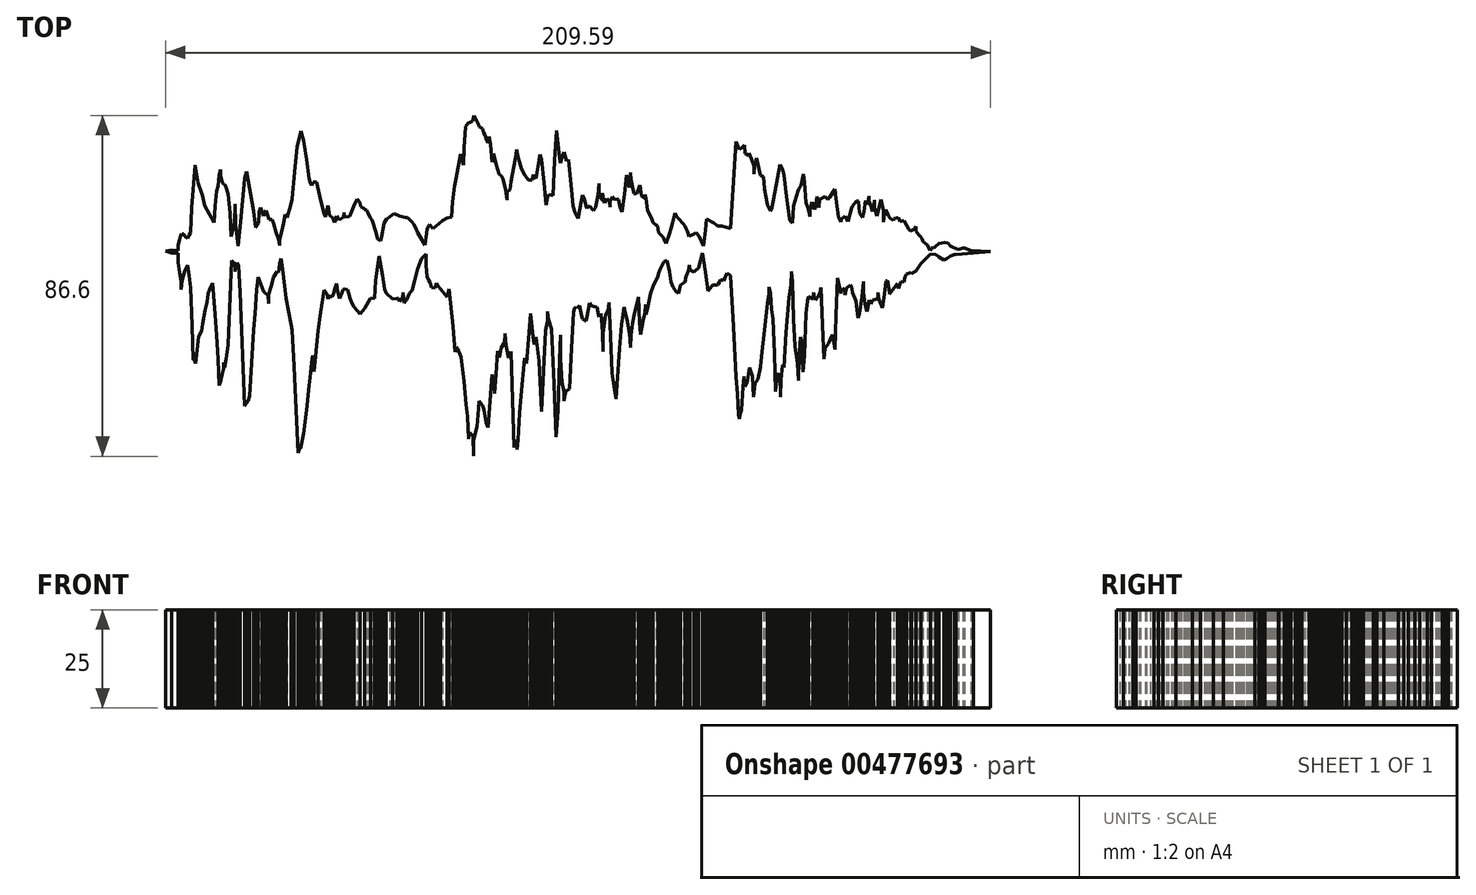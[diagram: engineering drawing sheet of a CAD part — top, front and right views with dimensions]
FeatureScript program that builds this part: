
annotation { "Feature Type Name" : "Feature", "Feature Type Description" : "" }
export const myFeature = defineFeature(function(context is Context, id is Id, definition is map)
    precondition{}
    {
        {
            var Q0;
            Q0=qCreatedBy(makeId("Top.planeOp"),FACE);
            var sketch = newSketch(context, id + "F0", { "sketchPlane" : qUnion([Q0])});
            skLineSegment(sketch, "E0", {"start": v(895.7, 1075.82) * mm, "end": v(892.97, 1101.18) * mm});
            skLineSegment(sketch, "E1", {"start": v(892.97, 1101.18) * mm, "end": v(888.39, 1081.07) * mm});
            skLineSegment(sketch, "E2", {"start": v(888.39, 1081.07) * mm, "end": v(885.06, 1201.57) * mm});
            skLineSegment(sketch, "E3", {"start": v(885.06, 1201.57) * mm, "end": v(881.56, 1324.24) * mm});
            skLineSegment(sketch, "E4", {"start": v(881.56, 1324.24) * mm, "end": v(878.07, 1317.45) * mm});
            skLineSegment(sketch, "E5", {"start": v(878.07, 1317.45) * mm, "end": v(875.1, 1308.5) * mm});
            skLineSegment(sketch, "E6", {"start": v(875.1, 1308.5) * mm, "end": v(868.65, 1339.11) * mm});
            skLineSegment(sketch, "E7", {"start": v(868.65, 1339.11) * mm, "end": v(865.17, 1369.73) * mm});
            skLineSegment(sketch, "E8", {"start": v(865.17, 1369.73) * mm, "end": v(864.62, 1347.86) * mm});
            skLineSegment(sketch, "E9", {"start": v(864.62, 1347.86) * mm, "end": v(856.04, 1333.86) * mm});
            skLineSegment(sketch, "E10", {"start": v(856.04, 1333.86) * mm, "end": v(853.42, 1317.24) * mm});
            skLineSegment(sketch, "E11", {"start": v(853.42, 1317.24) * mm, "end": v(851, 1309.37) * mm});
            skLineSegment(sketch, "E12", {"start": v(851, 1309.37) * mm, "end": v(846.38, 1326) * mm});
            skLineSegment(sketch, "E13", {"start": v(846.38, 1326) * mm, "end": v(842.73, 1267.38) * mm});
            skLineSegment(sketch, "E14", {"start": v(842.73, 1267.38) * mm, "end": v(839.58, 1217.52) * mm});
            skLineSegment(sketch, "E15", {"start": v(839.58, 1217.52) * mm, "end": v(836.43, 1246.4) * mm});
            skLineSegment(sketch, "E16", {"start": v(836.43, 1246.4) * mm, "end": v(833.1, 1266.5) * mm});
            skLineSegment(sketch, "E17", {"start": v(833.1, 1266.5) * mm, "end": v(825.08, 1165.04) * mm});
            skLineSegment(sketch, "E18", {"start": v(825.08, 1165.04) * mm, "end": v(823, 1131.79) * mm});
            skLineSegment(sketch, "E19", {"start": v(823, 1131.79) * mm, "end": v(818.08, 1144.36) * mm});
            skLineSegment(sketch, "E20", {"start": v(818.08, 1144.36) * mm, "end": v(811.87, 1175.86) * mm});
            skLineSegment(sketch, "E21", {"start": v(811.87, 1175.86) * mm, "end": v(808.56, 1186.9) * mm});
            skLineSegment(sketch, "E22", {"start": v(808.56, 1186.9) * mm, "end": v(800.2, 1199.15) * mm});
            skLineSegment(sketch, "E23", {"start": v(800.2, 1199.15) * mm, "end": v(797.9, 1179.04) * mm});
            skLineSegment(sketch, "E24", {"start": v(797.9, 1179.04) * mm, "end": v(795.18, 1134.42) * mm});
            skLineSegment(sketch, "E25", {"start": v(795.18, 1134.42) * mm, "end": v(786.2, 1099.43) * mm});
            skLineSegment(sketch, "E26", {"start": v(786.2, 1099.43) * mm, "end": v(785.1, 1058.32) * mm});
            skLineSegment(sketch, "E27", {"start": v(785.1, 1058.32) * mm, "end": v(784.35, 1109.93) * mm});
            skLineSegment(sketch, "E28", {"start": v(784.35, 1109.93) * mm, "end": v(776.03, 1118.68) * mm});
            skLineSegment(sketch, "E29", {"start": v(776.03, 1118.68) * mm, "end": v(772.99, 1102.06) * mm});
            skLineSegment(sketch, "E30", {"start": v(772.99, 1102.06) * mm, "end": v(770.05, 1158.92) * mm});
            skLineSegment(sketch, "E31", {"start": v(770.05, 1158.92) * mm, "end": v(766.4, 1189.53) * mm});
            skLineSegment(sketch, "E32", {"start": v(766.4, 1189.53) * mm, "end": v(762.03, 1247.55) * mm});
            skLineSegment(sketch, "E33", {"start": v(762.03, 1247.55) * mm, "end": v(754, 1310.57) * mm});
            skLineSegment(sketch, "E34", {"start": v(754, 1310.57) * mm, "end": v(744.85, 1332.15) * mm});
            skLineSegment(sketch, "E35", {"start": v(744.85, 1332.15) * mm, "end": v(742.07, 1335.61) * mm});
            skLineSegment(sketch, "E36", {"start": v(742.07, 1335.61) * mm, "end": v(738.64, 1322.5) * mm});
            skLineSegment(sketch, "E37", {"start": v(738.64, 1322.5) * mm, "end": v(733.44, 1388.1) * mm});
            skLineSegment(sketch, "E38", {"start": v(733.44, 1388.1) * mm, "end": v(723.65, 1483.44) * mm});
            skLineSegment(sketch, "E39", {"start": v(723.65, 1483.44) * mm, "end": v(720.61, 1472.95) * mm});
            skLineSegment(sketch, "E40", {"start": v(720.61, 1472.95) * mm, "end": v(718.72, 1462.45) * mm});
            skLineSegment(sketch, "E41", {"start": v(718.72, 1462.45) * mm, "end": v(701.57, 1482.57) * mm});
            skLineSegment(sketch, "E42", {"start": v(701.57, 1482.57) * mm, "end": v(695.88, 1490.44) * mm});
            skLineSegment(sketch, "E43", {"start": v(695.88, 1490.44) * mm, "end": v(692.34, 1498.32) * mm});
            skLineSegment(sketch, "E44", {"start": v(692.34, 1498.32) * mm, "end": v(687.5, 1486.07) * mm});
            skLineSegment(sketch, "E45", {"start": v(687.5, 1486.07) * mm, "end": v(678.62, 1487.15) * mm});
            skLineSegment(sketch, "E46", {"start": v(678.62, 1487.15) * mm, "end": v(675.13, 1499.2) * mm});
            skLineSegment(sketch, "E47", {"start": v(675.13, 1499.2) * mm, "end": v(671.63, 1505.98) * mm});
            skLineSegment(sketch, "E48", {"start": v(671.63, 1505.98) * mm, "end": v(668.13, 1514.94) * mm});
            skLineSegment(sketch, "E49", {"start": v(668.13, 1514.94) * mm, "end": v(664.63, 1543.45) * mm});
            skLineSegment(sketch, "E50", {"start": v(664.63, 1543.45) * mm, "end": v(664.63, 1571.96) * mm});
            skLineSegment(sketch, "E51", {"start": v(664.63, 1571.96) * mm, "end": v(654.13, 1560.97) * mm});
            skLineSegment(sketch, "E52", {"start": v(654.13, 1560.97) * mm, "end": v(643.63, 1534.21) * mm});
            skLineSegment(sketch, "E53", {"start": v(643.63, 1534.21) * mm, "end": v(640.14, 1518.43) * mm});
            skLineSegment(sketch, "E54", {"start": v(640.14, 1518.43) * mm, "end": v(636.4, 1503.56) * mm});
            skLineSegment(sketch, "E55", {"start": v(636.4, 1503.56) * mm, "end": v(629.89, 1479.07) * mm});
            skLineSegment(sketch, "E56", {"start": v(629.89, 1479.07) * mm, "end": v(622.64, 1473.48) * mm});
            skLineSegment(sketch, "E57", {"start": v(622.64, 1473.48) * mm, "end": v(615.87, 1455.72) * mm});
            skLineSegment(sketch, "E58", {"start": v(615.87, 1455.72) * mm, "end": v(609.1, 1447.9) * mm});
            skLineSegment(sketch, "E59", {"start": v(609.1, 1447.9) * mm, "end": v(607.71, 1461.3) * mm});
            skLineSegment(sketch, "E60", {"start": v(607.71, 1461.3) * mm, "end": v(606.32, 1474.7) * mm});
            skLineSegment(sketch, "E61", {"start": v(606.32, 1474.7) * mm, "end": v(605.73, 1459.83) * mm});
            skLineSegment(sketch, "E62", {"start": v(605.73, 1459.83) * mm, "end": v(598.15, 1451.75) * mm});
            skLineSegment(sketch, "E63", {"start": v(598.15, 1451.75) * mm, "end": v(594.65, 1460.7) * mm});
            skLineSegment(sketch, "E64", {"start": v(594.65, 1460.7) * mm, "end": v(591.15, 1459.1) * mm});
            skLineSegment(sketch, "E65", {"start": v(591.15, 1459.1) * mm, "end": v(580.07, 1457.3) * mm});
            skLineSegment(sketch, "E66", {"start": v(580.07, 1457.3) * mm, "end": v(563.16, 1473.15) * mm});
            skLineSegment(sketch, "E67", {"start": v(563.16, 1473.15) * mm, "end": v(560.18, 1483.44) * mm});
            skLineSegment(sketch, "E68", {"start": v(560.18, 1483.44) * mm, "end": v(554.8, 1517.44) * mm});
            skLineSegment(sketch, "E69", {"start": v(554.8, 1517.44) * mm, "end": v(545.7, 1567.42) * mm});
            skLineSegment(sketch, "E70", {"start": v(545.7, 1567.42) * mm, "end": v(536.45, 1505.15) * mm});
            skLineSegment(sketch, "E71", {"start": v(536.45, 1505.15) * mm, "end": v(534.09, 1458.63) * mm});
            skLineSegment(sketch, "E72", {"start": v(534.09, 1458.63) * mm, "end": v(524.26, 1460.8) * mm});
            skLineSegment(sketch, "E73", {"start": v(524.26, 1460.8) * mm, "end": v(509.04, 1433.98) * mm});
            skLineSegment(sketch, "E74", {"start": v(509.04, 1433.98) * mm, "end": v(497.48, 1419.43) * mm});
            skLineSegment(sketch, "E75", {"start": v(497.48, 1419.43) * mm, "end": v(482.74, 1436.97) * mm});
            skLineSegment(sketch, "E76", {"start": v(482.74, 1436.97) * mm, "end": v(477.43, 1446.22) * mm});
            skLineSegment(sketch, "E77", {"start": v(477.43, 1446.22) * mm, "end": v(472.19, 1458.58) * mm});
            skLineSegment(sketch, "E78", {"start": v(472.19, 1458.58) * mm, "end": v(468.69, 1472.95) * mm});
            skLineSegment(sketch, "E79", {"start": v(468.69, 1472.95) * mm, "end": v(465.19, 1481.7) * mm});
            skLineSegment(sketch, "E80", {"start": v(465.19, 1481.7) * mm, "end": v(457.94, 1482.57) * mm});
            skLineSegment(sketch, "E81", {"start": v(457.94, 1482.57) * mm, "end": v(454.7, 1481.7) * mm});
            skLineSegment(sketch, "E82", {"start": v(454.7, 1481.7) * mm, "end": v(451.44, 1473.82) * mm});
            skLineSegment(sketch, "E83", {"start": v(451.44, 1473.82) * mm, "end": v(445.94, 1458.95) * mm});
            skLineSegment(sketch, "E84", {"start": v(445.94, 1458.95) * mm, "end": v(440.7, 1478.2) * mm});
            skLineSegment(sketch, "E85", {"start": v(440.7, 1478.2) * mm, "end": v(437.2, 1497.44) * mm});
            skLineSegment(sketch, "E86", {"start": v(437.2, 1497.44) * mm, "end": v(433.7, 1485.4) * mm});
            skLineSegment(sketch, "E87", {"start": v(433.7, 1485.4) * mm, "end": v(430.2, 1471.2) * mm});
            skLineSegment(sketch, "E88", {"start": v(430.2, 1471.2) * mm, "end": v(426.7, 1462.24) * mm});
            skLineSegment(sketch, "E89", {"start": v(426.7, 1462.24) * mm, "end": v(419.15, 1465.08) * mm});
            skLineSegment(sketch, "E90", {"start": v(419.15, 1465.08) * mm, "end": v(416.2, 1457.2) * mm});
            skLineSegment(sketch, "E91", {"start": v(416.2, 1457.2) * mm, "end": v(413.25, 1470.32) * mm});
            skLineSegment(sketch, "E92", {"start": v(413.25, 1470.32) * mm, "end": v(405.68, 1480.82) * mm});
            skLineSegment(sketch, "E93", {"start": v(405.68, 1480.82) * mm, "end": v(397, 1423.96) * mm});
            skLineSegment(sketch, "E94", {"start": v(397, 1423.96) * mm, "end": v(390.37, 1377.6) * mm});
            skLineSegment(sketch, "E95", {"start": v(390.37, 1377.6) * mm, "end": v(380.7, 1273.5) * mm});
            skLineSegment(sketch, "E96", {"start": v(380.7, 1273.5) * mm, "end": v(377.25, 1293.63) * mm});
            skLineSegment(sketch, "E97", {"start": v(377.25, 1293.63) * mm, "end": v(376.78, 1313.75) * mm});
            skLineSegment(sketch, "E98", {"start": v(376.78, 1313.75) * mm, "end": v(374.05, 1296.25) * mm});
            skLineSegment(sketch, "E99", {"start": v(374.05, 1296.25) * mm, "end": v(371.02, 1258.93) * mm});
            skLineSegment(sketch, "E100", {"start": v(371.02, 1258.93) * mm, "end": v(367.44, 1237.93) * mm});
            skLineSegment(sketch, "E101", {"start": v(367.44, 1237.93) * mm, "end": v(361.68, 1176.41) * mm});
            skLineSegment(sketch, "E102", {"start": v(361.68, 1176.41) * mm, "end": v(354.46, 1116.05) * mm});
            skLineSegment(sketch, "E103", {"start": v(354.46, 1116.05) * mm, "end": v(349.26, 1090.69) * mm});
            skLineSegment(sketch, "E104", {"start": v(349.26, 1090.69) * mm, "end": v(346.22, 1077.57) * mm});
            skLineSegment(sketch, "E105", {"start": v(346.22, 1077.57) * mm, "end": v(343.65, 1089.81) * mm});
            skLineSegment(sketch, "E106", {"start": v(343.65, 1089.81) * mm, "end": v(343.19, 1078.44) * mm});
            skLineSegment(sketch, "E107", {"start": v(343.19, 1078.44) * mm, "end": v(339.75, 1067.07) * mm});
            skLineSegment(sketch, "E108", {"start": v(339.75, 1067.07) * mm, "end": v(329.94, 1286.63) * mm});
            skLineSegment(sketch, "E109", {"start": v(329.94, 1286.63) * mm, "end": v(324.69, 1378.48) * mm});
            skLineSegment(sketch, "E110", {"start": v(324.69, 1378.48) * mm, "end": v(321.73, 1392.33) * mm});
            skLineSegment(sketch, "E111", {"start": v(321.73, 1392.33) * mm, "end": v(309.57, 1458.95) * mm});
            skLineSegment(sketch, "E112", {"start": v(309.57, 1458.95) * mm, "end": v(300.76, 1533.3) * mm});
            skLineSegment(sketch, "E113", {"start": v(300.76, 1533.3) * mm, "end": v(297.24, 1560.42) * mm});
            skLineSegment(sketch, "E114", {"start": v(297.24, 1560.42) * mm, "end": v(293.4, 1547.3) * mm});
            skLineSegment(sketch, "E115", {"start": v(293.4, 1547.3) * mm, "end": v(290.24, 1525.43) * mm});
            skLineSegment(sketch, "E116", {"start": v(290.24, 1525.43) * mm, "end": v(287.1, 1528.06) * mm});
            skLineSegment(sketch, "E117", {"start": v(287.1, 1528.06) * mm, "end": v(278.13, 1513.4) * mm});
            skLineSegment(sketch, "E118", {"start": v(278.13, 1513.4) * mm, "end": v(270.72, 1489.28) * mm});
            skLineSegment(sketch, "E119", {"start": v(270.72, 1489.28) * mm, "end": v(265.09, 1468.95) * mm});
            skLineSegment(sketch, "E120", {"start": v(265.09, 1468.95) * mm, "end": v(264.42, 1446.7) * mm});
            skLineSegment(sketch, "E121", {"start": v(264.42, 1446.7) * mm, "end": v(263.16, 1466.82) * mm});
            skLineSegment(sketch, "E122", {"start": v(263.16, 1466.82) * mm, "end": v(254.3, 1473.82) * mm});
            skLineSegment(sketch, "E123", {"start": v(254.3, 1473.82) * mm, "end": v(252.29, 1476.45) * mm});
            skLineSegment(sketch, "E124", {"start": v(252.29, 1476.45) * mm, "end": v(248.39, 1487.05) * mm});
            skLineSegment(sketch, "E125", {"start": v(248.39, 1487.05) * mm, "end": v(238.35, 1513.35) * mm});
            skLineSegment(sketch, "E126", {"start": v(238.35, 1513.35) * mm, "end": v(234.71, 1480.82) * mm});
            skLineSegment(sketch, "E127", {"start": v(234.71, 1480.82) * mm, "end": v(230.76, 1420.46) * mm});
            skLineSegment(sketch, "E128", {"start": v(230.76, 1420.46) * mm, "end": v(227.26, 1378.86) * mm});
            skLineSegment(sketch, "E129", {"start": v(227.26, 1378.86) * mm, "end": v(216.56, 1211.1) * mm});
            skLineSegment(sketch, "E130", {"start": v(216.56, 1211.1) * mm, "end": v(213.26, 1198.2) * mm});
            skLineSegment(sketch, "E131", {"start": v(213.26, 1198.2) * mm, "end": v(203.68, 1185.47) * mm});
            skLineSegment(sketch, "E132", {"start": v(203.68, 1185.47) * mm, "end": v(192.28, 1475.57) * mm});
            skLineSegment(sketch, "E133", {"start": v(192.28, 1475.57) * mm, "end": v(188.77, 1542.93) * mm});
            skLineSegment(sketch, "E134", {"start": v(188.77, 1542.93) * mm, "end": v(184.75, 1550.8) * mm});
            skLineSegment(sketch, "E135", {"start": v(184.75, 1550.8) * mm, "end": v(181.77, 1542.93) * mm});
            skLineSegment(sketch, "E136", {"start": v(181.77, 1542.93) * mm, "end": v(179.32, 1527.18) * mm});
            skLineSegment(sketch, "E137", {"start": v(179.32, 1527.18) * mm, "end": v(178.8, 1547.3) * mm});
            skLineSegment(sketch, "E138", {"start": v(178.8, 1547.3) * mm, "end": v(171, 1556.05) * mm});
            skLineSegment(sketch, "E139", {"start": v(171, 1556.05) * mm, "end": v(161.51, 1340.82) * mm});
            skLineSegment(sketch, "E140", {"start": v(161.51, 1340.82) * mm, "end": v(156.82, 1305.58) * mm});
            skLineSegment(sketch, "E141", {"start": v(156.82, 1305.58) * mm, "end": v(153.78, 1284) * mm});
            skLineSegment(sketch, "E142", {"start": v(153.78, 1284) * mm, "end": v(151.2, 1296.25) * mm});
            skLineSegment(sketch, "E143", {"start": v(151.2, 1296.25) * mm, "end": v(150.74, 1281.38) * mm});
            skLineSegment(sketch, "E144", {"start": v(150.74, 1281.38) * mm, "end": v(146.78, 1266.5) * mm});
            skLineSegment(sketch, "E145", {"start": v(146.78, 1266.5) * mm, "end": v(142.94, 1248.14) * mm});
            skLineSegment(sketch, "E146", {"start": v(142.94, 1248.14) * mm, "end": v(139.79, 1238.52) * mm});
            skLineSegment(sketch, "E147", {"start": v(139.79, 1238.52) * mm, "end": v(136.64, 1305.87) * mm});
            skLineSegment(sketch, "E148", {"start": v(136.64, 1305.87) * mm, "end": v(132.79, 1364.48) * mm});
            skLineSegment(sketch, "E149", {"start": v(132.79, 1364.48) * mm, "end": v(128.98, 1417.84) * mm});
            skLineSegment(sketch, "E150", {"start": v(128.98, 1417.84) * mm, "end": v(122.76, 1498.32) * mm});
            skLineSegment(sketch, "E151", {"start": v(122.76, 1498.32) * mm, "end": v(118.8, 1490.44) * mm});
            skLineSegment(sketch, "E152", {"start": v(118.8, 1490.44) * mm, "end": v(115.3, 1481.9) * mm});
            skLineSegment(sketch, "E153", {"start": v(115.3, 1481.9) * mm, "end": v(111.8, 1471.2) * mm});
            skLineSegment(sketch, "E154", {"start": v(111.8, 1471.2) * mm, "end": v(108.3, 1450.29) * mm});
            skLineSegment(sketch, "E155", {"start": v(108.3, 1450.29) * mm, "end": v(104.2, 1430.18) * mm});
            skLineSegment(sketch, "E156", {"start": v(104.2, 1430.18) * mm, "end": v(97.75, 1394.03) * mm});
            skLineSegment(sketch, "E157", {"start": v(97.75, 1394.03) * mm, "end": v(94.84, 1375.85) * mm});
            skLineSegment(sketch, "E158", {"start": v(94.84, 1375.85) * mm, "end": v(87.27, 1361.86) * mm});
            skLineSegment(sketch, "E159", {"start": v(87.27, 1361.86) * mm, "end": v(79.82, 1294.5) * mm});
            skLineSegment(sketch, "E160", {"start": v(79.82, 1294.5) * mm, "end": v(76.4, 1304.12) * mm});
            skLineSegment(sketch, "E161", {"start": v(76.4, 1304.12) * mm, "end": v(75.98, 1313.75) * mm});
            skLineSegment(sketch, "E162", {"start": v(75.98, 1313.75) * mm, "end": v(73.3, 1303.25) * mm});
            skLineSegment(sketch, "E163", {"start": v(73.3, 1303.25) * mm, "end": v(70.22, 1389.85) * mm});
            skLineSegment(sketch, "E164", {"start": v(70.22, 1389.85) * mm, "end": v(66.3, 1486.94) * mm});
            skLineSegment(sketch, "E165", {"start": v(66.3, 1486.94) * mm, "end": v(62.8, 1516.9) * mm});
            skLineSegment(sketch, "E166", {"start": v(62.8, 1516.9) * mm, "end": v(59.3, 1544.68) * mm});
            skLineSegment(sketch, "E167", {"start": v(59.3, 1544.68) * mm, "end": v(55.81, 1536.01) * mm});
            skLineSegment(sketch, "E168", {"start": v(55.81, 1536.01) * mm, "end": v(51.84, 1528.2) * mm});
            skLineSegment(sketch, "E169", {"start": v(51.84, 1528.2) * mm, "end": v(45.33, 1504.28) * mm});
            skLineSegment(sketch, "E170", {"start": v(45.33, 1504.28) * mm, "end": v(42.77, 1481.7) * mm});
            skLineSegment(sketch, "E171", {"start": v(42.77, 1481.7) * mm, "end": v(42.3, 1503.56) * mm});
            skLineSegment(sketch, "E172", {"start": v(42.3, 1503.56) * mm, "end": v(38.32, 1525.43) * mm});
            skLineSegment(sketch, "E173", {"start": v(38.32, 1525.43) * mm, "end": v(34.82, 1549.93) * mm});
            skLineSegment(sketch, "E174", {"start": v(34.82, 1549.93) * mm, "end": v(34.82, 1574.42) * mm});
            skLineSegment(sketch, "E175", {"start": v(34.82, 1574.42) * mm, "end": v(19.07, 1574.42) * mm});
            skLineSegment(sketch, "E176", {"start": v(19.07, 1574.42) * mm, "end": v(3.33, 1579.6) * mm});
            skLineSegment(sketch, "E177", {"start": v(3.33, 1579.6) * mm, "end": v(19.07, 1582.62) * mm});
            skLineSegment(sketch, "E178", {"start": v(19.07, 1582.62) * mm, "end": v(34.82, 1580.46) * mm});
            skLineSegment(sketch, "E179", {"start": v(34.82, 1580.46) * mm, "end": v(34.82, 1594.94) * mm});
            skLineSegment(sketch, "E180", {"start": v(34.82, 1594.94) * mm, "end": v(38.32, 1609.4) * mm});
            skLineSegment(sketch, "E181", {"start": v(38.32, 1609.4) * mm, "end": v(42.1, 1619.03) * mm});
            skLineSegment(sketch, "E182", {"start": v(42.1, 1619.03) * mm, "end": v(44.13, 1624.28) * mm});
            skLineSegment(sketch, "E183", {"start": v(44.13, 1624.28) * mm, "end": v(50.85, 1619.9) * mm});
            skLineSegment(sketch, "E184", {"start": v(50.85, 1619.9) * mm, "end": v(55.81, 1614.45) * mm});
            skLineSegment(sketch, "E185", {"start": v(55.81, 1614.45) * mm, "end": v(59.3, 1611.16) * mm});
            skLineSegment(sketch, "E186", {"start": v(59.3, 1611.16) * mm, "end": v(62.8, 1620.11) * mm});
            skLineSegment(sketch, "E187", {"start": v(62.8, 1620.11) * mm, "end": v(66.3, 1626.9) * mm});
            skLineSegment(sketch, "E188", {"start": v(66.3, 1626.9) * mm, "end": v(69.83, 1689) * mm});
            skLineSegment(sketch, "E189", {"start": v(69.83, 1689) * mm, "end": v(78.76, 1797.97) * mm});
            skLineSegment(sketch, "E190", {"start": v(78.76, 1797.97) * mm, "end": v(86.53, 1752.95) * mm});
            skLineSegment(sketch, "E191", {"start": v(86.53, 1752.95) * mm, "end": v(95.23, 1727.5) * mm});
            skLineSegment(sketch, "E192", {"start": v(95.23, 1727.5) * mm, "end": v(97.17, 1718.86) * mm});
            skLineSegment(sketch, "E193", {"start": v(97.17, 1718.86) * mm, "end": v(103.05, 1695.62) * mm});
            skLineSegment(sketch, "E194", {"start": v(103.05, 1695.62) * mm, "end": v(108.3, 1683.21) * mm});
            skLineSegment(sketch, "E195", {"start": v(108.3, 1683.21) * mm, "end": v(126.52, 1652.45) * mm});
            skLineSegment(sketch, "E196", {"start": v(126.52, 1652.45) * mm, "end": v(129.23, 1694.26) * mm});
            skLineSegment(sketch, "E197", {"start": v(129.23, 1694.26) * mm, "end": v(132.79, 1731.87) * mm});
            skLineSegment(sketch, "E198", {"start": v(132.79, 1731.87) * mm, "end": v(136.49, 1745) * mm});
            skLineSegment(sketch, "E199", {"start": v(136.49, 1745) * mm, "end": v(139.58, 1772.1) * mm});
            skLineSegment(sketch, "E200", {"start": v(139.58, 1772.1) * mm, "end": v(142.48, 1786.1) * mm});
            skLineSegment(sketch, "E201", {"start": v(142.48, 1786.1) * mm, "end": v(142.88, 1771.23) * mm});
            skLineSegment(sketch, "E202", {"start": v(142.88, 1771.23) * mm, "end": v(146.78, 1756.36) * mm});
            skLineSegment(sketch, "E203", {"start": v(146.78, 1756.36) * mm, "end": v(150.63, 1748.5) * mm});
            skLineSegment(sketch, "E204", {"start": v(150.63, 1748.5) * mm, "end": v(153.78, 1749.37) * mm});
            skLineSegment(sketch, "E205", {"start": v(153.78, 1749.37) * mm, "end": v(156.93, 1741.5) * mm});
            skLineSegment(sketch, "E206", {"start": v(156.93, 1741.5) * mm, "end": v(162.53, 1724.87) * mm});
            skLineSegment(sketch, "E207", {"start": v(162.53, 1724.87) * mm, "end": v(167.78, 1676.32) * mm});
            skLineSegment(sketch, "E208", {"start": v(167.78, 1676.32) * mm, "end": v(169.96, 1616.84) * mm});
            skLineSegment(sketch, "E209", {"start": v(169.96, 1616.84) * mm, "end": v(179, 1652.27) * mm});
            skLineSegment(sketch, "E210", {"start": v(179, 1652.27) * mm, "end": v(179.74, 1698.63) * mm});
            skLineSegment(sketch, "E211", {"start": v(179.74, 1698.63) * mm, "end": v(181.63, 1646.43) * mm});
            skLineSegment(sketch, "E212", {"start": v(181.63, 1646.43) * mm, "end": v(187.67, 1592.85) * mm});
            skLineSegment(sketch, "E213", {"start": v(187.67, 1592.85) * mm, "end": v(193.63, 1653.8) * mm});
            skLineSegment(sketch, "E214", {"start": v(193.63, 1653.8) * mm, "end": v(203.5, 1763.8) * mm});
            skLineSegment(sketch, "E215", {"start": v(203.5, 1763.8) * mm, "end": v(208.83, 1781.99) * mm});
            skLineSegment(sketch, "E216", {"start": v(208.83, 1781.99) * mm, "end": v(227.26, 1680.76) * mm});
            skLineSegment(sketch, "E217", {"start": v(227.26, 1680.76) * mm, "end": v(232.06, 1639.1) * mm});
            skLineSegment(sketch, "E218", {"start": v(232.06, 1639.1) * mm, "end": v(239.06, 1650.33) * mm});
            skLineSegment(sketch, "E219", {"start": v(239.06, 1650.33) * mm, "end": v(241.26, 1678.13) * mm});
            skLineSegment(sketch, "E220", {"start": v(241.26, 1678.13) * mm, "end": v(244.75, 1689.88) * mm});
            skLineSegment(sketch, "E221", {"start": v(244.75, 1689.88) * mm, "end": v(248.25, 1679.39) * mm});
            skLineSegment(sketch, "E222", {"start": v(248.25, 1679.39) * mm, "end": v(251.75, 1668.89) * mm});
            skLineSegment(sketch, "E223", {"start": v(251.75, 1668.89) * mm, "end": v(255.25, 1675.89) * mm});
            skLineSegment(sketch, "E224", {"start": v(255.25, 1675.89) * mm, "end": v(258.38, 1682.89) * mm});
            skLineSegment(sketch, "E225", {"start": v(258.38, 1682.89) * mm, "end": v(265.75, 1659.86) * mm});
            skLineSegment(sketch, "E226", {"start": v(265.75, 1659.86) * mm, "end": v(273.53, 1659.27) * mm});
            skLineSegment(sketch, "E227", {"start": v(273.53, 1659.27) * mm, "end": v(277.72, 1649.65) * mm});
            skLineSegment(sketch, "E228", {"start": v(277.72, 1649.65) * mm, "end": v(284.32, 1626.32) * mm});
            skLineSegment(sketch, "E229", {"start": v(284.32, 1626.32) * mm, "end": v(290.4, 1608.83) * mm});
            skLineSegment(sketch, "E230", {"start": v(290.4, 1608.83) * mm, "end": v(292.86, 1593.66) * mm});
            skLineSegment(sketch, "E231", {"start": v(292.86, 1593.66) * mm, "end": v(293.3, 1608.53) * mm});
            skLineSegment(sketch, "E232", {"start": v(293.3, 1608.53) * mm, "end": v(296.83, 1623.4) * mm});
            skLineSegment(sketch, "E233", {"start": v(296.83, 1623.4) * mm, "end": v(302.55, 1650.52) * mm});
            skLineSegment(sketch, "E234", {"start": v(302.55, 1650.52) * mm, "end": v(306.99, 1672.39) * mm});
            skLineSegment(sketch, "E235", {"start": v(306.99, 1672.39) * mm, "end": v(312.63, 1664.61) * mm});
            skLineSegment(sketch, "E236", {"start": v(312.63, 1664.61) * mm, "end": v(321.32, 1695.71) * mm});
            skLineSegment(sketch, "E237", {"start": v(321.32, 1695.71) * mm, "end": v(325.28, 1711.48) * mm});
            skLineSegment(sketch, "E238", {"start": v(325.28, 1711.48) * mm, "end": v(331.07, 1779.68) * mm});
            skLineSegment(sketch, "E239", {"start": v(331.07, 1779.68) * mm, "end": v(337.76, 1845) * mm});
            skLineSegment(sketch, "E240", {"start": v(337.76, 1845) * mm, "end": v(347.42, 1884.08) * mm});
            skLineSegment(sketch, "E241", {"start": v(347.42, 1884.08) * mm, "end": v(349.2, 1878.24) * mm});
            skLineSegment(sketch, "E242", {"start": v(349.2, 1878.24) * mm, "end": v(353.58, 1860.63) * mm});
            skLineSegment(sketch, "E243", {"start": v(353.58, 1860.63) * mm, "end": v(360.97, 1812.23) * mm});
            skLineSegment(sketch, "E244", {"start": v(360.97, 1812.23) * mm, "end": v(367.6, 1763.94) * mm});
            skLineSegment(sketch, "E245", {"start": v(367.6, 1763.94) * mm, "end": v(370.72, 1754.32) * mm});
            skLineSegment(sketch, "E246", {"start": v(370.72, 1754.32) * mm, "end": v(374.22, 1745.87) * mm});
            skLineSegment(sketch, "E247", {"start": v(374.22, 1745.87) * mm, "end": v(377.71, 1754.9) * mm});
            skLineSegment(sketch, "E248", {"start": v(377.71, 1754.9) * mm, "end": v(387.14, 1754.34) * mm});
            skLineSegment(sketch, "E249", {"start": v(387.14, 1754.34) * mm, "end": v(396.83, 1708.6) * mm});
            skLineSegment(sketch, "E250", {"start": v(396.83, 1708.6) * mm, "end": v(405.67, 1675.01) * mm});
            skLineSegment(sketch, "E251", {"start": v(405.67, 1675.01) * mm, "end": v(409.2, 1665.4) * mm});
            skLineSegment(sketch, "E252", {"start": v(409.2, 1665.4) * mm, "end": v(412.7, 1681.34) * mm});
            skLineSegment(sketch, "E253", {"start": v(412.7, 1681.34) * mm, "end": v(416.2, 1695.13) * mm});
            skLineSegment(sketch, "E254", {"start": v(416.2, 1695.13) * mm, "end": v(419.7, 1670.43) * mm});
            skLineSegment(sketch, "E255", {"start": v(419.7, 1670.43) * mm, "end": v(427.3, 1664.52) * mm});
            skLineSegment(sketch, "E256", {"start": v(427.3, 1664.52) * mm, "end": v(430.2, 1658.4) * mm});
            skLineSegment(sketch, "E257", {"start": v(430.2, 1658.4) * mm, "end": v(433.1, 1652.56) * mm});
            skLineSegment(sketch, "E258", {"start": v(433.1, 1652.56) * mm, "end": v(438.07, 1668.03) * mm});
            skLineSegment(sketch, "E259", {"start": v(438.07, 1668.03) * mm, "end": v(443.59, 1658.8) * mm});
            skLineSegment(sketch, "E260", {"start": v(443.59, 1658.8) * mm, "end": v(455.1, 1665.67) * mm});
            skLineSegment(sketch, "E261", {"start": v(455.1, 1665.67) * mm, "end": v(457.27, 1677.64) * mm});
            skLineSegment(sketch, "E262", {"start": v(457.27, 1677.64) * mm, "end": v(457.73, 1666.27) * mm});
            skLineSegment(sketch, "E263", {"start": v(457.73, 1666.27) * mm, "end": v(470.2, 1667.14) * mm});
            skLineSegment(sketch, "E264", {"start": v(470.2, 1667.14) * mm, "end": v(475.69, 1679.39) * mm});
            skLineSegment(sketch, "E265", {"start": v(475.69, 1679.39) * mm, "end": v(481.24, 1692.5) * mm});
            skLineSegment(sketch, "E266", {"start": v(481.24, 1692.5) * mm, "end": v(490.15, 1711.89) * mm});
            skLineSegment(sketch, "E267", {"start": v(490.15, 1711.89) * mm, "end": v(496.96, 1703.14) * mm});
            skLineSegment(sketch, "E268", {"start": v(496.96, 1703.14) * mm, "end": v(499, 1692.5) * mm});
            skLineSegment(sketch, "E269", {"start": v(499, 1692.5) * mm, "end": v(507.42, 1687.26) * mm});
            skLineSegment(sketch, "E270", {"start": v(507.42, 1687.26) * mm, "end": v(510.67, 1684.63) * mm});
            skLineSegment(sketch, "E271", {"start": v(510.67, 1684.63) * mm, "end": v(513.93, 1683.76) * mm});
            skLineSegment(sketch, "E272", {"start": v(513.93, 1683.76) * mm, "end": v(517.4, 1675.89) * mm});
            skLineSegment(sketch, "E273", {"start": v(517.4, 1675.89) * mm, "end": v(523.02, 1664.92) * mm});
            skLineSegment(sketch, "E274", {"start": v(523.02, 1664.92) * mm, "end": v(528.36, 1658.7) * mm});
            skLineSegment(sketch, "E275", {"start": v(528.36, 1658.7) * mm, "end": v(538.08, 1626.72) * mm});
            skLineSegment(sketch, "E276", {"start": v(538.08, 1626.72) * mm, "end": v(541.69, 1610.28) * mm});
            skLineSegment(sketch, "E277", {"start": v(541.69, 1610.28) * mm, "end": v(549.73, 1605.03) * mm});
            skLineSegment(sketch, "E278", {"start": v(549.73, 1605.03) * mm, "end": v(552.41, 1615.7) * mm});
            skLineSegment(sketch, "E279", {"start": v(552.41, 1615.7) * mm, "end": v(558.37, 1650.68) * mm});
            skLineSegment(sketch, "E280", {"start": v(558.37, 1650.68) * mm, "end": v(564.62, 1660.84) * mm});
            skLineSegment(sketch, "E281", {"start": v(564.62, 1660.84) * mm, "end": v(572.06, 1666.6) * mm});
            skLineSegment(sketch, "E282", {"start": v(572.06, 1666.6) * mm, "end": v(580.4, 1672.9) * mm});
            skLineSegment(sketch, "E283", {"start": v(580.4, 1672.9) * mm, "end": v(583.93, 1675.01) * mm});
            skLineSegment(sketch, "E284", {"start": v(583.93, 1675.01) * mm, "end": v(597.86, 1668.89) * mm});
            skLineSegment(sketch, "E285", {"start": v(597.86, 1668.89) * mm, "end": v(613.6, 1664.52) * mm});
            skLineSegment(sketch, "E286", {"start": v(613.6, 1664.52) * mm, "end": v(617.67, 1664.48) * mm});
            skLineSegment(sketch, "E287", {"start": v(617.67, 1664.48) * mm, "end": v(629.64, 1653.4) * mm});
            skLineSegment(sketch, "E288", {"start": v(629.64, 1653.4) * mm, "end": v(633.14, 1647.9) * mm});
            skLineSegment(sketch, "E289", {"start": v(633.14, 1647.9) * mm, "end": v(636.64, 1642.65) * mm});
            skLineSegment(sketch, "E290", {"start": v(636.64, 1642.65) * mm, "end": v(640.14, 1637.4) * mm});
            skLineSegment(sketch, "E291", {"start": v(640.14, 1637.4) * mm, "end": v(643.63, 1626.85) * mm});
            skLineSegment(sketch, "E292", {"start": v(643.63, 1626.85) * mm, "end": v(662, 1595.47) * mm});
            skLineSegment(sketch, "E293", {"start": v(662, 1595.47) * mm, "end": v(664.63, 1614.66) * mm});
            skLineSegment(sketch, "E294", {"start": v(664.63, 1614.66) * mm, "end": v(668.13, 1633.9) * mm});
            skLineSegment(sketch, "E295", {"start": v(668.13, 1633.9) * mm, "end": v(672.15, 1645.27) * mm});
            skLineSegment(sketch, "E296", {"start": v(672.15, 1645.27) * mm, "end": v(674.13, 1647.02) * mm});
            skLineSegment(sketch, "E297", {"start": v(674.13, 1647.02) * mm, "end": v(682.36, 1637.4) * mm});
            skLineSegment(sketch, "E298", {"start": v(682.36, 1637.4) * mm, "end": v(689.12, 1642.27) * mm});
            skLineSegment(sketch, "E299", {"start": v(689.12, 1642.27) * mm, "end": v(697.87, 1649.33) * mm});
            skLineSegment(sketch, "E300", {"start": v(697.87, 1649.33) * mm, "end": v(706.62, 1656.55) * mm});
            skLineSegment(sketch, "E301", {"start": v(706.62, 1656.55) * mm, "end": v(718.35, 1663.78) * mm});
            skLineSegment(sketch, "E302", {"start": v(718.35, 1663.78) * mm, "end": v(730.1, 1665.98) * mm});
            skLineSegment(sketch, "E303", {"start": v(730.1, 1665.98) * mm, "end": v(732.15, 1704.98) * mm});
            skLineSegment(sketch, "E304", {"start": v(732.15, 1704.98) * mm, "end": v(737.9, 1745.22) * mm});
            skLineSegment(sketch, "E305", {"start": v(737.9, 1745.22) * mm, "end": v(741.6, 1764.24) * mm});
            skLineSegment(sketch, "E306", {"start": v(741.6, 1764.24) * mm, "end": v(752.4, 1826.34) * mm});
            skLineSegment(sketch, "E307", {"start": v(752.4, 1826.34) * mm, "end": v(760.22, 1798.35) * mm});
            skLineSegment(sketch, "E308", {"start": v(760.22, 1798.35) * mm, "end": v(762.04, 1841.21) * mm});
            skLineSegment(sketch, "E309", {"start": v(762.04, 1841.21) * mm, "end": v(765.7, 1896.32) * mm});
            skLineSegment(sketch, "E310", {"start": v(765.7, 1896.32) * mm, "end": v(771.3, 1904.2) * mm});
            skLineSegment(sketch, "E311", {"start": v(771.3, 1904.2) * mm, "end": v(775.47, 1905.94) * mm});
            skLineSegment(sketch, "E312", {"start": v(775.47, 1905.94) * mm, "end": v(783.65, 1909.44) * mm});
            skLineSegment(sketch, "E313", {"start": v(783.65, 1909.44) * mm, "end": v(787.15, 1924.31) * mm});
            skLineSegment(sketch, "E314", {"start": v(787.15, 1924.31) * mm, "end": v(798.1, 1901.57) * mm});
            skLineSegment(sketch, "E315", {"start": v(798.1, 1901.57) * mm, "end": v(800.12, 1895.45) * mm});
            skLineSegment(sketch, "E316", {"start": v(800.12, 1895.45) * mm, "end": v(808.33, 1890.2) * mm});
            skLineSegment(sketch, "E317", {"start": v(808.33, 1890.2) * mm, "end": v(811.58, 1880.58) * mm});
            skLineSegment(sketch, "E318", {"start": v(811.58, 1880.58) * mm, "end": v(814.84, 1874.45) * mm});
            skLineSegment(sketch, "E319", {"start": v(814.84, 1874.45) * mm, "end": v(818.58, 1861.33) * mm});
            skLineSegment(sketch, "E320", {"start": v(818.58, 1861.33) * mm, "end": v(822.7, 1853.46) * mm});
            skLineSegment(sketch, "E321", {"start": v(822.7, 1853.46) * mm, "end": v(825.58, 1870.08) * mm});
            skLineSegment(sketch, "E322", {"start": v(825.58, 1870.08) * mm, "end": v(828.46, 1849.96) * mm});
            skLineSegment(sketch, "E323", {"start": v(828.46, 1849.96) * mm, "end": v(832.58, 1805.35) * mm});
            skLineSegment(sketch, "E324", {"start": v(832.58, 1805.35) * mm, "end": v(836.5, 1827.22) * mm});
            skLineSegment(sketch, "E325", {"start": v(836.5, 1827.22) * mm, "end": v(842.66, 1800.57) * mm});
            skLineSegment(sketch, "E326", {"start": v(842.66, 1800.57) * mm, "end": v(850.07, 1774.87) * mm});
            skLineSegment(sketch, "E327", {"start": v(850.07, 1774.87) * mm, "end": v(857.07, 1770.32) * mm});
            skLineSegment(sketch, "E328", {"start": v(857.07, 1770.32) * mm, "end": v(860.58, 1762.78) * mm});
            skLineSegment(sketch, "E329", {"start": v(860.58, 1762.78) * mm, "end": v(867.12, 1735.37) * mm});
            skLineSegment(sketch, "E330", {"start": v(867.12, 1735.37) * mm, "end": v(870.16, 1709.13) * mm});
            skLineSegment(sketch, "E331", {"start": v(870.16, 1709.13) * mm, "end": v(870.61, 1729.25) * mm});
            skLineSegment(sketch, "E332", {"start": v(870.61, 1729.25) * mm, "end": v(879.02, 1736.24) * mm});
            skLineSegment(sketch, "E333", {"start": v(879.02, 1736.24) * mm, "end": v(880.98, 1755.6) * mm});
            skLineSegment(sketch, "E334", {"start": v(880.98, 1755.6) * mm, "end": v(886.81, 1790.09) * mm});
            skLineSegment(sketch, "E335", {"start": v(886.81, 1790.09) * mm, "end": v(892.11, 1817.1) * mm});
            skLineSegment(sketch, "E336", {"start": v(892.11, 1817.1) * mm, "end": v(895.56, 1836.84) * mm});
            skLineSegment(sketch, "E337", {"start": v(895.56, 1836.84) * mm, "end": v(899, 1818.47) * mm});
            skLineSegment(sketch, "E338", {"start": v(899, 1818.47) * mm, "end": v(902.44, 1805.35) * mm});
            skLineSegment(sketch, "E339", {"start": v(902.44, 1805.35) * mm, "end": v(908.17, 1787.57) * mm});
            skLineSegment(sketch, "E340", {"start": v(908.17, 1787.57) * mm, "end": v(916.8, 1771.44) * mm});
            skLineSegment(sketch, "E341", {"start": v(916.8, 1771.44) * mm, "end": v(925.37, 1759.47) * mm});
            skLineSegment(sketch, "E342", {"start": v(925.37, 1759.47) * mm, "end": v(934.05, 1759.86) * mm});
            skLineSegment(sketch, "E343", {"start": v(934.05, 1759.86) * mm, "end": v(937.55, 1773.86) * mm});
            skLineSegment(sketch, "E344", {"start": v(937.55, 1773.86) * mm, "end": v(941.05, 1768.6) * mm});
            skLineSegment(sketch, "E345", {"start": v(941.05, 1768.6) * mm, "end": v(944.1, 1763.36) * mm});
            skLineSegment(sketch, "E346", {"start": v(944.1, 1763.36) * mm, "end": v(952.07, 1810.16) * mm});
            skLineSegment(sketch, "E347", {"start": v(952.07, 1810.16) * mm, "end": v(954.13, 1824.6) * mm});
            skLineSegment(sketch, "E348", {"start": v(954.13, 1824.6) * mm, "end": v(958.93, 1812.1) * mm});
            skLineSegment(sketch, "E349", {"start": v(958.93, 1812.1) * mm, "end": v(964.4, 1753.5) * mm});
            skLineSegment(sketch, "E350", {"start": v(964.4, 1753.5) * mm, "end": v(969.59, 1696.88) * mm});
            skLineSegment(sketch, "E351", {"start": v(969.59, 1696.88) * mm, "end": v(973.03, 1717) * mm});
            skLineSegment(sketch, "E352", {"start": v(973.03, 1717) * mm, "end": v(975.66, 1723.4) * mm});
            skLineSegment(sketch, "E353", {"start": v(975.66, 1723.4) * mm, "end": v(987.8, 1720.32) * mm});
            skLineSegment(sketch, "E354", {"start": v(987.8, 1720.32) * mm, "end": v(992.02, 1809.72) * mm});
            skLineSegment(sketch, "E355", {"start": v(992.02, 1809.72) * mm, "end": v(996.93, 1885.82) * mm});
            skLineSegment(sketch, "E356", {"start": v(996.93, 1885.82) * mm, "end": v(1004.63, 1817.6) * mm});
            skLineSegment(sketch, "E357", {"start": v(1004.63, 1817.6) * mm, "end": v(1006.6, 1802.72) * mm});
            skLineSegment(sketch, "E358", {"start": v(1006.6, 1802.72) * mm, "end": v(1011, 1819.34) * mm});
            skLineSegment(sketch, "E359", {"start": v(1011, 1819.34) * mm, "end": v(1015.5, 1830.72) * mm});
            skLineSegment(sketch, "E360", {"start": v(1015.5, 1830.72) * mm, "end": v(1017.52, 1822.84) * mm});
            skLineSegment(sketch, "E361", {"start": v(1017.52, 1822.84) * mm, "end": v(1021.39, 1808.75) * mm});
            skLineSegment(sketch, "E362", {"start": v(1021.39, 1808.75) * mm, "end": v(1027.1, 1811.44) * mm});
            skLineSegment(sketch, "E363", {"start": v(1027.1, 1811.44) * mm, "end": v(1035.3, 1722.25) * mm});
            skLineSegment(sketch, "E364", {"start": v(1035.3, 1722.25) * mm, "end": v(1038.62, 1693.38) * mm});
            skLineSegment(sketch, "E365", {"start": v(1038.62, 1693.38) * mm, "end": v(1044.08, 1677.64) * mm});
            skLineSegment(sketch, "E366", {"start": v(1044.08, 1677.64) * mm, "end": v(1051.04, 1661.9) * mm});
            skLineSegment(sketch, "E367", {"start": v(1051.04, 1661.9) * mm, "end": v(1060.57, 1708.7) * mm});
            skLineSegment(sketch, "E368", {"start": v(1060.57, 1708.7) * mm, "end": v(1062.54, 1722.25) * mm});
            skLineSegment(sketch, "E369", {"start": v(1062.54, 1722.25) * mm, "end": v(1067.23, 1710.88) * mm});
            skLineSegment(sketch, "E370", {"start": v(1067.23, 1710.88) * mm, "end": v(1070.92, 1694.26) * mm});
            skLineSegment(sketch, "E371", {"start": v(1070.92, 1694.26) * mm, "end": v(1074, 1688.13) * mm});
            skLineSegment(sketch, "E372", {"start": v(1074, 1688.13) * mm, "end": v(1077.1, 1693.88) * mm});
            skLineSegment(sketch, "E373", {"start": v(1077.1, 1693.88) * mm, "end": v(1082.75, 1691.15) * mm});
            skLineSegment(sketch, "E374", {"start": v(1082.75, 1691.15) * mm, "end": v(1088.28, 1685.4) * mm});
            skLineSegment(sketch, "E375", {"start": v(1088.28, 1685.4) * mm, "end": v(1090.55, 1682.89) * mm});
            skLineSegment(sketch, "E376", {"start": v(1090.55, 1682.89) * mm, "end": v(1095.71, 1690.2) * mm});
            skLineSegment(sketch, "E377", {"start": v(1095.71, 1690.2) * mm, "end": v(1101.7, 1721.7) * mm});
            skLineSegment(sketch, "E378", {"start": v(1101.7, 1721.7) * mm, "end": v(1104.54, 1751.12) * mm});
            skLineSegment(sketch, "E379", {"start": v(1104.54, 1751.12) * mm, "end": v(1105.02, 1720.5) * mm});
            skLineSegment(sketch, "E380", {"start": v(1105.02, 1720.5) * mm, "end": v(1113.02, 1708.25) * mm});
            skLineSegment(sketch, "E381", {"start": v(1113.02, 1708.25) * mm, "end": v(1113.55, 1726.62) * mm});
            skLineSegment(sketch, "E382", {"start": v(1113.55, 1726.62) * mm, "end": v(1116, 1710.88) * mm});
            skLineSegment(sketch, "E383", {"start": v(1116, 1710.88) * mm, "end": v(1118.97, 1701.5) * mm});
            skLineSegment(sketch, "E384", {"start": v(1118.97, 1701.5) * mm, "end": v(1124.53, 1712.91) * mm});
            skLineSegment(sketch, "E385", {"start": v(1124.53, 1712.91) * mm, "end": v(1130.94, 1704.8) * mm});
            skLineSegment(sketch, "E386", {"start": v(1130.94, 1704.8) * mm, "end": v(1132.31, 1691.63) * mm});
            skLineSegment(sketch, "E387", {"start": v(1132.31, 1691.63) * mm, "end": v(1132.9, 1704.75) * mm});
            skLineSegment(sketch, "E388", {"start": v(1132.9, 1704.75) * mm, "end": v(1138.74, 1717.88) * mm});
            skLineSegment(sketch, "E389", {"start": v(1138.74, 1717.88) * mm, "end": v(1143.99, 1710.88) * mm});
            skLineSegment(sketch, "E390", {"start": v(1143.99, 1710.88) * mm, "end": v(1151.33, 1711.75) * mm});
            skLineSegment(sketch, "E391", {"start": v(1151.33, 1711.75) * mm, "end": v(1154.48, 1710.88) * mm});
            skLineSegment(sketch, "E392", {"start": v(1154.48, 1710.88) * mm, "end": v(1157.63, 1691.13) * mm});
            skLineSegment(sketch, "E393", {"start": v(1157.63, 1691.13) * mm, "end": v(1163.13, 1678.16) * mm});
            skLineSegment(sketch, "E394", {"start": v(1163.13, 1678.16) * mm, "end": v(1169.26, 1723.86) * mm});
            skLineSegment(sketch, "E395", {"start": v(1169.26, 1723.86) * mm, "end": v(1174.6, 1772.99) * mm});
            skLineSegment(sketch, "E396", {"start": v(1174.6, 1772.99) * mm, "end": v(1179.55, 1757.53) * mm});
            skLineSegment(sketch, "E397", {"start": v(1179.55, 1757.53) * mm, "end": v(1180.12, 1740.62) * mm});
            skLineSegment(sketch, "E398", {"start": v(1180.12, 1740.62) * mm, "end": v(1182.47, 1759.86) * mm});
            skLineSegment(sketch, "E399", {"start": v(1182.47, 1759.86) * mm, "end": v(1184.83, 1779.1) * mm});
            skLineSegment(sketch, "E400", {"start": v(1184.83, 1779.1) * mm, "end": v(1185.4, 1760.74) * mm});
            skLineSegment(sketch, "E401", {"start": v(1185.4, 1760.74) * mm, "end": v(1189.47, 1742.37) * mm});
            skLineSegment(sketch, "E402", {"start": v(1189.47, 1742.37) * mm, "end": v(1193.38, 1725.75) * mm});
            skLineSegment(sketch, "E403", {"start": v(1193.38, 1725.75) * mm, "end": v(1199.55, 1724) * mm});
            skLineSegment(sketch, "E404", {"start": v(1199.55, 1724) * mm, "end": v(1208.26, 1746.74) * mm});
            skLineSegment(sketch, "E405", {"start": v(1208.26, 1746.74) * mm, "end": v(1212.38, 1718.75) * mm});
            skLineSegment(sketch, "E406", {"start": v(1212.38, 1718.75) * mm, "end": v(1221.38, 1713.5) * mm});
            skLineSegment(sketch, "E407", {"start": v(1221.38, 1713.5) * mm, "end": v(1221.8, 1723.12) * mm});
            skLineSegment(sketch, "E408", {"start": v(1221.8, 1723.12) * mm, "end": v(1224.46, 1712.63) * mm});
            skLineSegment(sketch, "E409", {"start": v(1224.46, 1712.63) * mm, "end": v(1227.55, 1683.51) * mm});
            skLineSegment(sketch, "E410", {"start": v(1227.55, 1683.51) * mm, "end": v(1239.65, 1659.3) * mm});
            skLineSegment(sketch, "E411", {"start": v(1239.65, 1659.3) * mm, "end": v(1241.68, 1652.27) * mm});
            skLineSegment(sketch, "E412", {"start": v(1241.68, 1652.27) * mm, "end": v(1249, 1645.27) * mm});
            skLineSegment(sketch, "E413", {"start": v(1249, 1645.27) * mm, "end": v(1252.45, 1644.4) * mm});
            skLineSegment(sketch, "E414", {"start": v(1252.45, 1644.4) * mm, "end": v(1255.9, 1626.4) * mm});
            skLineSegment(sketch, "E415", {"start": v(1255.9, 1626.4) * mm, "end": v(1267.57, 1615.72) * mm});
            skLineSegment(sketch, "E416", {"start": v(1267.57, 1615.72) * mm, "end": v(1269.54, 1610.28) * mm});
            skLineSegment(sketch, "E417", {"start": v(1269.54, 1610.28) * mm, "end": v(1274.82, 1598.91) * mm});
            skLineSegment(sketch, "E418", {"start": v(1274.82, 1598.91) * mm, "end": v(1283.94, 1623.69) * mm});
            skLineSegment(sketch, "E419", {"start": v(1283.94, 1623.69) * mm, "end": v(1287.44, 1637.4) * mm});
            skLineSegment(sketch, "E420", {"start": v(1287.44, 1637.4) * mm, "end": v(1291.36, 1650.52) * mm});
            skLineSegment(sketch, "E421", {"start": v(1291.36, 1650.52) * mm, "end": v(1297.53, 1676.76) * mm});
            skLineSegment(sketch, "E422", {"start": v(1297.53, 1676.76) * mm, "end": v(1301.44, 1668.89) * mm});
            skLineSegment(sketch, "E423", {"start": v(1301.44, 1668.89) * mm, "end": v(1304.94, 1663.4) * mm});
            skLineSegment(sketch, "E424", {"start": v(1304.94, 1663.4) * mm, "end": v(1318.68, 1647.9) * mm});
            skLineSegment(sketch, "E425", {"start": v(1318.68, 1647.9) * mm, "end": v(1322.43, 1642.65) * mm});
            skLineSegment(sketch, "E426", {"start": v(1322.43, 1642.65) * mm, "end": v(1325.93, 1637.4) * mm});
            skLineSegment(sketch, "E427", {"start": v(1325.93, 1637.4) * mm, "end": v(1329.48, 1629.53) * mm});
            skLineSegment(sketch, "E428", {"start": v(1329.48, 1629.53) * mm, "end": v(1332.93, 1616.4) * mm});
            skLineSegment(sketch, "E429", {"start": v(1332.93, 1616.4) * mm, "end": v(1336.37, 1619.03) * mm});
            skLineSegment(sketch, "E430", {"start": v(1336.37, 1619.03) * mm, "end": v(1346.23, 1622.7) * mm});
            skLineSegment(sketch, "E431", {"start": v(1346.23, 1622.7) * mm, "end": v(1350.42, 1626.2) * mm});
            skLineSegment(sketch, "E432", {"start": v(1350.42, 1626.2) * mm, "end": v(1358.78, 1617.28) * mm});
            skLineSegment(sketch, "E433", {"start": v(1358.78, 1617.28) * mm, "end": v(1369.96, 1592.8) * mm});
            skLineSegment(sketch, "E434", {"start": v(1369.96, 1592.8) * mm, "end": v(1374.87, 1632.93) * mm});
            skLineSegment(sketch, "E435", {"start": v(1374.87, 1632.93) * mm, "end": v(1377.89, 1661.02) * mm});
            skLineSegment(sketch, "E436", {"start": v(1377.89, 1661.02) * mm, "end": v(1396.79, 1651.21) * mm});
            skLineSegment(sketch, "E437", {"start": v(1396.79, 1651.21) * mm, "end": v(1403.18, 1645.5) * mm});
            skLineSegment(sketch, "E438", {"start": v(1403.18, 1645.5) * mm, "end": v(1405.23, 1643.52) * mm});
            skLineSegment(sketch, "E439", {"start": v(1405.23, 1643.52) * mm, "end": v(1416.9, 1643.06) * mm});
            skLineSegment(sketch, "E440", {"start": v(1416.9, 1643.06) * mm, "end": v(1437.9, 1636.39) * mm});
            skLineSegment(sketch, "E441", {"start": v(1437.9, 1636.39) * mm, "end": v(1444.9, 1737.1) * mm});
            skLineSegment(sketch, "E442", {"start": v(1444.9, 1737.1) * mm, "end": v(1451.94, 1857.83) * mm});
            skLineSegment(sketch, "E443", {"start": v(1451.94, 1857.83) * mm, "end": v(1457.33, 1844.71) * mm});
            skLineSegment(sketch, "E444", {"start": v(1457.33, 1844.71) * mm, "end": v(1461.52, 1837.97) * mm});
            skLineSegment(sketch, "E445", {"start": v(1461.52, 1837.97) * mm, "end": v(1467.73, 1842.54) * mm});
            skLineSegment(sketch, "E446", {"start": v(1467.73, 1842.54) * mm, "end": v(1473.94, 1848.4) * mm});
            skLineSegment(sketch, "E447", {"start": v(1473.94, 1848.4) * mm, "end": v(1475.91, 1827.22) * mm});
            skLineSegment(sketch, "E448", {"start": v(1475.91, 1827.22) * mm, "end": v(1484.02, 1821.97) * mm});
            skLineSegment(sketch, "E449", {"start": v(1484.02, 1821.97) * mm, "end": v(1485.97, 1828.67) * mm});
            skLineSegment(sketch, "E450", {"start": v(1485.97, 1828.67) * mm, "end": v(1492.34, 1813.7) * mm});
            skLineSegment(sketch, "E451", {"start": v(1492.34, 1813.7) * mm, "end": v(1498.04, 1795.62) * mm});
            skLineSegment(sketch, "E452", {"start": v(1498.04, 1795.62) * mm, "end": v(1498.7, 1775.6) * mm});
            skLineSegment(sketch, "E453", {"start": v(1498.7, 1775.6) * mm, "end": v(1499.97, 1795.73) * mm});
            skLineSegment(sketch, "E454", {"start": v(1499.97, 1795.73) * mm, "end": v(1503.95, 1815.85) * mm});
            skLineSegment(sketch, "E455", {"start": v(1503.95, 1815.85) * mm, "end": v(1514.87, 1771.84) * mm});
            skLineSegment(sketch, "E456", {"start": v(1514.87, 1771.84) * mm, "end": v(1522.43, 1769.48) * mm});
            skLineSegment(sketch, "E457", {"start": v(1522.43, 1769.48) * mm, "end": v(1525.24, 1737.75) * mm});
            skLineSegment(sketch, "E458", {"start": v(1525.24, 1737.75) * mm, "end": v(1532.17, 1697) * mm});
            skLineSegment(sketch, "E459", {"start": v(1532.17, 1697) * mm, "end": v(1539.46, 1680.63) * mm});
            skLineSegment(sketch, "E460", {"start": v(1539.46, 1680.63) * mm, "end": v(1542.46, 1685.5) * mm});
            skLineSegment(sketch, "E461", {"start": v(1542.46, 1685.5) * mm, "end": v(1545.95, 1703.88) * mm});
            skLineSegment(sketch, "E462", {"start": v(1545.95, 1703.88) * mm, "end": v(1551.27, 1731) * mm});
            skLineSegment(sketch, "E463", {"start": v(1551.27, 1731) * mm, "end": v(1564.17, 1799.44) * mm});
            skLineSegment(sketch, "E464", {"start": v(1564.17, 1799.44) * mm, "end": v(1570.86, 1787.82) * mm});
            skLineSegment(sketch, "E465", {"start": v(1570.86, 1787.82) * mm, "end": v(1573.95, 1773.28) * mm});
            skLineSegment(sketch, "E466", {"start": v(1573.95, 1773.28) * mm, "end": v(1580.48, 1718.03) * mm});
            skLineSegment(sketch, "E467", {"start": v(1580.48, 1718.03) * mm, "end": v(1587.9, 1662.63) * mm});
            skLineSegment(sketch, "E468", {"start": v(1587.9, 1662.63) * mm, "end": v(1591.9, 1653.73) * mm});
            skLineSegment(sketch, "E469", {"start": v(1591.9, 1653.73) * mm, "end": v(1595.35, 1651.4) * mm});
            skLineSegment(sketch, "E470", {"start": v(1595.35, 1651.4) * mm, "end": v(1598.8, 1694.26) * mm});
            skLineSegment(sketch, "E471", {"start": v(1598.8, 1694.26) * mm, "end": v(1610.22, 1732.29) * mm});
            skLineSegment(sketch, "E472", {"start": v(1610.22, 1732.29) * mm, "end": v(1612.85, 1738.87) * mm});
            skLineSegment(sketch, "E473", {"start": v(1612.85, 1738.87) * mm, "end": v(1617.95, 1745.87) * mm});
            skLineSegment(sketch, "E474", {"start": v(1617.95, 1745.87) * mm, "end": v(1624.24, 1774.73) * mm});
            skLineSegment(sketch, "E475", {"start": v(1624.24, 1774.73) * mm, "end": v(1626.13, 1754.03) * mm});
            skLineSegment(sketch, "E476", {"start": v(1626.13, 1754.03) * mm, "end": v(1630.51, 1703.24) * mm});
            skLineSegment(sketch, "E477", {"start": v(1630.51, 1703.24) * mm, "end": v(1637.1, 1684.58) * mm});
            skLineSegment(sketch, "E478", {"start": v(1637.1, 1684.58) * mm, "end": v(1640.01, 1667.14) * mm});
            skLineSegment(sketch, "E479", {"start": v(1640.01, 1667.14) * mm, "end": v(1640.43, 1685.5) * mm});
            skLineSegment(sketch, "E480", {"start": v(1640.43, 1685.5) * mm, "end": v(1645.9, 1703.88) * mm});
            skLineSegment(sketch, "E481", {"start": v(1645.9, 1703.88) * mm, "end": v(1652.25, 1685.5) * mm});
            skLineSegment(sketch, "E482", {"start": v(1652.25, 1685.5) * mm, "end": v(1654.19, 1692.5) * mm});
            skLineSegment(sketch, "E483", {"start": v(1654.19, 1692.5) * mm, "end": v(1658.18, 1717.88) * mm});
            skLineSegment(sketch, "E484", {"start": v(1658.18, 1717.88) * mm, "end": v(1662.73, 1690.76) * mm});
            skLineSegment(sketch, "E485", {"start": v(1662.73, 1690.76) * mm, "end": v(1664.63, 1710) * mm});
            skLineSegment(sketch, "E486", {"start": v(1664.63, 1710) * mm, "end": v(1678.12, 1717.96) * mm});
            skLineSegment(sketch, "E487", {"start": v(1678.12, 1717.96) * mm, "end": v(1686.67, 1710) * mm});
            skLineSegment(sketch, "E488", {"start": v(1686.67, 1710) * mm, "end": v(1689.3, 1715.36) * mm});
            skLineSegment(sketch, "E489", {"start": v(1689.3, 1715.36) * mm, "end": v(1703.9, 1737.68) * mm});
            skLineSegment(sketch, "E490", {"start": v(1703.9, 1737.68) * mm, "end": v(1706.82, 1713.13) * mm});
            skLineSegment(sketch, "E491", {"start": v(1706.82, 1713.13) * mm, "end": v(1712.37, 1666.58) * mm});
            skLineSegment(sketch, "E492", {"start": v(1712.37, 1666.58) * mm, "end": v(1718.76, 1653.84) * mm});
            skLineSegment(sketch, "E493", {"start": v(1718.76, 1653.84) * mm, "end": v(1720.7, 1661.02) * mm});
            skLineSegment(sketch, "E494", {"start": v(1720.7, 1661.02) * mm, "end": v(1729.65, 1668.89) * mm});
            skLineSegment(sketch, "E495", {"start": v(1729.65, 1668.89) * mm, "end": v(1736.7, 1654.9) * mm});
            skLineSegment(sketch, "E496", {"start": v(1736.7, 1654.9) * mm, "end": v(1746.32, 1688.13) * mm});
            skLineSegment(sketch, "E497", {"start": v(1746.32, 1688.13) * mm, "end": v(1748.34, 1694.26) * mm});
            skLineSegment(sketch, "E498", {"start": v(1748.34, 1694.26) * mm, "end": v(1758.04, 1706.5) * mm});
            skLineSegment(sketch, "E499", {"start": v(1758.04, 1706.5) * mm, "end": v(1763.02, 1706.5) * mm});
            skLineSegment(sketch, "E500", {"start": v(1763.02, 1706.5) * mm, "end": v(1766.7, 1675.89) * mm});
            skLineSegment(sketch, "E501", {"start": v(1766.7, 1675.89) * mm, "end": v(1773.38, 1664.52) * mm});
            skLineSegment(sketch, "E502", {"start": v(1773.38, 1664.52) * mm, "end": v(1776.98, 1680.26) * mm});
            skLineSegment(sketch, "E503", {"start": v(1776.98, 1680.26) * mm, "end": v(1780.8, 1707.38) * mm});
            skLineSegment(sketch, "E504", {"start": v(1780.8, 1707.38) * mm, "end": v(1784.82, 1697.76) * mm});
            skLineSegment(sketch, "E505", {"start": v(1784.82, 1697.76) * mm, "end": v(1787.8, 1703.88) * mm});
            skLineSegment(sketch, "E506", {"start": v(1787.8, 1703.88) * mm, "end": v(1790.24, 1719.62) * mm});
            skLineSegment(sketch, "E507", {"start": v(1790.24, 1719.62) * mm, "end": v(1790.77, 1706.5) * mm});
            skLineSegment(sketch, "E508", {"start": v(1790.77, 1706.5) * mm, "end": v(1794.8, 1693.38) * mm});
            skLineSegment(sketch, "E509", {"start": v(1794.8, 1693.38) * mm, "end": v(1798.88, 1680.26) * mm});
            skLineSegment(sketch, "E510", {"start": v(1798.88, 1680.26) * mm, "end": v(1801.79, 1688.13) * mm});
            skLineSegment(sketch, "E511", {"start": v(1801.79, 1688.13) * mm, "end": v(1804.11, 1709.13) * mm});
            skLineSegment(sketch, "E512", {"start": v(1804.11, 1709.13) * mm, "end": v(1804.7, 1689) * mm});
            skLineSegment(sketch, "E513", {"start": v(1804.7, 1689) * mm, "end": v(1810.54, 1668.89) * mm});
            skLineSegment(sketch, "E514", {"start": v(1810.54, 1668.89) * mm, "end": v(1815.78, 1689.88) * mm});
            skLineSegment(sketch, "E515", {"start": v(1815.78, 1689.88) * mm, "end": v(1821.03, 1710.88) * mm});
            skLineSegment(sketch, "E516", {"start": v(1821.03, 1710.88) * mm, "end": v(1826.87, 1682.01) * mm});
            skLineSegment(sketch, "E517", {"start": v(1826.87, 1682.01) * mm, "end": v(1827.46, 1653.14) * mm});
            skLineSegment(sketch, "E518", {"start": v(1827.46, 1653.14) * mm, "end": v(1829.78, 1674.14) * mm});
            skLineSegment(sketch, "E519", {"start": v(1829.78, 1674.14) * mm, "end": v(1832.7, 1685.5) * mm});
            skLineSegment(sketch, "E520", {"start": v(1832.7, 1685.5) * mm, "end": v(1836.78, 1675.89) * mm});
            skLineSegment(sketch, "E521", {"start": v(1836.78, 1675.89) * mm, "end": v(1840.28, 1668.89) * mm});
            skLineSegment(sketch, "E522", {"start": v(1840.28, 1668.89) * mm, "end": v(1845.23, 1661.9) * mm});
            skLineSegment(sketch, "E523", {"start": v(1845.23, 1661.9) * mm, "end": v(1851.96, 1657.52) * mm});
            skLineSegment(sketch, "E524", {"start": v(1851.96, 1657.52) * mm, "end": v(1854, 1662.48) * mm});
            skLineSegment(sketch, "E525", {"start": v(1854, 1662.48) * mm, "end": v(1865, 1664.52) * mm});
            skLineSegment(sketch, "E526", {"start": v(1865, 1664.52) * mm, "end": v(1869.04, 1654.02) * mm});
            skLineSegment(sketch, "E527", {"start": v(1869.04, 1654.02) * mm, "end": v(1878.77, 1656.8) * mm});
            skLineSegment(sketch, "E528", {"start": v(1878.77, 1656.8) * mm, "end": v(1891.57, 1633.9) * mm});
            skLineSegment(sketch, "E529", {"start": v(1891.57, 1633.9) * mm, "end": v(1896.26, 1629.87) * mm});
            skLineSegment(sketch, "E530", {"start": v(1896.26, 1629.87) * mm, "end": v(1903.26, 1633.9) * mm});
            skLineSegment(sketch, "E531", {"start": v(1903.26, 1633.9) * mm, "end": v(1910.26, 1641.97) * mm});
            skLineSegment(sketch, "E532", {"start": v(1910.26, 1641.97) * mm, "end": v(1910.26, 1631.05) * mm});
            skLineSegment(sketch, "E533", {"start": v(1910.26, 1631.05) * mm, "end": v(1915.5, 1622.14) * mm});
            skLineSegment(sketch, "E534", {"start": v(1915.5, 1622.14) * mm, "end": v(1920.75, 1616.57) * mm});
            skLineSegment(sketch, "E535", {"start": v(1920.75, 1616.57) * mm, "end": v(1924.25, 1611.16) * mm});
            skLineSegment(sketch, "E536", {"start": v(1924.25, 1611.16) * mm, "end": v(1927.75, 1604.37) * mm});
            skLineSegment(sketch, "E537", {"start": v(1927.75, 1604.37) * mm, "end": v(1939.12, 1595) * mm});
            skLineSegment(sketch, "E538", {"start": v(1939.12, 1595) * mm, "end": v(1941.75, 1588.41) * mm});
            skLineSegment(sketch, "E539", {"start": v(1941.75, 1588.41) * mm, "end": v(1945.25, 1581.42) * mm});
            skLineSegment(sketch, "E540", {"start": v(1945.25, 1581.42) * mm, "end": v(1948.8, 1587.54) * mm});
            skLineSegment(sketch, "E541", {"start": v(1948.8, 1587.54) * mm, "end": v(1952.24, 1588.41) * mm});
            skLineSegment(sketch, "E542", {"start": v(1952.24, 1588.41) * mm, "end": v(1955.69, 1587.54) * mm});
            skLineSegment(sketch, "E543", {"start": v(1955.69, 1587.54) * mm, "end": v(1960.76, 1591.91) * mm});
            skLineSegment(sketch, "E544", {"start": v(1960.76, 1591.91) * mm, "end": v(1967.99, 1598.91) * mm});
            skLineSegment(sketch, "E545", {"start": v(1967.99, 1598.91) * mm, "end": v(1981.42, 1601.53) * mm});
            skLineSegment(sketch, "E546", {"start": v(1981.42, 1601.53) * mm, "end": v(1983.46, 1601.53) * mm});
            skLineSegment(sketch, "E547", {"start": v(1983.46, 1601.53) * mm, "end": v(1990.73, 1600.55) * mm});
            skLineSegment(sketch, "E548", {"start": v(1990.73, 1600.55) * mm, "end": v(1996.86, 1592.93) * mm});
            skLineSegment(sketch, "E549", {"start": v(1996.86, 1592.93) * mm, "end": v(2004.73, 1588.34) * mm});
            skLineSegment(sketch, "E550", {"start": v(2004.73, 1588.34) * mm, "end": v(2017.85, 1583.8) * mm});
            skLineSegment(sketch, "E551", {"start": v(2017.85, 1583.8) * mm, "end": v(2029.33, 1587.63) * mm});
            skLineSegment(sketch, "E552", {"start": v(2029.33, 1587.63) * mm, "end": v(2033.14, 1587.3) * mm});
            skLineSegment(sketch, "E553", {"start": v(2033.14, 1587.3) * mm, "end": v(2049.65, 1581.5) * mm});
            skLineSegment(sketch, "E554", {"start": v(2049.65, 1581.5) * mm, "end": v(2099.2, 1577.92) * mm});
            skLineSegment(sketch, "E555", {"start": v(2099.2, 1577.92) * mm, "end": v(2055.46, 1574.42) * mm});
            skLineSegment(sketch, "E556", {"start": v(2055.46, 1574.42) * mm, "end": v(2011.73, 1570.22) * mm});
            skLineSegment(sketch, "E557", {"start": v(2011.73, 1570.22) * mm, "end": v(2007.53, 1570.22) * mm});
            skLineSegment(sketch, "E558", {"start": v(2007.53, 1570.22) * mm, "end": v(1997.73, 1567.42) * mm});
            skLineSegment(sketch, "E559", {"start": v(1997.73, 1567.42) * mm, "end": v(1988.98, 1560.42) * mm});
            skLineSegment(sketch, "E560", {"start": v(1988.98, 1560.42) * mm, "end": v(1980.24, 1557.03) * mm});
            skLineSegment(sketch, "E561", {"start": v(1980.24, 1557.03) * mm, "end": v(1968.66, 1564.16) * mm});
            skLineSegment(sketch, "E562", {"start": v(1968.66, 1564.16) * mm, "end": v(1960.44, 1571.21) * mm});
            skLineSegment(sketch, "E563", {"start": v(1960.44, 1571.21) * mm, "end": v(1946.15, 1572.37) * mm});
            skLineSegment(sketch, "E564", {"start": v(1946.15, 1572.37) * mm, "end": v(1922.7, 1547.95) * mm});
            skLineSegment(sketch, "E565", {"start": v(1922.7, 1547.95) * mm, "end": v(1910.26, 1528.57) * mm});
            skLineSegment(sketch, "E566", {"start": v(1910.26, 1528.57) * mm, "end": v(1898.62, 1522.51) * mm});
            skLineSegment(sketch, "E567", {"start": v(1898.62, 1522.51) * mm, "end": v(1896.67, 1524.45) * mm});
            skLineSegment(sketch, "E568", {"start": v(1896.67, 1524.45) * mm, "end": v(1885.76, 1521.77) * mm});
            skLineSegment(sketch, "E569", {"start": v(1885.76, 1521.77) * mm, "end": v(1882.27, 1513.19) * mm});
            skLineSegment(sketch, "E570", {"start": v(1882.27, 1513.19) * mm, "end": v(1878.77, 1500.73) * mm});
            skLineSegment(sketch, "E571", {"start": v(1878.77, 1500.73) * mm, "end": v(1871.18, 1501.81) * mm});
            skLineSegment(sketch, "E572", {"start": v(1871.18, 1501.81) * mm, "end": v(1868.27, 1492.2) * mm});
            skLineSegment(sketch, "E573", {"start": v(1868.27, 1492.2) * mm, "end": v(1865.36, 1484.32) * mm});
            skLineSegment(sketch, "E574", {"start": v(1865.36, 1484.32) * mm, "end": v(1863.18, 1497.44) * mm});
            skLineSegment(sketch, "E575", {"start": v(1863.18, 1497.44) * mm, "end": v(1842.8, 1470.4) * mm});
            skLineSegment(sketch, "E576", {"start": v(1842.8, 1470.4) * mm, "end": v(1840.8, 1482.57) * mm});
            skLineSegment(sketch, "E577", {"start": v(1840.8, 1482.57) * mm, "end": v(1836.78, 1504.44) * mm});
            skLineSegment(sketch, "E578", {"start": v(1836.78, 1504.44) * mm, "end": v(1833.19, 1503.56) * mm});
            skLineSegment(sketch, "E579", {"start": v(1833.19, 1503.56) * mm, "end": v(1829.93, 1469.98) * mm});
            skLineSegment(sketch, "E580", {"start": v(1829.93, 1469.98) * mm, "end": v(1824.77, 1435.28) * mm});
            skLineSegment(sketch, "E581", {"start": v(1824.77, 1435.28) * mm, "end": v(1815.48, 1456.54) * mm});
            skLineSegment(sketch, "E582", {"start": v(1815.48, 1456.54) * mm, "end": v(1813.27, 1474.7) * mm});
            skLineSegment(sketch, "E583", {"start": v(1813.27, 1474.7) * mm, "end": v(1812.78, 1459.54) * mm});
            skLineSegment(sketch, "E584", {"start": v(1812.78, 1459.54) * mm, "end": v(1801.36, 1455.71) * mm});
            skLineSegment(sketch, "E585", {"start": v(1801.36, 1455.71) * mm, "end": v(1798.64, 1454.58) * mm});
            skLineSegment(sketch, "E586", {"start": v(1798.64, 1454.58) * mm, "end": v(1795.02, 1444.96) * mm});
            skLineSegment(sketch, "E587", {"start": v(1795.02, 1444.96) * mm, "end": v(1790.3, 1454.58) * mm});
            skLineSegment(sketch, "E588", {"start": v(1790.3, 1454.58) * mm, "end": v(1787.67, 1436.2) * mm});
            skLineSegment(sketch, "E589", {"start": v(1787.67, 1436.2) * mm, "end": v(1785.21, 1426.59) * mm});
            skLineSegment(sketch, "E590", {"start": v(1785.21, 1426.59) * mm, "end": v(1780.61, 1444.96) * mm});
            skLineSegment(sketch, "E591", {"start": v(1780.61, 1444.96) * mm, "end": v(1776.74, 1473.82) * mm});
            skLineSegment(sketch, "E592", {"start": v(1776.74, 1473.82) * mm, "end": v(1776.19, 1502.69) * mm});
            skLineSegment(sketch, "E593", {"start": v(1776.19, 1502.69) * mm, "end": v(1772.75, 1462.45) * mm});
            skLineSegment(sketch, "E594", {"start": v(1772.75, 1462.45) * mm, "end": v(1766.66, 1420.46) * mm});
            skLineSegment(sketch, "E595", {"start": v(1766.66, 1420.46) * mm, "end": v(1762.38, 1409.97) * mm});
            skLineSegment(sketch, "E596", {"start": v(1762.38, 1409.97) * mm, "end": v(1760, 1429.21) * mm});
            skLineSegment(sketch, "E597", {"start": v(1760, 1429.21) * mm, "end": v(1757.48, 1452.83) * mm});
            skLineSegment(sketch, "E598", {"start": v(1757.48, 1452.83) * mm, "end": v(1748.96, 1473.82) * mm});
            skLineSegment(sketch, "E599", {"start": v(1748.96, 1473.82) * mm, "end": v(1745.8, 1490.44) * mm});
            skLineSegment(sketch, "E600", {"start": v(1745.8, 1490.44) * mm, "end": v(1742.66, 1493.07) * mm});
            skLineSegment(sketch, "E601", {"start": v(1742.66, 1493.07) * mm, "end": v(1732.5, 1486.07) * mm});
            skLineSegment(sketch, "E602", {"start": v(1732.5, 1486.07) * mm, "end": v(1729.14, 1467.7) * mm});
            skLineSegment(sketch, "E603", {"start": v(1729.14, 1467.7) * mm, "end": v(1728.73, 1486.07) * mm});
            skLineSegment(sketch, "E604", {"start": v(1728.73, 1486.07) * mm, "end": v(1720.68, 1479.07) * mm});
            skLineSegment(sketch, "E605", {"start": v(1720.68, 1479.07) * mm, "end": v(1718.93, 1471.2) * mm});
            skLineSegment(sketch, "E606", {"start": v(1718.93, 1471.2) * mm, "end": v(1710.66, 1511.44) * mm});
            skLineSegment(sketch, "E607", {"start": v(1710.66, 1511.44) * mm, "end": v(1706.97, 1416.1) * mm});
            skLineSegment(sketch, "E608", {"start": v(1706.97, 1416.1) * mm, "end": v(1703.82, 1329.5) * mm});
            skLineSegment(sketch, "E609", {"start": v(1703.82, 1329.5) * mm, "end": v(1700.67, 1353.1) * mm});
            skLineSegment(sketch, "E610", {"start": v(1700.67, 1353.1) * mm, "end": v(1697.27, 1367.98) * mm});
            skLineSegment(sketch, "E611", {"start": v(1697.27, 1367.98) * mm, "end": v(1691.52, 1353.1) * mm});
            skLineSegment(sketch, "E612", {"start": v(1691.52, 1353.1) * mm, "end": v(1687.31, 1344.36) * mm});
            skLineSegment(sketch, "E613", {"start": v(1687.31, 1344.36) * mm, "end": v(1678.98, 1332.12) * mm});
            skLineSegment(sketch, "E614", {"start": v(1678.98, 1332.12) * mm, "end": v(1675.83, 1305) * mm});
            skLineSegment(sketch, "E615", {"start": v(1675.83, 1305) * mm, "end": v(1672.68, 1391.6) * mm});
            skLineSegment(sketch, "E616", {"start": v(1672.68, 1391.6) * mm, "end": v(1668.83, 1486.94) * mm});
            skLineSegment(sketch, "E617", {"start": v(1668.83, 1486.94) * mm, "end": v(1665.33, 1473.06) * mm});
            skLineSegment(sketch, "E618", {"start": v(1665.33, 1473.06) * mm, "end": v(1660.08, 1461.19) * mm});
            skLineSegment(sketch, "E619", {"start": v(1660.08, 1461.19) * mm, "end": v(1654.34, 1454.95) * mm});
            skLineSegment(sketch, "E620", {"start": v(1654.34, 1454.95) * mm, "end": v(1651.33, 1460.7) * mm});
            skLineSegment(sketch, "E621", {"start": v(1651.33, 1460.7) * mm, "end": v(1648.83, 1474.7) * mm});
            skLineSegment(sketch, "E622", {"start": v(1648.83, 1474.7) * mm, "end": v(1648.33, 1457.79) * mm});
            skLineSegment(sketch, "E623", {"start": v(1648.33, 1457.79) * mm, "end": v(1637.05, 1464.47) * mm});
            skLineSegment(sketch, "E624", {"start": v(1637.05, 1464.47) * mm, "end": v(1634.43, 1452.83) * mm});
            skLineSegment(sketch, "E625", {"start": v(1634.43, 1452.83) * mm, "end": v(1630.34, 1420.46) * mm});
            skLineSegment(sketch, "E626", {"start": v(1630.34, 1420.46) * mm, "end": v(1626.22, 1314.62) * mm});
            skLineSegment(sketch, "E627", {"start": v(1626.22, 1314.62) * mm, "end": v(1623.15, 1271.76) * mm});
            skLineSegment(sketch, "E628", {"start": v(1623.15, 1271.76) * mm, "end": v(1620.28, 1347.86) * mm});
            skLineSegment(sketch, "E629", {"start": v(1620.28, 1347.86) * mm, "end": v(1616.34, 1360.98) * mm});
            skLineSegment(sketch, "E630", {"start": v(1616.34, 1360.98) * mm, "end": v(1612.28, 1305.87) * mm});
            skLineSegment(sketch, "E631", {"start": v(1612.28, 1305.87) * mm, "end": v(1611.72, 1250.76) * mm});
            skLineSegment(sketch, "E632", {"start": v(1611.72, 1250.76) * mm, "end": v(1608.31, 1293.63) * mm});
            skLineSegment(sketch, "E633", {"start": v(1608.31, 1293.63) * mm, "end": v(1601.88, 1336.49) * mm});
            skLineSegment(sketch, "E634", {"start": v(1601.88, 1336.49) * mm, "end": v(1598.42, 1407.34) * mm});
            skLineSegment(sketch, "E635", {"start": v(1598.42, 1407.34) * mm, "end": v(1595.47, 1502.69) * mm});
            skLineSegment(sketch, "E636", {"start": v(1595.47, 1502.69) * mm, "end": v(1592.95, 1527.18) * mm});
            skLineSegment(sketch, "E637", {"start": v(1592.95, 1527.18) * mm, "end": v(1592.4, 1495.1) * mm});
            skLineSegment(sketch, "E638", {"start": v(1592.4, 1495.1) * mm, "end": v(1587.68, 1461.64) * mm});
            skLineSegment(sketch, "E639", {"start": v(1587.68, 1461.64) * mm, "end": v(1580.08, 1372.13) * mm});
            skLineSegment(sketch, "E640", {"start": v(1580.08, 1372.13) * mm, "end": v(1573.76, 1284) * mm});
            skLineSegment(sketch, "E641", {"start": v(1573.76, 1284) * mm, "end": v(1570.15, 1290.13) * mm});
            skLineSegment(sketch, "E642", {"start": v(1570.15, 1290.13) * mm, "end": v(1567.36, 1252.51) * mm});
            skLineSegment(sketch, "E643", {"start": v(1567.36, 1252.51) * mm, "end": v(1565.28, 1208.78) * mm});
            skLineSegment(sketch, "E644", {"start": v(1565.28, 1208.78) * mm, "end": v(1564.57, 1265.63) * mm});
            skLineSegment(sketch, "E645", {"start": v(1564.57, 1265.63) * mm, "end": v(1556.45, 1267.38) * mm});
            skLineSegment(sketch, "E646", {"start": v(1556.45, 1267.38) * mm, "end": v(1553.36, 1222.77) * mm});
            skLineSegment(sketch, "E647", {"start": v(1553.36, 1222.77) * mm, "end": v(1550.28, 1319.87) * mm});
            skLineSegment(sketch, "E648", {"start": v(1550.28, 1319.87) * mm, "end": v(1546.37, 1406.47) * mm});
            skLineSegment(sketch, "E649", {"start": v(1546.37, 1406.47) * mm, "end": v(1542.6, 1431.84) * mm});
            skLineSegment(sketch, "E650", {"start": v(1542.6, 1431.84) * mm, "end": v(1539.55, 1472.95) * mm});
            skLineSegment(sketch, "E651", {"start": v(1539.55, 1472.95) * mm, "end": v(1536.74, 1488.7) * mm});
            skLineSegment(sketch, "E652", {"start": v(1536.74, 1488.7) * mm, "end": v(1536.3, 1468.87) * mm});
            skLineSegment(sketch, "E653", {"start": v(1536.3, 1468.87) * mm, "end": v(1532.66, 1447.87) * mm});
            skLineSegment(sketch, "E654", {"start": v(1532.66, 1447.87) * mm, "end": v(1524.95, 1379.35) * mm});
            skLineSegment(sketch, "E655", {"start": v(1524.95, 1379.35) * mm, "end": v(1517.66, 1312) * mm});
            skLineSegment(sketch, "E656", {"start": v(1517.66, 1312) * mm, "end": v(1514.63, 1284.88) * mm});
            skLineSegment(sketch, "E657", {"start": v(1514.63, 1284.88) * mm, "end": v(1508.12, 1255.14) * mm});
            skLineSegment(sketch, "E658", {"start": v(1508.12, 1255.14) * mm, "end": v(1500.47, 1242.9) * mm});
            skLineSegment(sketch, "E659", {"start": v(1500.47, 1242.9) * mm, "end": v(1497.38, 1208.78) * mm});
            skLineSegment(sketch, "E660", {"start": v(1497.38, 1208.78) * mm, "end": v(1494.3, 1260.39) * mm});
            skLineSegment(sketch, "E661", {"start": v(1494.3, 1260.39) * mm, "end": v(1486.32, 1283.42) * mm});
            skLineSegment(sketch, "E662", {"start": v(1486.32, 1283.42) * mm, "end": v(1480.76, 1242.89) * mm});
            skLineSegment(sketch, "E663", {"start": v(1480.76, 1242.89) * mm, "end": v(1475.73, 1235.6) * mm});
            skLineSegment(sketch, "E664", {"start": v(1475.73, 1235.6) * mm, "end": v(1472.89, 1261.26) * mm});
            skLineSegment(sketch, "E665", {"start": v(1472.89, 1261.26) * mm, "end": v(1470.05, 1234.14) * mm});
            skLineSegment(sketch, "E666", {"start": v(1470.05, 1234.14) * mm, "end": v(1465.89, 1175.54) * mm});
            skLineSegment(sketch, "E667", {"start": v(1465.89, 1175.54) * mm, "end": v(1461.98, 1164.17) * mm});
            skLineSegment(sketch, "E668", {"start": v(1461.98, 1164.17) * mm, "end": v(1461.56, 1152.8) * mm});
            skLineSegment(sketch, "E669", {"start": v(1461.56, 1152.8) * mm, "end": v(1458.9, 1163.3) * mm});
            skLineSegment(sketch, "E670", {"start": v(1458.9, 1163.3) * mm, "end": v(1455.8, 1216.36) * mm});
            skLineSegment(sketch, "E671", {"start": v(1455.8, 1216.36) * mm, "end": v(1451.98, 1260.1) * mm});
            skLineSegment(sketch, "E672", {"start": v(1451.98, 1260.1) * mm, "end": v(1446.16, 1388.43) * mm});
            skLineSegment(sketch, "E673", {"start": v(1446.16, 1388.43) * mm, "end": v(1438.2, 1517.63) * mm});
            skLineSegment(sketch, "E674", {"start": v(1438.2, 1517.63) * mm, "end": v(1430.08, 1523.43) * mm});
            skLineSegment(sketch, "E675", {"start": v(1430.08, 1523.43) * mm, "end": v(1427.45, 1519.3) * mm});
            skLineSegment(sketch, "E676", {"start": v(1427.45, 1519.3) * mm, "end": v(1423.9, 1511.44) * mm});
            skLineSegment(sketch, "E677", {"start": v(1423.9, 1511.44) * mm, "end": v(1420.16, 1505.31) * mm});
            skLineSegment(sketch, "E678", {"start": v(1420.16, 1505.31) * mm, "end": v(1416.9, 1506.19) * mm});
            skLineSegment(sketch, "E679", {"start": v(1416.9, 1506.19) * mm, "end": v(1413.65, 1507.06) * mm});
            skLineSegment(sketch, "E680", {"start": v(1413.65, 1507.06) * mm, "end": v(1409.9, 1500.94) * mm});
            skLineSegment(sketch, "E681", {"start": v(1409.9, 1500.94) * mm, "end": v(1406.35, 1494.82) * mm});
            skLineSegment(sketch, "E682", {"start": v(1406.35, 1494.82) * mm, "end": v(1403.28, 1493.46) * mm});
            skLineSegment(sketch, "E683", {"start": v(1403.28, 1493.46) * mm, "end": v(1398.35, 1493.46) * mm});
            skLineSegment(sketch, "E684", {"start": v(1398.35, 1493.46) * mm, "end": v(1392.93, 1493.74) * mm});
            skLineSegment(sketch, "E685", {"start": v(1392.93, 1493.74) * mm, "end": v(1388.29, 1485.2) * mm});
            skLineSegment(sketch, "E686", {"start": v(1388.29, 1485.2) * mm, "end": v(1381.04, 1477.78) * mm});
            skLineSegment(sketch, "E687", {"start": v(1381.04, 1477.78) * mm, "end": v(1374.86, 1524.8) * mm});
            skLineSegment(sketch, "E688", {"start": v(1374.86, 1524.8) * mm, "end": v(1367.12, 1574.32) * mm});
            skLineSegment(sketch, "E689", {"start": v(1367.12, 1574.32) * mm, "end": v(1357.42, 1536.56) * mm});
            skLineSegment(sketch, "E690", {"start": v(1357.42, 1536.56) * mm, "end": v(1350.19, 1529.8) * mm});
            skLineSegment(sketch, "E691", {"start": v(1350.19, 1529.8) * mm, "end": v(1346.15, 1526.3) * mm});
            skLineSegment(sketch, "E692", {"start": v(1346.15, 1526.3) * mm, "end": v(1335.58, 1531.56) * mm});
            skLineSegment(sketch, "E693", {"start": v(1335.58, 1531.56) * mm, "end": v(1334.3, 1544.68) * mm});
            skLineSegment(sketch, "E694", {"start": v(1334.3, 1544.68) * mm, "end": v(1331.42, 1529.8) * mm});
            skLineSegment(sketch, "E695", {"start": v(1331.42, 1529.8) * mm, "end": v(1325.48, 1514.94) * mm});
            skLineSegment(sketch, "E696", {"start": v(1325.48, 1514.94) * mm, "end": v(1322.43, 1500.94) * mm});
            skLineSegment(sketch, "E697", {"start": v(1322.43, 1500.94) * mm, "end": v(1310.85, 1493.07) * mm});
            skLineSegment(sketch, "E698", {"start": v(1310.85, 1493.07) * mm, "end": v(1308.57, 1483.44) * mm});
            skLineSegment(sketch, "E699", {"start": v(1308.57, 1483.44) * mm, "end": v(1306.12, 1472.07) * mm});
            skLineSegment(sketch, "E700", {"start": v(1306.12, 1472.07) * mm, "end": v(1299.79, 1476.45) * mm});
            skLineSegment(sketch, "E701", {"start": v(1299.79, 1476.45) * mm, "end": v(1292.92, 1488.7) * mm});
            skLineSegment(sketch, "E702", {"start": v(1292.92, 1488.7) * mm, "end": v(1287.28, 1500.94) * mm});
            skLineSegment(sketch, "E703", {"start": v(1287.28, 1500.94) * mm, "end": v(1283.7, 1528.06) * mm});
            skLineSegment(sketch, "E704", {"start": v(1283.7, 1528.06) * mm, "end": v(1277.2, 1556.05) * mm});
            skLineSegment(sketch, "E705", {"start": v(1277.2, 1556.05) * mm, "end": v(1269.55, 1552.55) * mm});
            skLineSegment(sketch, "E706", {"start": v(1269.55, 1552.55) * mm, "end": v(1266.48, 1548.32) * mm});
            skLineSegment(sketch, "E707", {"start": v(1266.48, 1548.32) * mm, "end": v(1259.88, 1533.16) * mm});
            skLineSegment(sketch, "E708", {"start": v(1259.88, 1533.16) * mm, "end": v(1255.95, 1522.8) * mm});
            skLineSegment(sketch, "E709", {"start": v(1255.95, 1522.8) * mm, "end": v(1253.79, 1515.94) * mm});
            skLineSegment(sketch, "E710", {"start": v(1253.79, 1515.94) * mm, "end": v(1241.96, 1489.27) * mm});
            skLineSegment(sketch, "E711", {"start": v(1241.96, 1489.27) * mm, "end": v(1234.96, 1471.93) * mm});
            skLineSegment(sketch, "E712", {"start": v(1234.96, 1471.93) * mm, "end": v(1227.34, 1434) * mm});
            skLineSegment(sketch, "E713", {"start": v(1227.34, 1434) * mm, "end": v(1224.46, 1418.71) * mm});
            skLineSegment(sketch, "E714", {"start": v(1224.46, 1418.71) * mm, "end": v(1222.2, 1443.2) * mm});
            skLineSegment(sketch, "E715", {"start": v(1222.2, 1443.2) * mm, "end": v(1221.58, 1423.38) * mm});
            skLineSegment(sketch, "E716", {"start": v(1221.58, 1423.38) * mm, "end": v(1216.59, 1402.1) * mm});
            skLineSegment(sketch, "E717", {"start": v(1216.59, 1402.1) * mm, "end": v(1210.2, 1367.7) * mm});
            skLineSegment(sketch, "E718", {"start": v(1210.2, 1367.7) * mm, "end": v(1207.58, 1398.6) * mm});
            skLineSegment(sketch, "E719", {"start": v(1207.58, 1398.6) * mm, "end": v(1204.32, 1462.45) * mm});
            skLineSegment(sketch, "E720", {"start": v(1204.32, 1462.45) * mm, "end": v(1192.97, 1415.27) * mm});
            skLineSegment(sketch, "E721", {"start": v(1192.97, 1415.27) * mm, "end": v(1189.47, 1395.97) * mm});
            skLineSegment(sketch, "E722", {"start": v(1189.47, 1395.97) * mm, "end": v(1185.5, 1365.36) * mm});
            skLineSegment(sketch, "E723", {"start": v(1185.5, 1365.36) * mm, "end": v(1185.01, 1334.74) * mm});
            skLineSegment(sketch, "E724", {"start": v(1185.01, 1334.74) * mm, "end": v(1181.94, 1369.73) * mm});
            skLineSegment(sketch, "E725", {"start": v(1181.94, 1369.73) * mm, "end": v(1175.42, 1405.88) * mm});
            skLineSegment(sketch, "E726", {"start": v(1175.42, 1405.88) * mm, "end": v(1171.92, 1419.88) * mm});
            skLineSegment(sketch, "E727", {"start": v(1171.92, 1419.88) * mm, "end": v(1168.48, 1437.96) * mm});
            skLineSegment(sketch, "E728", {"start": v(1168.48, 1437.96) * mm, "end": v(1165.03, 1417.84) * mm});
            skLineSegment(sketch, "E729", {"start": v(1165.03, 1417.84) * mm, "end": v(1161.97, 1392.47) * mm});
            skLineSegment(sketch, "E730", {"start": v(1161.97, 1392.47) * mm, "end": v(1156.67, 1332.12) * mm});
            skLineSegment(sketch, "E731", {"start": v(1156.67, 1332.12) * mm, "end": v(1147.56, 1203.53) * mm});
            skLineSegment(sketch, "E732", {"start": v(1147.56, 1203.53) * mm, "end": v(1142.74, 1235.9) * mm});
            skLineSegment(sketch, "E733", {"start": v(1142.74, 1235.9) * mm, "end": v(1136.97, 1269.43) * mm});
            skLineSegment(sketch, "E734", {"start": v(1136.97, 1269.43) * mm, "end": v(1133.14, 1363.9) * mm});
            skLineSegment(sketch, "E735", {"start": v(1133.14, 1363.9) * mm, "end": v(1129.99, 1448.46) * mm});
            skLineSegment(sketch, "E736", {"start": v(1129.99, 1448.46) * mm, "end": v(1126.84, 1428.34) * mm});
            skLineSegment(sketch, "E737", {"start": v(1126.84, 1428.34) * mm, "end": v(1121.34, 1416.96) * mm});
            skLineSegment(sketch, "E738", {"start": v(1121.34, 1416.96) * mm, "end": v(1115.11, 1370.6) * mm});
            skLineSegment(sketch, "E739", {"start": v(1115.11, 1370.6) * mm, "end": v(1114.02, 1324.24) * mm});
            skLineSegment(sketch, "E740", {"start": v(1114.02, 1324.24) * mm, "end": v(1113.26, 1372.35) * mm});
            skLineSegment(sketch, "E741", {"start": v(1113.26, 1372.35) * mm, "end": v(1109.24, 1420.46) * mm});
            skLineSegment(sketch, "E742", {"start": v(1109.24, 1420.46) * mm, "end": v(1104.47, 1412.6) * mm});
            skLineSegment(sketch, "E743", {"start": v(1104.47, 1412.6) * mm, "end": v(1102.07, 1423.96) * mm});
            skLineSegment(sketch, "E744", {"start": v(1102.07, 1423.96) * mm, "end": v(1099.59, 1437.08) * mm});
            skLineSegment(sketch, "E745", {"start": v(1099.59, 1437.08) * mm, "end": v(1091.26, 1438.83) * mm});
            skLineSegment(sketch, "E746", {"start": v(1091.26, 1438.83) * mm, "end": v(1088, 1439.7) * mm});
            skLineSegment(sketch, "E747", {"start": v(1088, 1439.7) * mm, "end": v(1084.75, 1440.87) * mm});
            skLineSegment(sketch, "E748", {"start": v(1084.75, 1440.87) * mm, "end": v(1080.13, 1447.6) * mm});
            skLineSegment(sketch, "E749", {"start": v(1080.13, 1447.6) * mm, "end": v(1073.8, 1413.19) * mm});
            skLineSegment(sketch, "E750", {"start": v(1073.8, 1413.19) * mm, "end": v(1071.18, 1402.1) * mm});
            skLineSegment(sketch, "E751", {"start": v(1071.18, 1402.1) * mm, "end": v(1062.58, 1407.34) * mm});
            skLineSegment(sketch, "E752", {"start": v(1062.58, 1407.34) * mm, "end": v(1060.64, 1416.1) * mm});
            skLineSegment(sketch, "E753", {"start": v(1060.64, 1416.1) * mm, "end": v(1054.76, 1441.46) * mm});
            skLineSegment(sketch, "E754", {"start": v(1054.76, 1441.46) * mm, "end": v(1049.17, 1435.33) * mm});
            skLineSegment(sketch, "E755", {"start": v(1049.17, 1435.33) * mm, "end": v(1046.01, 1437.96) * mm});
            skLineSegment(sketch, "E756", {"start": v(1046.01, 1437.96) * mm, "end": v(1042.86, 1435.33) * mm});
            skLineSegment(sketch, "E757", {"start": v(1042.86, 1435.33) * mm, "end": v(1039.46, 1423.96) * mm});
            skLineSegment(sketch, "E758", {"start": v(1039.46, 1423.96) * mm, "end": v(1034.21, 1333.86) * mm});
            skLineSegment(sketch, "E759", {"start": v(1034.21, 1333.86) * mm, "end": v(1029.9, 1228.9) * mm});
            skLineSegment(sketch, "E760", {"start": v(1029.9, 1228.9) * mm, "end": v(1020.97, 1223.65) * mm});
            skLineSegment(sketch, "E761", {"start": v(1020.97, 1223.65) * mm, "end": v(1018.02, 1215.77) * mm});
            skLineSegment(sketch, "E762", {"start": v(1018.02, 1215.77) * mm, "end": v(1015.62, 1198.28) * mm});
            skLineSegment(sketch, "E763", {"start": v(1015.62, 1198.28) * mm, "end": v(1015.07, 1221.9) * mm});
            skLineSegment(sketch, "E764", {"start": v(1015.07, 1221.9) * mm, "end": v(1011.03, 1245.52) * mm});
            skLineSegment(sketch, "E765", {"start": v(1011.03, 1245.52) * mm, "end": v(1006.9, 1305.87) * mm});
            skLineSegment(sketch, "E766", {"start": v(1006.9, 1305.87) * mm, "end": v(1006.28, 1366.23) * mm});
            skLineSegment(sketch, "E767", {"start": v(1006.28, 1366.23) * mm, "end": v(1003.84, 1303.25) * mm});
            skLineSegment(sketch, "E768", {"start": v(1003.84, 1303.25) * mm, "end": v(1000.97, 1175.04) * mm});
            skLineSegment(sketch, "E769", {"start": v(1000.97, 1175.04) * mm, "end": v(995.28, 1107.8) * mm});
            skLineSegment(sketch, "E770", {"start": v(995.28, 1107.8) * mm, "end": v(990.03, 1241.95) * mm});
            skLineSegment(sketch, "E771", {"start": v(990.03, 1241.95) * mm, "end": v(983.97, 1381.52) * mm});
            skLineSegment(sketch, "E772", {"start": v(983.97, 1381.52) * mm, "end": v(975.74, 1405.31) * mm});
            skLineSegment(sketch, "E773", {"start": v(975.74, 1405.31) * mm, "end": v(973.57, 1425.71) * mm});
            skLineSegment(sketch, "E774", {"start": v(973.57, 1425.71) * mm, "end": v(973.05, 1402.39) * mm});
            skLineSegment(sketch, "E775", {"start": v(973.05, 1402.39) * mm, "end": v(968.69, 1377.78) * mm});
            skLineSegment(sketch, "E776", {"start": v(968.69, 1377.78) * mm, "end": v(962.91, 1274.27) * mm});
            skLineSegment(sketch, "E777", {"start": v(962.91, 1274.27) * mm, "end": v(958.55, 1172.04) * mm});
            skLineSegment(sketch, "E778", {"start": v(958.55, 1172.04) * mm, "end": v(951.56, 1300.19) * mm});
            skLineSegment(sketch, "E779", {"start": v(951.56, 1300.19) * mm, "end": v(944.3, 1360.98) * mm});
            skLineSegment(sketch, "E780", {"start": v(944.3, 1360.98) * mm, "end": v(940.13, 1342.61) * mm});
            skLineSegment(sketch, "E781", {"start": v(940.13, 1342.61) * mm, "end": v(938.2, 1350.85) * mm});
            skLineSegment(sketch, "E782", {"start": v(938.2, 1350.85) * mm, "end": v(930.05, 1420.46) * mm});
            skLineSegment(sketch, "E783", {"start": v(930.05, 1420.46) * mm, "end": v(926.64, 1372.35) * mm});
            skLineSegment(sketch, "E784", {"start": v(926.64, 1372.35) * mm, "end": v(920.59, 1293.63) * mm});
            skLineSegment(sketch, "E785", {"start": v(920.59, 1293.63) * mm, "end": v(915.32, 1308.5) * mm});
            skLineSegment(sketch, "E786", {"start": v(915.32, 1308.5) * mm, "end": v(906.06, 1211.75) * mm});
            skLineSegment(sketch, "E787", {"start": v(906.06, 1211.75) * mm, "end": v(902.63, 1168.54) * mm});
            skLineSegment(sketch, "E788", {"start": v(902.63, 1168.54) * mm, "end": v(898.18, 1099.43) * mm});
            skLineSegment(sketch, "E789", {"start": v(898.18, 1099.43) * mm, "end": v(895.7, 1075.82) * mm});
            skLineSegment(sketch, "E790", {"start": v(89.57, 107.58) * mm, "end": v(89.3, 110.12) * mm});
            skLineSegment(sketch, "E791", {"start": v(89.3, 110.12) * mm, "end": v(88.84, 108.1) * mm});
            skLineSegment(sketch, "E792", {"start": v(88.84, 108.1) * mm, "end": v(88.5, 120.16) * mm});
            skLineSegment(sketch, "E793", {"start": v(88.5, 120.16) * mm, "end": v(88.16, 132.42) * mm});
            skLineSegment(sketch, "E794", {"start": v(88.16, 132.42) * mm, "end": v(87.8, 131.75) * mm});
            skLineSegment(sketch, "E795", {"start": v(87.8, 131.75) * mm, "end": v(87.5, 130.85) * mm});
            skLineSegment(sketch, "E796", {"start": v(87.5, 130.85) * mm, "end": v(86.87, 133.91) * mm});
            skLineSegment(sketch, "E797", {"start": v(86.87, 133.91) * mm, "end": v(86.52, 136.97) * mm});
            skLineSegment(sketch, "E798", {"start": v(86.52, 136.97) * mm, "end": v(86.46, 134.79) * mm});
            skLineSegment(sketch, "E799", {"start": v(86.46, 134.79) * mm, "end": v(85.6, 133.39) * mm});
            skLineSegment(sketch, "E800", {"start": v(85.6, 133.39) * mm, "end": v(85.34, 131.72) * mm});
            skLineSegment(sketch, "E801", {"start": v(85.34, 131.72) * mm, "end": v(85.1, 130.94) * mm});
            skLineSegment(sketch, "E802", {"start": v(85.1, 130.94) * mm, "end": v(84.64, 132.6) * mm});
            skLineSegment(sketch, "E803", {"start": v(84.64, 132.6) * mm, "end": v(84.27, 126.74) * mm});
            skLineSegment(sketch, "E804", {"start": v(84.27, 126.74) * mm, "end": v(83.96, 121.75) * mm});
            skLineSegment(sketch, "E805", {"start": v(83.96, 121.75) * mm, "end": v(83.64, 124.64) * mm});
            skLineSegment(sketch, "E806", {"start": v(83.64, 124.64) * mm, "end": v(83.3, 126.65) * mm});
            skLineSegment(sketch, "E807", {"start": v(83.3, 126.65) * mm, "end": v(82.5, 116.5) * mm});
            skLineSegment(sketch, "E808", {"start": v(82.5, 116.5) * mm, "end": v(82.3, 113.18) * mm});
            skLineSegment(sketch, "E809", {"start": v(82.3, 113.18) * mm, "end": v(81.8, 114.44) * mm});
            skLineSegment(sketch, "E810", {"start": v(81.8, 114.44) * mm, "end": v(81.19, 117.59) * mm});
            skLineSegment(sketch, "E811", {"start": v(81.19, 117.59) * mm, "end": v(80.86, 118.7) * mm});
            skLineSegment(sketch, "E812", {"start": v(80.86, 118.7) * mm, "end": v(80.02, 119.92) * mm});
            skLineSegment(sketch, "E813", {"start": v(80.02, 119.92) * mm, "end": v(79.8, 117.9) * mm});
            skLineSegment(sketch, "E814", {"start": v(79.8, 117.9) * mm, "end": v(79.52, 113.44) * mm});
            skLineSegment(sketch, "E815", {"start": v(79.52, 113.44) * mm, "end": v(78.62, 109.94) * mm});
            skLineSegment(sketch, "E816", {"start": v(78.62, 109.94) * mm, "end": v(78.5, 105.83) * mm});
            skLineSegment(sketch, "E817", {"start": v(78.5, 105.83) * mm, "end": v(78.43, 111) * mm});
            skLineSegment(sketch, "E818", {"start": v(78.43, 111) * mm, "end": v(77.6, 111.87) * mm});
            skLineSegment(sketch, "E819", {"start": v(77.6, 111.87) * mm, "end": v(77.3, 110.2) * mm});
            skLineSegment(sketch, "E820", {"start": v(77.3, 110.2) * mm, "end": v(77, 115.9) * mm});
            skLineSegment(sketch, "E821", {"start": v(77, 115.9) * mm, "end": v(76.64, 118.95) * mm});
            skLineSegment(sketch, "E822", {"start": v(76.64, 118.95) * mm, "end": v(76.2, 124.76) * mm});
            skLineSegment(sketch, "E823", {"start": v(76.2, 124.76) * mm, "end": v(75.4, 131.06) * mm});
            skLineSegment(sketch, "E824", {"start": v(75.4, 131.06) * mm, "end": v(74.49, 133.22) * mm});
            skLineSegment(sketch, "E825", {"start": v(74.49, 133.22) * mm, "end": v(74.2, 133.56) * mm});
            skLineSegment(sketch, "E826", {"start": v(74.2, 133.56) * mm, "end": v(73.86, 132.25) * mm});
            skLineSegment(sketch, "E827", {"start": v(73.86, 132.25) * mm, "end": v(73.34, 138.8) * mm});
            skLineSegment(sketch, "E828", {"start": v(73.34, 138.8) * mm, "end": v(72.37, 148.34) * mm});
            skLineSegment(sketch, "E829", {"start": v(72.37, 148.34) * mm, "end": v(72.06, 147.3) * mm});
            skLineSegment(sketch, "E830", {"start": v(72.06, 147.3) * mm, "end": v(71.87, 146.25) * mm});
            skLineSegment(sketch, "E831", {"start": v(71.87, 146.25) * mm, "end": v(70.16, 148.26) * mm});
            skLineSegment(sketch, "E832", {"start": v(70.16, 148.26) * mm, "end": v(69.59, 149.04) * mm});
            skLineSegment(sketch, "E833", {"start": v(69.59, 149.04) * mm, "end": v(69.23, 149.83) * mm});
            skLineSegment(sketch, "E834", {"start": v(69.23, 149.83) * mm, "end": v(68.75, 148.6) * mm});
            skLineSegment(sketch, "E835", {"start": v(68.75, 148.6) * mm, "end": v(67.86, 148.72) * mm});
            skLineSegment(sketch, "E836", {"start": v(67.86, 148.72) * mm, "end": v(67.51, 149.92) * mm});
            skLineSegment(sketch, "E837", {"start": v(67.51, 149.92) * mm, "end": v(67.16, 150.6) * mm});
            skLineSegment(sketch, "E838", {"start": v(67.16, 150.6) * mm, "end": v(66.81, 151.5) * mm});
            skLineSegment(sketch, "E839", {"start": v(66.81, 151.5) * mm, "end": v(66.46, 154.34) * mm});
            skLineSegment(sketch, "E840", {"start": v(66.46, 154.34) * mm, "end": v(66.46, 157.2) * mm});
            skLineSegment(sketch, "E841", {"start": v(66.46, 157.2) * mm, "end": v(65.41, 156.1) * mm});
            skLineSegment(sketch, "E842", {"start": v(65.41, 156.1) * mm, "end": v(64.36, 153.42) * mm});
            skLineSegment(sketch, "E843", {"start": v(64.36, 153.42) * mm, "end": v(64.01, 151.84) * mm});
            skLineSegment(sketch, "E844", {"start": v(64.01, 151.84) * mm, "end": v(63.64, 150.36) * mm});
            skLineSegment(sketch, "E845", {"start": v(63.64, 150.36) * mm, "end": v(62.99, 147.9) * mm});
            skLineSegment(sketch, "E846", {"start": v(62.99, 147.9) * mm, "end": v(62.26, 147.35) * mm});
            skLineSegment(sketch, "E847", {"start": v(62.26, 147.35) * mm, "end": v(61.59, 145.57) * mm});
            skLineSegment(sketch, "E848", {"start": v(61.59, 145.57) * mm, "end": v(60.91, 144.8) * mm});
            skLineSegment(sketch, "E849", {"start": v(60.91, 144.8) * mm, "end": v(60.77, 146.13) * mm});
            skLineSegment(sketch, "E850", {"start": v(60.77, 146.13) * mm, "end": v(60.63, 147.47) * mm});
            skLineSegment(sketch, "E851", {"start": v(60.63, 147.47) * mm, "end": v(60.57, 145.98) * mm});
            skLineSegment(sketch, "E852", {"start": v(60.57, 145.98) * mm, "end": v(59.81, 145.17) * mm});
            skLineSegment(sketch, "E853", {"start": v(59.81, 145.17) * mm, "end": v(59.46, 146.07) * mm});
            skLineSegment(sketch, "E854", {"start": v(59.46, 146.07) * mm, "end": v(59.12, 145.91) * mm});
            skLineSegment(sketch, "E855", {"start": v(59.12, 145.91) * mm, "end": v(58, 145.73) * mm});
            skLineSegment(sketch, "E856", {"start": v(58, 145.73) * mm, "end": v(56.32, 147.32) * mm});
            skLineSegment(sketch, "E857", {"start": v(56.32, 147.32) * mm, "end": v(56.02, 148.34) * mm});
            skLineSegment(sketch, "E858", {"start": v(56.02, 148.34) * mm, "end": v(55.48, 151.74) * mm});
            skLineSegment(sketch, "E859", {"start": v(55.48, 151.74) * mm, "end": v(54.57, 156.74) * mm});
            skLineSegment(sketch, "E860", {"start": v(54.57, 156.74) * mm, "end": v(53.64, 150.52) * mm});
            skLineSegment(sketch, "E861", {"start": v(53.64, 150.52) * mm, "end": v(53.4, 145.86) * mm});
            skLineSegment(sketch, "E862", {"start": v(53.4, 145.86) * mm, "end": v(52.43, 146.08) * mm});
            skLineSegment(sketch, "E863", {"start": v(52.43, 146.08) * mm, "end": v(50.9, 143.4) * mm});
            skLineSegment(sketch, "E864", {"start": v(50.9, 143.4) * mm, "end": v(49.75, 141.94) * mm});
            skLineSegment(sketch, "E865", {"start": v(49.75, 141.94) * mm, "end": v(48.27, 143.7) * mm});
            skLineSegment(sketch, "E866", {"start": v(48.27, 143.7) * mm, "end": v(47.74, 144.62) * mm});
            skLineSegment(sketch, "E867", {"start": v(47.74, 144.62) * mm, "end": v(47.22, 145.86) * mm});
            skLineSegment(sketch, "E868", {"start": v(47.22, 145.86) * mm, "end": v(46.87, 147.3) * mm});
            skLineSegment(sketch, "E869", {"start": v(46.87, 147.3) * mm, "end": v(46.52, 148.17) * mm});
            skLineSegment(sketch, "E870", {"start": v(46.52, 148.17) * mm, "end": v(45.8, 148.26) * mm});
            skLineSegment(sketch, "E871", {"start": v(45.8, 148.26) * mm, "end": v(45.47, 148.17) * mm});
            skLineSegment(sketch, "E872", {"start": v(45.47, 148.17) * mm, "end": v(45.14, 147.38) * mm});
            skLineSegment(sketch, "E873", {"start": v(45.14, 147.38) * mm, "end": v(44.6, 145.9) * mm});
            skLineSegment(sketch, "E874", {"start": v(44.6, 145.9) * mm, "end": v(44.07, 147.82) * mm});
            skLineSegment(sketch, "E875", {"start": v(44.07, 147.82) * mm, "end": v(43.72, 149.74) * mm});
            skLineSegment(sketch, "E876", {"start": v(43.72, 149.74) * mm, "end": v(43.37, 148.54) * mm});
            skLineSegment(sketch, "E877", {"start": v(43.37, 148.54) * mm, "end": v(43.02, 147.12) * mm});
            skLineSegment(sketch, "E878", {"start": v(43.02, 147.12) * mm, "end": v(42.67, 146.22) * mm});
            skLineSegment(sketch, "E879", {"start": v(42.67, 146.22) * mm, "end": v(41.92, 146.5) * mm});
            skLineSegment(sketch, "E880", {"start": v(41.92, 146.5) * mm, "end": v(41.62, 145.72) * mm});
            skLineSegment(sketch, "E881", {"start": v(41.62, 145.72) * mm, "end": v(41.33, 147.03) * mm});
            skLineSegment(sketch, "E882", {"start": v(41.33, 147.03) * mm, "end": v(40.57, 148.08) * mm});
            skLineSegment(sketch, "E883", {"start": v(40.57, 148.08) * mm, "end": v(39.7, 142.4) * mm});
            skLineSegment(sketch, "E884", {"start": v(39.7, 142.4) * mm, "end": v(39.04, 137.76) * mm});
            skLineSegment(sketch, "E885", {"start": v(39.04, 137.76) * mm, "end": v(38.07, 127.35) * mm});
            skLineSegment(sketch, "E886", {"start": v(38.07, 127.35) * mm, "end": v(37.72, 129.36) * mm});
            skLineSegment(sketch, "E887", {"start": v(37.72, 129.36) * mm, "end": v(37.68, 131.37) * mm});
            skLineSegment(sketch, "E888", {"start": v(37.68, 131.37) * mm, "end": v(37.4, 129.63) * mm});
            skLineSegment(sketch, "E889", {"start": v(37.4, 129.63) * mm, "end": v(37.1, 125.9) * mm});
            skLineSegment(sketch, "E890", {"start": v(37.1, 125.9) * mm, "end": v(36.74, 123.8) * mm});
            skLineSegment(sketch, "E891", {"start": v(36.74, 123.8) * mm, "end": v(36.17, 117.64) * mm});
            skLineSegment(sketch, "E892", {"start": v(36.17, 117.64) * mm, "end": v(35.45, 111.6) * mm});
            skLineSegment(sketch, "E893", {"start": v(35.45, 111.6) * mm, "end": v(34.93, 109.07) * mm});
            skLineSegment(sketch, "E894", {"start": v(34.93, 109.07) * mm, "end": v(34.62, 107.76) * mm});
            skLineSegment(sketch, "E895", {"start": v(34.62, 107.76) * mm, "end": v(34.36, 108.98) * mm});
            skLineSegment(sketch, "E896", {"start": v(34.36, 108.98) * mm, "end": v(34.32, 107.84) * mm});
            skLineSegment(sketch, "E897", {"start": v(34.32, 107.84) * mm, "end": v(33.98, 106.7) * mm});
            skLineSegment(sketch, "E898", {"start": v(33.98, 106.7) * mm, "end": v(33, 128.66) * mm});
            skLineSegment(sketch, "E899", {"start": v(33, 128.66) * mm, "end": v(32.47, 137.85) * mm});
            skLineSegment(sketch, "E900", {"start": v(32.47, 137.85) * mm, "end": v(32.17, 139.23) * mm});
            skLineSegment(sketch, "E901", {"start": v(32.17, 139.23) * mm, "end": v(30.96, 145.9) * mm});
            skLineSegment(sketch, "E902", {"start": v(30.96, 145.9) * mm, "end": v(30.08, 153.33) * mm});
            skLineSegment(sketch, "E903", {"start": v(30.08, 153.33) * mm, "end": v(29.72, 156.04) * mm});
            skLineSegment(sketch, "E904", {"start": v(29.72, 156.04) * mm, "end": v(29.34, 154.73) * mm});
            skLineSegment(sketch, "E905", {"start": v(29.34, 154.73) * mm, "end": v(29.02, 152.54) * mm});
            skLineSegment(sketch, "E906", {"start": v(29.02, 152.54) * mm, "end": v(28.7, 152.8) * mm});
            skLineSegment(sketch, "E907", {"start": v(28.7, 152.8) * mm, "end": v(27.81, 151.34) * mm});
            skLineSegment(sketch, "E908", {"start": v(27.81, 151.34) * mm, "end": v(27.07, 148.93) * mm});
            skLineSegment(sketch, "E909", {"start": v(27.07, 148.93) * mm, "end": v(26.5, 146.9) * mm});
            skLineSegment(sketch, "E910", {"start": v(26.5, 146.9) * mm, "end": v(26.44, 144.67) * mm});
            skLineSegment(sketch, "E911", {"start": v(26.44, 144.67) * mm, "end": v(26.32, 146.68) * mm});
            skLineSegment(sketch, "E912", {"start": v(26.32, 146.68) * mm, "end": v(25.43, 147.38) * mm});
            skLineSegment(sketch, "E913", {"start": v(25.43, 147.38) * mm, "end": v(25.23, 147.64) * mm});
            skLineSegment(sketch, "E914", {"start": v(25.23, 147.64) * mm, "end": v(24.84, 148.7) * mm});
            skLineSegment(sketch, "E915", {"start": v(24.84, 148.7) * mm, "end": v(23.83, 151.33) * mm});
            skLineSegment(sketch, "E916", {"start": v(23.83, 151.33) * mm, "end": v(23.47, 148.08) * mm});
            skLineSegment(sketch, "E917", {"start": v(23.47, 148.08) * mm, "end": v(23.08, 142.05) * mm});
            skLineSegment(sketch, "E918", {"start": v(23.08, 142.05) * mm, "end": v(22.73, 137.89) * mm});
            skLineSegment(sketch, "E919", {"start": v(22.73, 137.89) * mm, "end": v(21.66, 121.11) * mm});
            skLineSegment(sketch, "E920", {"start": v(21.66, 121.11) * mm, "end": v(21.33, 119.82) * mm});
            skLineSegment(sketch, "E921", {"start": v(21.33, 119.82) * mm, "end": v(20.37, 118.55) * mm});
            skLineSegment(sketch, "E922", {"start": v(20.37, 118.55) * mm, "end": v(19.23, 147.56) * mm});
            skLineSegment(sketch, "E923", {"start": v(19.23, 147.56) * mm, "end": v(18.88, 154.3) * mm});
            skLineSegment(sketch, "E924", {"start": v(18.88, 154.3) * mm, "end": v(18.47, 155.08) * mm});
            skLineSegment(sketch, "E925", {"start": v(18.47, 155.08) * mm, "end": v(18.18, 154.3) * mm});
            skLineSegment(sketch, "E926", {"start": v(18.18, 154.3) * mm, "end": v(17.93, 152.72) * mm});
            skLineSegment(sketch, "E927", {"start": v(17.93, 152.72) * mm, "end": v(17.88, 154.73) * mm});
            skLineSegment(sketch, "E928", {"start": v(17.88, 154.73) * mm, "end": v(17.1, 155.6) * mm});
            skLineSegment(sketch, "E929", {"start": v(17.1, 155.6) * mm, "end": v(16.15, 134.08) * mm});
            skLineSegment(sketch, "E930", {"start": v(16.15, 134.08) * mm, "end": v(15.68, 130.56) * mm});
            skLineSegment(sketch, "E931", {"start": v(15.68, 130.56) * mm, "end": v(15.38, 128.4) * mm});
            skLineSegment(sketch, "E932", {"start": v(15.38, 128.4) * mm, "end": v(15.12, 129.63) * mm});
            skLineSegment(sketch, "E933", {"start": v(15.12, 129.63) * mm, "end": v(15.07, 128.14) * mm});
            skLineSegment(sketch, "E934", {"start": v(15.07, 128.14) * mm, "end": v(14.68, 126.65) * mm});
            skLineSegment(sketch, "E935", {"start": v(14.68, 126.65) * mm, "end": v(14.3, 124.81) * mm});
            skLineSegment(sketch, "E936", {"start": v(14.3, 124.81) * mm, "end": v(13.98, 123.85) * mm});
            skLineSegment(sketch, "E937", {"start": v(13.98, 123.85) * mm, "end": v(13.66, 130.59) * mm});
            skLineSegment(sketch, "E938", {"start": v(13.66, 130.59) * mm, "end": v(13.28, 136.45) * mm});
            skLineSegment(sketch, "E939", {"start": v(13.28, 136.45) * mm, "end": v(12.9, 141.78) * mm});
            skLineSegment(sketch, "E940", {"start": v(12.9, 141.78) * mm, "end": v(12.28, 149.83) * mm});
            skLineSegment(sketch, "E941", {"start": v(12.28, 149.83) * mm, "end": v(11.88, 149.04) * mm});
            skLineSegment(sketch, "E942", {"start": v(11.88, 149.04) * mm, "end": v(11.53, 148.2) * mm});
            skLineSegment(sketch, "E943", {"start": v(11.53, 148.2) * mm, "end": v(11.18, 147.12) * mm});
            skLineSegment(sketch, "E944", {"start": v(11.18, 147.12) * mm, "end": v(10.83, 145.03) * mm});
            skLineSegment(sketch, "E945", {"start": v(10.83, 145.03) * mm, "end": v(10.42, 143.02) * mm});
            skLineSegment(sketch, "E946", {"start": v(10.42, 143.02) * mm, "end": v(9.78, 139.4) * mm});
            skLineSegment(sketch, "E947", {"start": v(9.78, 139.4) * mm, "end": v(9.48, 137.59) * mm});
            skLineSegment(sketch, "E948", {"start": v(9.48, 137.59) * mm, "end": v(8.73, 136.19) * mm});
            skLineSegment(sketch, "E949", {"start": v(8.73, 136.19) * mm, "end": v(7.98, 129.45) * mm});
            skLineSegment(sketch, "E950", {"start": v(7.98, 129.45) * mm, "end": v(7.64, 130.41) * mm});
            skLineSegment(sketch, "E951", {"start": v(7.64, 130.41) * mm, "end": v(7.6, 131.37) * mm});
            skLineSegment(sketch, "E952", {"start": v(7.6, 131.37) * mm, "end": v(7.33, 130.32) * mm});
            skLineSegment(sketch, "E953", {"start": v(7.33, 130.32) * mm, "end": v(7.02, 138.98) * mm});
            skLineSegment(sketch, "E954", {"start": v(7.02, 138.98) * mm, "end": v(6.63, 148.7) * mm});
            skLineSegment(sketch, "E955", {"start": v(6.63, 148.7) * mm, "end": v(6.28, 151.69) * mm});
            skLineSegment(sketch, "E956", {"start": v(6.28, 151.69) * mm, "end": v(5.93, 154.47) * mm});
            skLineSegment(sketch, "E957", {"start": v(5.93, 154.47) * mm, "end": v(5.58, 153.6) * mm});
            skLineSegment(sketch, "E958", {"start": v(5.58, 153.6) * mm, "end": v(5.18, 152.82) * mm});
            skLineSegment(sketch, "E959", {"start": v(5.18, 152.82) * mm, "end": v(4.53, 150.43) * mm});
            skLineSegment(sketch, "E960", {"start": v(4.53, 150.43) * mm, "end": v(4.28, 148.17) * mm});
            skLineSegment(sketch, "E961", {"start": v(4.28, 148.17) * mm, "end": v(4.23, 150.36) * mm});
            skLineSegment(sketch, "E962", {"start": v(4.23, 150.36) * mm, "end": v(3.83, 152.54) * mm});
            skLineSegment(sketch, "E963", {"start": v(3.83, 152.54) * mm, "end": v(3.48, 155) * mm});
            skLineSegment(sketch, "E964", {"start": v(3.48, 155) * mm, "end": v(3.48, 157.44) * mm});
            skLineSegment(sketch, "E965", {"start": v(3.48, 157.44) * mm, "end": v(1.9, 157.44) * mm});
            skLineSegment(sketch, "E966", {"start": v(1.9, 157.44) * mm, "end": v(0.33, 157.96) * mm});
            skLineSegment(sketch, "E967", {"start": v(0.33, 157.96) * mm, "end": v(1.9, 158.26) * mm});
            skLineSegment(sketch, "E968", {"start": v(1.9, 158.26) * mm, "end": v(3.48, 158.05) * mm});
            skLineSegment(sketch, "E969", {"start": v(3.48, 158.05) * mm, "end": v(3.48, 159.5) * mm});
            skLineSegment(sketch, "E970", {"start": v(3.48, 159.5) * mm, "end": v(3.83, 160.94) * mm});
            skLineSegment(sketch, "E971", {"start": v(3.83, 160.94) * mm, "end": v(4.2, 161.9) * mm});
            skLineSegment(sketch, "E972", {"start": v(4.2, 161.9) * mm, "end": v(4.41, 162.43) * mm});
            skLineSegment(sketch, "E973", {"start": v(4.41, 162.43) * mm, "end": v(5.09, 162) * mm});
            skLineSegment(sketch, "E974", {"start": v(5.09, 162) * mm, "end": v(5.58, 161.44) * mm});
            skLineSegment(sketch, "E975", {"start": v(5.58, 161.44) * mm, "end": v(5.93, 161.12) * mm});
            skLineSegment(sketch, "E976", {"start": v(5.93, 161.12) * mm, "end": v(6.28, 162.01) * mm});
            skLineSegment(sketch, "E977", {"start": v(6.28, 162.01) * mm, "end": v(6.63, 162.7) * mm});
            skLineSegment(sketch, "E978", {"start": v(6.63, 162.7) * mm, "end": v(6.98, 168.9) * mm});
            skLineSegment(sketch, "E979", {"start": v(6.98, 168.9) * mm, "end": v(7.88, 179.8) * mm});
            skLineSegment(sketch, "E980", {"start": v(7.88, 179.8) * mm, "end": v(8.65, 175.3) * mm});
            skLineSegment(sketch, "E981", {"start": v(8.65, 175.3) * mm, "end": v(9.52, 172.75) * mm});
            skLineSegment(sketch, "E982", {"start": v(9.52, 172.75) * mm, "end": v(9.72, 171.89) * mm});
            skLineSegment(sketch, "E983", {"start": v(9.72, 171.89) * mm, "end": v(10.3, 169.56) * mm});
            skLineSegment(sketch, "E984", {"start": v(10.3, 169.56) * mm, "end": v(10.83, 168.32) * mm});
            skLineSegment(sketch, "E985", {"start": v(10.83, 168.32) * mm, "end": v(12.65, 165.25) * mm});
            skLineSegment(sketch, "E986", {"start": v(12.65, 165.25) * mm, "end": v(12.92, 169.43) * mm});
            skLineSegment(sketch, "E987", {"start": v(12.92, 169.43) * mm, "end": v(13.28, 173.19) * mm});
            skLineSegment(sketch, "E988", {"start": v(13.28, 173.19) * mm, "end": v(13.65, 174.5) * mm});
            skLineSegment(sketch, "E989", {"start": v(13.65, 174.5) * mm, "end": v(13.96, 177.21) * mm});
            skLineSegment(sketch, "E990", {"start": v(13.96, 177.21) * mm, "end": v(14.25, 178.61) * mm});
            skLineSegment(sketch, "E991", {"start": v(14.25, 178.61) * mm, "end": v(14.29, 177.12) * mm});
            skLineSegment(sketch, "E992", {"start": v(14.29, 177.12) * mm, "end": v(14.68, 175.64) * mm});
            skLineSegment(sketch, "E993", {"start": v(14.68, 175.64) * mm, "end": v(15.06, 174.85) * mm});
            skLineSegment(sketch, "E994", {"start": v(15.06, 174.85) * mm, "end": v(15.38, 174.94) * mm});
            skLineSegment(sketch, "E995", {"start": v(15.38, 174.94) * mm, "end": v(15.7, 174.15) * mm});
            skLineSegment(sketch, "E996", {"start": v(15.7, 174.15) * mm, "end": v(16.25, 172.49) * mm});
            skLineSegment(sketch, "E997", {"start": v(16.25, 172.49) * mm, "end": v(16.78, 167.63) * mm});
            skLineSegment(sketch, "E998", {"start": v(16.78, 167.63) * mm, "end": v(17, 161.68) * mm});
            skLineSegment(sketch, "E999", {"start": v(17, 161.68) * mm, "end": v(17.9, 165.23) * mm});
            skLineSegment(sketch, "E1000", {"start": v(17.9, 165.23) * mm, "end": v(17.97, 169.86) * mm});
            skLineSegment(sketch, "E1001", {"start": v(17.97, 169.86) * mm, "end": v(18.16, 164.64) * mm});
            skLineSegment(sketch, "E1002", {"start": v(18.16, 164.64) * mm, "end": v(18.77, 159.29) * mm});
            skLineSegment(sketch, "E1003", {"start": v(18.77, 159.29) * mm, "end": v(19.36, 165.38) * mm});
            skLineSegment(sketch, "E1004", {"start": v(19.36, 165.38) * mm, "end": v(20.35, 176.38) * mm});
            skLineSegment(sketch, "E1005", {"start": v(20.35, 176.38) * mm, "end": v(20.88, 178.2) * mm});
            skLineSegment(sketch, "E1006", {"start": v(20.88, 178.2) * mm, "end": v(22.73, 168.08) * mm});
            skLineSegment(sketch, "E1007", {"start": v(22.73, 168.08) * mm, "end": v(23.2, 163.9) * mm});
            skLineSegment(sketch, "E1008", {"start": v(23.2, 163.9) * mm, "end": v(23.9, 165.03) * mm});
            skLineSegment(sketch, "E1009", {"start": v(23.9, 165.03) * mm, "end": v(24.13, 167.81) * mm});
            skLineSegment(sketch, "E1010", {"start": v(24.13, 167.81) * mm, "end": v(24.48, 168.99) * mm});
            skLineSegment(sketch, "E1011", {"start": v(24.48, 168.99) * mm, "end": v(24.83, 167.94) * mm});
            skLineSegment(sketch, "E1012", {"start": v(24.83, 167.94) * mm, "end": v(25.18, 166.89) * mm});
            skLineSegment(sketch, "E1013", {"start": v(25.18, 166.89) * mm, "end": v(25.53, 167.59) * mm});
            skLineSegment(sketch, "E1014", {"start": v(25.53, 167.59) * mm, "end": v(25.84, 168.29) * mm});
            skLineSegment(sketch, "E1015", {"start": v(25.84, 168.29) * mm, "end": v(26.57, 165.99) * mm});
            skLineSegment(sketch, "E1016", {"start": v(26.57, 165.99) * mm, "end": v(27.35, 165.93) * mm});
            skLineSegment(sketch, "E1017", {"start": v(27.35, 165.93) * mm, "end": v(27.77, 164.96) * mm});
            skLineSegment(sketch, "E1018", {"start": v(27.77, 164.96) * mm, "end": v(28.43, 162.63) * mm});
            skLineSegment(sketch, "E1019", {"start": v(28.43, 162.63) * mm, "end": v(29.04, 160.88) * mm});
            skLineSegment(sketch, "E1020", {"start": v(29.04, 160.88) * mm, "end": v(29.29, 159.37) * mm});
            skLineSegment(sketch, "E1021", {"start": v(29.29, 159.37) * mm, "end": v(29.33, 160.85) * mm});
            skLineSegment(sketch, "E1022", {"start": v(29.33, 160.85) * mm, "end": v(29.68, 162.34) * mm});
            skLineSegment(sketch, "E1023", {"start": v(29.68, 162.34) * mm, "end": v(30.26, 165.05) * mm});
            skLineSegment(sketch, "E1024", {"start": v(30.26, 165.05) * mm, "end": v(30.7, 167.24) * mm});
            skLineSegment(sketch, "E1025", {"start": v(30.7, 167.24) * mm, "end": v(31.26, 166.46) * mm});
            skLineSegment(sketch, "E1026", {"start": v(31.26, 166.46) * mm, "end": v(32.13, 169.57) * mm});
            skLineSegment(sketch, "E1027", {"start": v(32.13, 169.57) * mm, "end": v(32.53, 171.15) * mm});
            skLineSegment(sketch, "E1028", {"start": v(32.53, 171.15) * mm, "end": v(33.1, 177.97) * mm});
            skLineSegment(sketch, "E1029", {"start": v(33.1, 177.97) * mm, "end": v(33.78, 184.5) * mm});
            skLineSegment(sketch, "E1030", {"start": v(33.78, 184.5) * mm, "end": v(34.74, 188.4) * mm});
            skLineSegment(sketch, "E1031", {"start": v(34.74, 188.4) * mm, "end": v(34.92, 187.82) * mm});
            skLineSegment(sketch, "E1032", {"start": v(34.92, 187.82) * mm, "end": v(35.36, 186.06) * mm});
            skLineSegment(sketch, "E1033", {"start": v(35.36, 186.06) * mm, "end": v(36.1, 181.22) * mm});
            skLineSegment(sketch, "E1034", {"start": v(36.1, 181.22) * mm, "end": v(36.76, 176.4) * mm});
            skLineSegment(sketch, "E1035", {"start": v(36.76, 176.4) * mm, "end": v(37.07, 175.43) * mm});
            skLineSegment(sketch, "E1036", {"start": v(37.07, 175.43) * mm, "end": v(37.42, 174.59) * mm});
            skLineSegment(sketch, "E1037", {"start": v(37.42, 174.59) * mm, "end": v(37.77, 175.5) * mm});
            skLineSegment(sketch, "E1038", {"start": v(37.77, 175.5) * mm, "end": v(38.71, 175.43) * mm});
            skLineSegment(sketch, "E1039", {"start": v(38.71, 175.43) * mm, "end": v(39.68, 170.86) * mm});
            skLineSegment(sketch, "E1040", {"start": v(39.68, 170.86) * mm, "end": v(40.57, 167.5) * mm});
            skLineSegment(sketch, "E1041", {"start": v(40.57, 167.5) * mm, "end": v(40.92, 166.54) * mm});
            skLineSegment(sketch, "E1042", {"start": v(40.92, 166.54) * mm, "end": v(41.27, 168.13) * mm});
            skLineSegment(sketch, "E1043", {"start": v(41.27, 168.13) * mm, "end": v(41.62, 169.51) * mm});
            skLineSegment(sketch, "E1044", {"start": v(41.62, 169.51) * mm, "end": v(41.97, 167.04) * mm});
            skLineSegment(sketch, "E1045", {"start": v(41.97, 167.04) * mm, "end": v(42.73, 166.45) * mm});
            skLineSegment(sketch, "E1046", {"start": v(42.73, 166.45) * mm, "end": v(43.02, 165.84) * mm});
            skLineSegment(sketch, "E1047", {"start": v(43.02, 165.84) * mm, "end": v(43.3, 165.26) * mm});
            skLineSegment(sketch, "E1048", {"start": v(43.3, 165.26) * mm, "end": v(43.8, 166.8) * mm});
            skLineSegment(sketch, "E1049", {"start": v(43.8, 166.8) * mm, "end": v(44.36, 165.88) * mm});
            skLineSegment(sketch, "E1050", {"start": v(44.36, 165.88) * mm, "end": v(45.51, 166.57) * mm});
            skLineSegment(sketch, "E1051", {"start": v(45.51, 166.57) * mm, "end": v(45.73, 167.76) * mm});
            skLineSegment(sketch, "E1052", {"start": v(45.73, 167.76) * mm, "end": v(45.77, 166.63) * mm});
            skLineSegment(sketch, "E1053", {"start": v(45.77, 166.63) * mm, "end": v(47.02, 166.71) * mm});
            skLineSegment(sketch, "E1054", {"start": v(47.02, 166.71) * mm, "end": v(47.57, 167.94) * mm});
            skLineSegment(sketch, "E1055", {"start": v(47.57, 167.94) * mm, "end": v(48.12, 169.25) * mm});
            skLineSegment(sketch, "E1056", {"start": v(48.12, 169.25) * mm, "end": v(49.01, 171.19) * mm});
            skLineSegment(sketch, "E1057", {"start": v(49.01, 171.19) * mm, "end": v(49.7, 170.31) * mm});
            skLineSegment(sketch, "E1058", {"start": v(49.7, 170.31) * mm, "end": v(49.9, 169.25) * mm});
            skLineSegment(sketch, "E1059", {"start": v(49.9, 169.25) * mm, "end": v(50.74, 168.73) * mm});
            skLineSegment(sketch, "E1060", {"start": v(50.74, 168.73) * mm, "end": v(51.07, 168.46) * mm});
            skLineSegment(sketch, "E1061", {"start": v(51.07, 168.46) * mm, "end": v(51.4, 168.38) * mm});
            skLineSegment(sketch, "E1062", {"start": v(51.4, 168.38) * mm, "end": v(51.74, 167.59) * mm});
            skLineSegment(sketch, "E1063", {"start": v(51.74, 167.59) * mm, "end": v(52.3, 166.5) * mm});
            skLineSegment(sketch, "E1064", {"start": v(52.3, 166.5) * mm, "end": v(52.84, 165.87) * mm});
            skLineSegment(sketch, "E1065", {"start": v(52.84, 165.87) * mm, "end": v(53.8, 162.67) * mm});
            skLineSegment(sketch, "E1066", {"start": v(53.8, 162.67) * mm, "end": v(54.17, 161.03) * mm});
            skLineSegment(sketch, "E1067", {"start": v(54.17, 161.03) * mm, "end": v(54.97, 160.5) * mm});
            skLineSegment(sketch, "E1068", {"start": v(54.97, 160.5) * mm, "end": v(55.24, 161.57) * mm});
            skLineSegment(sketch, "E1069", {"start": v(55.24, 161.57) * mm, "end": v(55.84, 165.07) * mm});
            skLineSegment(sketch, "E1070", {"start": v(55.84, 165.07) * mm, "end": v(56.46, 166.08) * mm});
            skLineSegment(sketch, "E1071", {"start": v(56.46, 166.08) * mm, "end": v(57.2, 166.66) * mm});
            skLineSegment(sketch, "E1072", {"start": v(57.2, 166.66) * mm, "end": v(58.04, 167.29) * mm});
            skLineSegment(sketch, "E1073", {"start": v(58.04, 167.29) * mm, "end": v(58.4, 167.5) * mm});
            skLineSegment(sketch, "E1074", {"start": v(58.4, 167.5) * mm, "end": v(59.79, 166.89) * mm});
            skLineSegment(sketch, "E1075", {"start": v(59.79, 166.89) * mm, "end": v(61.36, 166.45) * mm});
            skLineSegment(sketch, "E1076", {"start": v(61.36, 166.45) * mm, "end": v(61.77, 166.45) * mm});
            skLineSegment(sketch, "E1077", {"start": v(61.77, 166.45) * mm, "end": v(62.96, 165.34) * mm});
            skLineSegment(sketch, "E1078", {"start": v(62.96, 165.34) * mm, "end": v(63.31, 164.79) * mm});
            skLineSegment(sketch, "E1079", {"start": v(63.31, 164.79) * mm, "end": v(63.66, 164.26) * mm});
            skLineSegment(sketch, "E1080", {"start": v(63.66, 164.26) * mm, "end": v(64.01, 163.74) * mm});
            skLineSegment(sketch, "E1081", {"start": v(64.01, 163.74) * mm, "end": v(64.36, 162.69) * mm});
            skLineSegment(sketch, "E1082", {"start": v(64.36, 162.69) * mm, "end": v(66.2, 159.55) * mm});
            skLineSegment(sketch, "E1083", {"start": v(66.2, 159.55) * mm, "end": v(66.46, 161.47) * mm});
            skLineSegment(sketch, "E1084", {"start": v(66.46, 161.47) * mm, "end": v(66.81, 163.4) * mm});
            skLineSegment(sketch, "E1085", {"start": v(66.81, 163.4) * mm, "end": v(67.22, 164.53) * mm});
            skLineSegment(sketch, "E1086", {"start": v(67.22, 164.53) * mm, "end": v(67.41, 164.7) * mm});
            skLineSegment(sketch, "E1087", {"start": v(67.41, 164.7) * mm, "end": v(68.24, 163.74) * mm});
            skLineSegment(sketch, "E1088", {"start": v(68.24, 163.74) * mm, "end": v(68.91, 164.23) * mm});
            skLineSegment(sketch, "E1089", {"start": v(68.91, 164.23) * mm, "end": v(69.79, 164.93) * mm});
            skLineSegment(sketch, "E1090", {"start": v(69.79, 164.93) * mm, "end": v(70.66, 165.66) * mm});
            skLineSegment(sketch, "E1091", {"start": v(70.66, 165.66) * mm, "end": v(71.84, 166.38) * mm});
            skLineSegment(sketch, "E1092", {"start": v(71.84, 166.38) * mm, "end": v(73, 166.6) * mm});
            skLineSegment(sketch, "E1093", {"start": v(73, 166.6) * mm, "end": v(73.21, 170.5) * mm});
            skLineSegment(sketch, "E1094", {"start": v(73.21, 170.5) * mm, "end": v(73.8, 174.52) * mm});
            skLineSegment(sketch, "E1095", {"start": v(73.8, 174.52) * mm, "end": v(74.16, 176.42) * mm});
            skLineSegment(sketch, "E1096", {"start": v(74.16, 176.42) * mm, "end": v(75.24, 182.63) * mm});
            skLineSegment(sketch, "E1097", {"start": v(75.24, 182.63) * mm, "end": v(76.02, 179.84) * mm});
            skLineSegment(sketch, "E1098", {"start": v(76.02, 179.84) * mm, "end": v(76.2, 184.12) * mm});
            skLineSegment(sketch, "E1099", {"start": v(76.2, 184.12) * mm, "end": v(76.57, 189.63) * mm});
            skLineSegment(sketch, "E1100", {"start": v(76.57, 189.63) * mm, "end": v(77.13, 190.42) * mm});
            skLineSegment(sketch, "E1101", {"start": v(77.13, 190.42) * mm, "end": v(77.55, 190.6) * mm});
            skLineSegment(sketch, "E1102", {"start": v(77.55, 190.6) * mm, "end": v(78.36, 190.94) * mm});
            skLineSegment(sketch, "E1103", {"start": v(78.36, 190.94) * mm, "end": v(78.71, 192.43) * mm});
            skLineSegment(sketch, "E1104", {"start": v(78.71, 192.43) * mm, "end": v(79.8, 190.16) * mm});
            skLineSegment(sketch, "E1105", {"start": v(79.8, 190.16) * mm, "end": v(80.01, 189.54) * mm});
            skLineSegment(sketch, "E1106", {"start": v(80.01, 189.54) * mm, "end": v(80.83, 189.02) * mm});
            skLineSegment(sketch, "E1107", {"start": v(80.83, 189.02) * mm, "end": v(81.16, 188.06) * mm});
            skLineSegment(sketch, "E1108", {"start": v(81.16, 188.06) * mm, "end": v(81.48, 187.45) * mm});
            skLineSegment(sketch, "E1109", {"start": v(81.48, 187.45) * mm, "end": v(81.86, 186.13) * mm});
            skLineSegment(sketch, "E1110", {"start": v(81.86, 186.13) * mm, "end": v(82.27, 185.35) * mm});
            skLineSegment(sketch, "E1111", {"start": v(82.27, 185.35) * mm, "end": v(82.56, 187) * mm});
            skLineSegment(sketch, "E1112", {"start": v(82.56, 187) * mm, "end": v(82.85, 185) * mm});
            skLineSegment(sketch, "E1113", {"start": v(82.85, 185) * mm, "end": v(83.26, 180.53) * mm});
            skLineSegment(sketch, "E1114", {"start": v(83.26, 180.53) * mm, "end": v(83.65, 182.72) * mm});
            skLineSegment(sketch, "E1115", {"start": v(83.65, 182.72) * mm, "end": v(84.27, 180.06) * mm});
            skLineSegment(sketch, "E1116", {"start": v(84.27, 180.06) * mm, "end": v(85, 177.49) * mm});
            skLineSegment(sketch, "E1117", {"start": v(85, 177.49) * mm, "end": v(85.7, 177.03) * mm});
            skLineSegment(sketch, "E1118", {"start": v(85.7, 177.03) * mm, "end": v(86.06, 176.28) * mm});
            skLineSegment(sketch, "E1119", {"start": v(86.06, 176.28) * mm, "end": v(86.71, 173.54) * mm});
            skLineSegment(sketch, "E1120", {"start": v(86.71, 173.54) * mm, "end": v(87.02, 170.91) * mm});
            skLineSegment(sketch, "E1121", {"start": v(87.02, 170.91) * mm, "end": v(87.06, 172.92) * mm});
            skLineSegment(sketch, "E1122", {"start": v(87.06, 172.92) * mm, "end": v(87.9, 173.62) * mm});
            skLineSegment(sketch, "E1123", {"start": v(87.9, 173.62) * mm, "end": v(88.1, 175.56) * mm});
            skLineSegment(sketch, "E1124", {"start": v(88.1, 175.56) * mm, "end": v(88.68, 179) * mm});
            skLineSegment(sketch, "E1125", {"start": v(88.68, 179) * mm, "end": v(89.21, 181.7) * mm});
            skLineSegment(sketch, "E1126", {"start": v(89.21, 181.7) * mm, "end": v(89.56, 183.68) * mm});
            skLineSegment(sketch, "E1127", {"start": v(89.56, 183.68) * mm, "end": v(89.9, 181.85) * mm});
            skLineSegment(sketch, "E1128", {"start": v(89.9, 181.85) * mm, "end": v(90.24, 180.53) * mm});
            skLineSegment(sketch, "E1129", {"start": v(90.24, 180.53) * mm, "end": v(90.82, 178.76) * mm});
            skLineSegment(sketch, "E1130", {"start": v(90.82, 178.76) * mm, "end": v(91.68, 177.14) * mm});
            skLineSegment(sketch, "E1131", {"start": v(91.68, 177.14) * mm, "end": v(92.54, 175.95) * mm});
            skLineSegment(sketch, "E1132", {"start": v(92.54, 175.95) * mm, "end": v(93.4, 175.99) * mm});
            skLineSegment(sketch, "E1133", {"start": v(93.4, 175.99) * mm, "end": v(93.75, 177.39) * mm});
            skLineSegment(sketch, "E1134", {"start": v(93.75, 177.39) * mm, "end": v(94.1, 176.86) * mm});
            skLineSegment(sketch, "E1135", {"start": v(94.1, 176.86) * mm, "end": v(94.41, 176.34) * mm});
            skLineSegment(sketch, "E1136", {"start": v(94.41, 176.34) * mm, "end": v(95.2, 181.02) * mm});
            skLineSegment(sketch, "E1137", {"start": v(95.2, 181.02) * mm, "end": v(95.41, 182.46) * mm});
            skLineSegment(sketch, "E1138", {"start": v(95.41, 182.46) * mm, "end": v(95.9, 181.21) * mm});
            skLineSegment(sketch, "E1139", {"start": v(95.9, 181.21) * mm, "end": v(96.44, 175.35) * mm});
            skLineSegment(sketch, "E1140", {"start": v(96.44, 175.35) * mm, "end": v(96.96, 169.69) * mm});
            skLineSegment(sketch, "E1141", {"start": v(96.96, 169.69) * mm, "end": v(97.3, 171.7) * mm});
            skLineSegment(sketch, "E1142", {"start": v(97.3, 171.7) * mm, "end": v(97.57, 172.34) * mm});
            skLineSegment(sketch, "E1143", {"start": v(97.57, 172.34) * mm, "end": v(98.78, 172.03) * mm});
            skLineSegment(sketch, "E1144", {"start": v(98.78, 172.03) * mm, "end": v(99.2, 180.97) * mm});
            skLineSegment(sketch, "E1145", {"start": v(99.2, 180.97) * mm, "end": v(99.7, 188.58) * mm});
            skLineSegment(sketch, "E1146", {"start": v(99.7, 188.58) * mm, "end": v(100.46, 181.76) * mm});
            skLineSegment(sketch, "E1147", {"start": v(100.46, 181.76) * mm, "end": v(100.66, 180.27) * mm});
            skLineSegment(sketch, "E1148", {"start": v(100.66, 180.27) * mm, "end": v(101.1, 181.93) * mm});
            skLineSegment(sketch, "E1149", {"start": v(101.1, 181.93) * mm, "end": v(101.55, 183.07) * mm});
            skLineSegment(sketch, "E1150", {"start": v(101.55, 183.07) * mm, "end": v(101.75, 182.28) * mm});
            skLineSegment(sketch, "E1151", {"start": v(101.75, 182.28) * mm, "end": v(102.14, 180.87) * mm});
            skLineSegment(sketch, "E1152", {"start": v(102.14, 180.87) * mm, "end": v(102.7, 181.14) * mm});
            skLineSegment(sketch, "E1153", {"start": v(102.7, 181.14) * mm, "end": v(103.53, 172.22) * mm});
            skLineSegment(sketch, "E1154", {"start": v(103.53, 172.22) * mm, "end": v(103.86, 169.34) * mm});
            skLineSegment(sketch, "E1155", {"start": v(103.86, 169.34) * mm, "end": v(104.4, 167.76) * mm});
            skLineSegment(sketch, "E1156", {"start": v(104.4, 167.76) * mm, "end": v(105.1, 166.19) * mm});
            skLineSegment(sketch, "E1157", {"start": v(105.1, 166.19) * mm, "end": v(106.06, 170.87) * mm});
            skLineSegment(sketch, "E1158", {"start": v(106.06, 170.87) * mm, "end": v(106.25, 172.22) * mm});
            skLineSegment(sketch, "E1159", {"start": v(106.25, 172.22) * mm, "end": v(106.72, 171.09) * mm});
            skLineSegment(sketch, "E1160", {"start": v(106.72, 171.09) * mm, "end": v(107.1, 169.43) * mm});
            skLineSegment(sketch, "E1161", {"start": v(107.1, 169.43) * mm, "end": v(107.4, 168.81) * mm});
            skLineSegment(sketch, "E1162", {"start": v(107.4, 168.81) * mm, "end": v(107.7, 169.39) * mm});
            skLineSegment(sketch, "E1163", {"start": v(107.7, 169.39) * mm, "end": v(108.28, 169.11) * mm});
            skLineSegment(sketch, "E1164", {"start": v(108.28, 169.11) * mm, "end": v(108.83, 168.54) * mm});
            skLineSegment(sketch, "E1165", {"start": v(108.83, 168.54) * mm, "end": v(109.06, 168.29) * mm});
            skLineSegment(sketch, "E1166", {"start": v(109.06, 168.29) * mm, "end": v(109.57, 169.02) * mm});
            skLineSegment(sketch, "E1167", {"start": v(109.57, 169.02) * mm, "end": v(110.17, 172.17) * mm});
            skLineSegment(sketch, "E1168", {"start": v(110.17, 172.17) * mm, "end": v(110.45, 175.11) * mm});
            skLineSegment(sketch, "E1169", {"start": v(110.45, 175.11) * mm, "end": v(110.5, 172.05) * mm});
            skLineSegment(sketch, "E1170", {"start": v(110.5, 172.05) * mm, "end": v(111.3, 170.83) * mm});
            skLineSegment(sketch, "E1171", {"start": v(111.3, 170.83) * mm, "end": v(111.35, 172.66) * mm});
            skLineSegment(sketch, "E1172", {"start": v(111.35, 172.66) * mm, "end": v(111.6, 171.09) * mm});
            skLineSegment(sketch, "E1173", {"start": v(111.6, 171.09) * mm, "end": v(111.9, 170.15) * mm});
            skLineSegment(sketch, "E1174", {"start": v(111.9, 170.15) * mm, "end": v(112.45, 171.3) * mm});
            skLineSegment(sketch, "E1175", {"start": v(112.45, 171.3) * mm, "end": v(113.1, 170.48) * mm});
            skLineSegment(sketch, "E1176", {"start": v(113.1, 170.48) * mm, "end": v(113.23, 169.16) * mm});
            skLineSegment(sketch, "E1177", {"start": v(113.23, 169.16) * mm, "end": v(113.3, 170.48) * mm});
            skLineSegment(sketch, "E1178", {"start": v(113.3, 170.48) * mm, "end": v(113.87, 171.79) * mm});
            skLineSegment(sketch, "E1179", {"start": v(113.87, 171.79) * mm, "end": v(114.4, 171.09) * mm});
            skLineSegment(sketch, "E1180", {"start": v(114.4, 171.09) * mm, "end": v(115.13, 171.18) * mm});
            skLineSegment(sketch, "E1181", {"start": v(115.13, 171.18) * mm, "end": v(115.45, 171.09) * mm});
            skLineSegment(sketch, "E1182", {"start": v(115.45, 171.09) * mm, "end": v(115.76, 169.11) * mm});
            skLineSegment(sketch, "E1183", {"start": v(115.76, 169.11) * mm, "end": v(116.31, 167.82) * mm});
            skLineSegment(sketch, "E1184", {"start": v(116.31, 167.82) * mm, "end": v(116.93, 172.39) * mm});
            skLineSegment(sketch, "E1185", {"start": v(116.93, 172.39) * mm, "end": v(117.46, 177.3) * mm});
            skLineSegment(sketch, "E1186", {"start": v(117.46, 177.3) * mm, "end": v(117.95, 175.75) * mm});
            skLineSegment(sketch, "E1187", {"start": v(117.95, 175.75) * mm, "end": v(118.01, 174.06) * mm});
            skLineSegment(sketch, "E1188", {"start": v(118.01, 174.06) * mm, "end": v(118.25, 175.99) * mm});
            skLineSegment(sketch, "E1189", {"start": v(118.25, 175.99) * mm, "end": v(118.48, 177.91) * mm});
            skLineSegment(sketch, "E1190", {"start": v(118.48, 177.91) * mm, "end": v(118.54, 176.07) * mm});
            skLineSegment(sketch, "E1191", {"start": v(118.54, 176.07) * mm, "end": v(118.95, 174.24) * mm});
            skLineSegment(sketch, "E1192", {"start": v(118.95, 174.24) * mm, "end": v(119.34, 172.57) * mm});
            skLineSegment(sketch, "E1193", {"start": v(119.34, 172.57) * mm, "end": v(119.96, 172.4) * mm});
            skLineSegment(sketch, "E1194", {"start": v(119.96, 172.4) * mm, "end": v(120.83, 174.67) * mm});
            skLineSegment(sketch, "E1195", {"start": v(120.83, 174.67) * mm, "end": v(121.24, 171.87) * mm});
            skLineSegment(sketch, "E1196", {"start": v(121.24, 171.87) * mm, "end": v(122.14, 171.35) * mm});
            skLineSegment(sketch, "E1197", {"start": v(122.14, 171.35) * mm, "end": v(122.18, 172.31) * mm});
            skLineSegment(sketch, "E1198", {"start": v(122.18, 172.31) * mm, "end": v(122.45, 171.26) * mm});
            skLineSegment(sketch, "E1199", {"start": v(122.45, 171.26) * mm, "end": v(122.75, 168.35) * mm});
            skLineSegment(sketch, "E1200", {"start": v(122.75, 168.35) * mm, "end": v(123.96, 165.93) * mm});
            skLineSegment(sketch, "E1201", {"start": v(123.96, 165.93) * mm, "end": v(124.17, 165.23) * mm});
            skLineSegment(sketch, "E1202", {"start": v(124.17, 165.23) * mm, "end": v(124.9, 164.53) * mm});
            skLineSegment(sketch, "E1203", {"start": v(124.9, 164.53) * mm, "end": v(125.25, 164.44) * mm});
            skLineSegment(sketch, "E1204", {"start": v(125.25, 164.44) * mm, "end": v(125.59, 162.64) * mm});
            skLineSegment(sketch, "E1205", {"start": v(125.59, 162.64) * mm, "end": v(126.76, 161.57) * mm});
            skLineSegment(sketch, "E1206", {"start": v(126.76, 161.57) * mm, "end": v(126.95, 161.03) * mm});
            skLineSegment(sketch, "E1207", {"start": v(126.95, 161.03) * mm, "end": v(127.48, 159.9) * mm});
            skLineSegment(sketch, "E1208", {"start": v(127.48, 159.9) * mm, "end": v(128.4, 162.37) * mm});
            skLineSegment(sketch, "E1209", {"start": v(128.4, 162.37) * mm, "end": v(128.74, 163.74) * mm});
            skLineSegment(sketch, "E1210", {"start": v(128.74, 163.74) * mm, "end": v(129.14, 165.05) * mm});
            skLineSegment(sketch, "E1211", {"start": v(129.14, 165.05) * mm, "end": v(129.75, 167.68) * mm});
            skLineSegment(sketch, "E1212", {"start": v(129.75, 167.68) * mm, "end": v(130.14, 166.89) * mm});
            skLineSegment(sketch, "E1213", {"start": v(130.14, 166.89) * mm, "end": v(130.5, 166.34) * mm});
            skLineSegment(sketch, "E1214", {"start": v(130.5, 166.34) * mm, "end": v(131.87, 164.79) * mm});
            skLineSegment(sketch, "E1215", {"start": v(131.87, 164.79) * mm, "end": v(132.24, 164.26) * mm});
            skLineSegment(sketch, "E1216", {"start": v(132.24, 164.26) * mm, "end": v(132.6, 163.74) * mm});
            skLineSegment(sketch, "E1217", {"start": v(132.6, 163.74) * mm, "end": v(132.95, 162.95) * mm});
            skLineSegment(sketch, "E1218", {"start": v(132.95, 162.95) * mm, "end": v(133.3, 161.64) * mm});
            skLineSegment(sketch, "E1219", {"start": v(133.3, 161.64) * mm, "end": v(133.64, 161.9) * mm});
            skLineSegment(sketch, "E1220", {"start": v(133.64, 161.9) * mm, "end": v(134.62, 162.27) * mm});
            skLineSegment(sketch, "E1221", {"start": v(134.62, 162.27) * mm, "end": v(135.04, 162.62) * mm});
            skLineSegment(sketch, "E1222", {"start": v(135.04, 162.62) * mm, "end": v(135.88, 161.73) * mm});
            skLineSegment(sketch, "E1223", {"start": v(135.88, 161.73) * mm, "end": v(137, 159.28) * mm});
            skLineSegment(sketch, "E1224", {"start": v(137, 159.28) * mm, "end": v(137.49, 163.3) * mm});
            skLineSegment(sketch, "E1225", {"start": v(137.49, 163.3) * mm, "end": v(137.79, 166.1) * mm});
            skLineSegment(sketch, "E1226", {"start": v(137.79, 166.1) * mm, "end": v(139.68, 165.12) * mm});
            skLineSegment(sketch, "E1227", {"start": v(139.68, 165.12) * mm, "end": v(140.32, 164.55) * mm});
            skLineSegment(sketch, "E1228", {"start": v(140.32, 164.55) * mm, "end": v(140.52, 164.35) * mm});
            skLineSegment(sketch, "E1229", {"start": v(140.52, 164.35) * mm, "end": v(141.7, 164.3) * mm});
            skLineSegment(sketch, "E1230", {"start": v(141.7, 164.3) * mm, "end": v(143.79, 163.64) * mm});
            skLineSegment(sketch, "E1231", {"start": v(143.79, 163.64) * mm, "end": v(144.49, 173.7) * mm});
            skLineSegment(sketch, "E1232", {"start": v(144.49, 173.7) * mm, "end": v(145.2, 185.78) * mm});
            skLineSegment(sketch, "E1233", {"start": v(145.2, 185.78) * mm, "end": v(145.73, 184.47) * mm});
            skLineSegment(sketch, "E1234", {"start": v(145.73, 184.47) * mm, "end": v(146.15, 183.8) * mm});
            skLineSegment(sketch, "E1235", {"start": v(146.15, 183.8) * mm, "end": v(146.77, 184.25) * mm});
            skLineSegment(sketch, "E1236", {"start": v(146.77, 184.25) * mm, "end": v(147.4, 184.84) * mm});
            skLineSegment(sketch, "E1237", {"start": v(147.4, 184.84) * mm, "end": v(147.6, 182.72) * mm});
            skLineSegment(sketch, "E1238", {"start": v(147.6, 182.72) * mm, "end": v(148.4, 182.2) * mm});
            skLineSegment(sketch, "E1239", {"start": v(148.4, 182.2) * mm, "end": v(148.6, 182.87) * mm});
            skLineSegment(sketch, "E1240", {"start": v(148.6, 182.87) * mm, "end": v(149.23, 181.37) * mm});
            skLineSegment(sketch, "E1241", {"start": v(149.23, 181.37) * mm, "end": v(149.8, 179.56) * mm});
            skLineSegment(sketch, "E1242", {"start": v(149.8, 179.56) * mm, "end": v(149.87, 177.56) * mm});
            skLineSegment(sketch, "E1243", {"start": v(149.87, 177.56) * mm, "end": v(150, 179.57) * mm});
            skLineSegment(sketch, "E1244", {"start": v(150, 179.57) * mm, "end": v(150.4, 181.58) * mm});
            skLineSegment(sketch, "E1245", {"start": v(150.4, 181.58) * mm, "end": v(151.49, 177.18) * mm});
            skLineSegment(sketch, "E1246", {"start": v(151.49, 177.18) * mm, "end": v(152.24, 176.95) * mm});
            skLineSegment(sketch, "E1247", {"start": v(152.24, 176.95) * mm, "end": v(152.52, 173.78) * mm});
            skLineSegment(sketch, "E1248", {"start": v(152.52, 173.78) * mm, "end": v(153.22, 169.7) * mm});
            skLineSegment(sketch, "E1249", {"start": v(153.22, 169.7) * mm, "end": v(153.95, 168.06) * mm});
            skLineSegment(sketch, "E1250", {"start": v(153.95, 168.06) * mm, "end": v(154.25, 168.55) * mm});
            skLineSegment(sketch, "E1251", {"start": v(154.25, 168.55) * mm, "end": v(154.6, 170.39) * mm});
            skLineSegment(sketch, "E1252", {"start": v(154.6, 170.39) * mm, "end": v(155.13, 173.1) * mm});
            skLineSegment(sketch, "E1253", {"start": v(155.13, 173.1) * mm, "end": v(156.42, 179.94) * mm});
            skLineSegment(sketch, "E1254", {"start": v(156.42, 179.94) * mm, "end": v(157.09, 178.78) * mm});
            skLineSegment(sketch, "E1255", {"start": v(157.09, 178.78) * mm, "end": v(157.4, 177.33) * mm});
            skLineSegment(sketch, "E1256", {"start": v(157.4, 177.33) * mm, "end": v(158.05, 171.8) * mm});
            skLineSegment(sketch, "E1257", {"start": v(158.05, 171.8) * mm, "end": v(158.79, 166.26) * mm});
            skLineSegment(sketch, "E1258", {"start": v(158.79, 166.26) * mm, "end": v(159.2, 165.37) * mm});
            skLineSegment(sketch, "E1259", {"start": v(159.2, 165.37) * mm, "end": v(159.54, 165.14) * mm});
            skLineSegment(sketch, "E1260", {"start": v(159.54, 165.14) * mm, "end": v(159.88, 169.43) * mm});
            skLineSegment(sketch, "E1261", {"start": v(159.88, 169.43) * mm, "end": v(161.02, 173.23) * mm});
            skLineSegment(sketch, "E1262", {"start": v(161.02, 173.23) * mm, "end": v(161.28, 173.89) * mm});
            skLineSegment(sketch, "E1263", {"start": v(161.28, 173.89) * mm, "end": v(161.8, 174.59) * mm});
            skLineSegment(sketch, "E1264", {"start": v(161.8, 174.59) * mm, "end": v(162.42, 177.47) * mm});
            skLineSegment(sketch, "E1265", {"start": v(162.42, 177.47) * mm, "end": v(162.61, 175.4) * mm});
            skLineSegment(sketch, "E1266", {"start": v(162.61, 175.4) * mm, "end": v(163.05, 170.32) * mm});
            skLineSegment(sketch, "E1267", {"start": v(163.05, 170.32) * mm, "end": v(163.71, 168.46) * mm});
            skLineSegment(sketch, "E1268", {"start": v(163.71, 168.46) * mm, "end": v(164, 166.71) * mm});
            skLineSegment(sketch, "E1269", {"start": v(164, 166.71) * mm, "end": v(164.04, 168.55) * mm});
            skLineSegment(sketch, "E1270", {"start": v(164.04, 168.55) * mm, "end": v(164.6, 170.39) * mm});
            skLineSegment(sketch, "E1271", {"start": v(164.6, 170.39) * mm, "end": v(165.23, 168.55) * mm});
            skLineSegment(sketch, "E1272", {"start": v(165.23, 168.55) * mm, "end": v(165.42, 169.25) * mm});
            skLineSegment(sketch, "E1273", {"start": v(165.42, 169.25) * mm, "end": v(165.82, 171.79) * mm});
            skLineSegment(sketch, "E1274", {"start": v(165.82, 171.79) * mm, "end": v(166.27, 169.08) * mm});
            skLineSegment(sketch, "E1275", {"start": v(166.27, 169.08) * mm, "end": v(166.46, 171) * mm});
            skLineSegment(sketch, "E1276", {"start": v(166.46, 171) * mm, "end": v(167.81, 171.8) * mm});
            skLineSegment(sketch, "E1277", {"start": v(167.81, 171.8) * mm, "end": v(168.67, 171) * mm});
            skLineSegment(sketch, "E1278", {"start": v(168.67, 171) * mm, "end": v(168.93, 171.54) * mm});
            skLineSegment(sketch, "E1279", {"start": v(168.93, 171.54) * mm, "end": v(170.39, 173.77) * mm});
            skLineSegment(sketch, "E1280", {"start": v(170.39, 173.77) * mm, "end": v(170.68, 171.31) * mm});
            skLineSegment(sketch, "E1281", {"start": v(170.68, 171.31) * mm, "end": v(171.24, 166.66) * mm});
            skLineSegment(sketch, "E1282", {"start": v(171.24, 166.66) * mm, "end": v(171.88, 165.38) * mm});
            skLineSegment(sketch, "E1283", {"start": v(171.88, 165.38) * mm, "end": v(172.07, 166.1) * mm});
            skLineSegment(sketch, "E1284", {"start": v(172.07, 166.1) * mm, "end": v(172.97, 166.89) * mm});
            skLineSegment(sketch, "E1285", {"start": v(172.97, 166.89) * mm, "end": v(173.67, 165.49) * mm});
            skLineSegment(sketch, "E1286", {"start": v(173.67, 165.49) * mm, "end": v(174.63, 168.81) * mm});
            skLineSegment(sketch, "E1287", {"start": v(174.63, 168.81) * mm, "end": v(174.83, 169.43) * mm});
            skLineSegment(sketch, "E1288", {"start": v(174.83, 169.43) * mm, "end": v(175.8, 170.65) * mm});
            skLineSegment(sketch, "E1289", {"start": v(175.8, 170.65) * mm, "end": v(176.3, 170.65) * mm});
            skLineSegment(sketch, "E1290", {"start": v(176.3, 170.65) * mm, "end": v(176.67, 167.59) * mm});
            skLineSegment(sketch, "E1291", {"start": v(176.67, 167.59) * mm, "end": v(177.34, 166.45) * mm});
            skLineSegment(sketch, "E1292", {"start": v(177.34, 166.45) * mm, "end": v(177.7, 168.03) * mm});
            skLineSegment(sketch, "E1293", {"start": v(177.7, 168.03) * mm, "end": v(178.08, 170.74) * mm});
            skLineSegment(sketch, "E1294", {"start": v(178.08, 170.74) * mm, "end": v(178.48, 169.78) * mm});
            skLineSegment(sketch, "E1295", {"start": v(178.48, 169.78) * mm, "end": v(178.78, 170.39) * mm});
            skLineSegment(sketch, "E1296", {"start": v(178.78, 170.39) * mm, "end": v(179.02, 171.96) * mm});
            skLineSegment(sketch, "E1297", {"start": v(179.02, 171.96) * mm, "end": v(179.08, 170.65) * mm});
            skLineSegment(sketch, "E1298", {"start": v(179.08, 170.65) * mm, "end": v(179.48, 169.34) * mm});
            skLineSegment(sketch, "E1299", {"start": v(179.48, 169.34) * mm, "end": v(179.89, 168.03) * mm});
            skLineSegment(sketch, "E1300", {"start": v(179.89, 168.03) * mm, "end": v(180.18, 168.81) * mm});
            skLineSegment(sketch, "E1301", {"start": v(180.18, 168.81) * mm, "end": v(180.41, 170.91) * mm});
            skLineSegment(sketch, "E1302", {"start": v(180.41, 170.91) * mm, "end": v(180.47, 168.9) * mm});
            skLineSegment(sketch, "E1303", {"start": v(180.47, 168.9) * mm, "end": v(181.05, 166.89) * mm});
            skLineSegment(sketch, "E1304", {"start": v(181.05, 166.89) * mm, "end": v(181.58, 168.99) * mm});
            skLineSegment(sketch, "E1305", {"start": v(181.58, 168.99) * mm, "end": v(182.1, 171.09) * mm});
            skLineSegment(sketch, "E1306", {"start": v(182.1, 171.09) * mm, "end": v(182.69, 168.2) * mm});
            skLineSegment(sketch, "E1307", {"start": v(182.69, 168.2) * mm, "end": v(182.75, 165.31) * mm});
            skLineSegment(sketch, "E1308", {"start": v(182.75, 165.31) * mm, "end": v(182.98, 167.41) * mm});
            skLineSegment(sketch, "E1309", {"start": v(182.98, 167.41) * mm, "end": v(183.27, 168.55) * mm});
            skLineSegment(sketch, "E1310", {"start": v(183.27, 168.55) * mm, "end": v(183.68, 167.59) * mm});
            skLineSegment(sketch, "E1311", {"start": v(183.68, 167.59) * mm, "end": v(184.03, 166.89) * mm});
            skLineSegment(sketch, "E1312", {"start": v(184.03, 166.89) * mm, "end": v(184.52, 166.19) * mm});
            skLineSegment(sketch, "E1313", {"start": v(184.52, 166.19) * mm, "end": v(185.2, 165.75) * mm});
            skLineSegment(sketch, "E1314", {"start": v(185.2, 165.75) * mm, "end": v(185.4, 166.25) * mm});
            skLineSegment(sketch, "E1315", {"start": v(185.4, 166.25) * mm, "end": v(186.5, 166.45) * mm});
            skLineSegment(sketch, "E1316", {"start": v(186.5, 166.45) * mm, "end": v(186.9, 165.4) * mm});
            skLineSegment(sketch, "E1317", {"start": v(186.9, 165.4) * mm, "end": v(187.88, 165.68) * mm});
            skLineSegment(sketch, "E1318", {"start": v(187.88, 165.68) * mm, "end": v(189.16, 163.4) * mm});
            skLineSegment(sketch, "E1319", {"start": v(189.16, 163.4) * mm, "end": v(189.63, 162.99) * mm});
            skLineSegment(sketch, "E1320", {"start": v(189.63, 162.99) * mm, "end": v(190.33, 163.4) * mm});
            skLineSegment(sketch, "E1321", {"start": v(190.33, 163.4) * mm, "end": v(191.03, 164.2) * mm});
            skLineSegment(sketch, "E1322", {"start": v(191.03, 164.2) * mm, "end": v(191.03, 163.1) * mm});
            skLineSegment(sketch, "E1323", {"start": v(191.03, 163.1) * mm, "end": v(191.55, 162.21) * mm});
            skLineSegment(sketch, "E1324", {"start": v(191.55, 162.21) * mm, "end": v(192.08, 161.66) * mm});
            skLineSegment(sketch, "E1325", {"start": v(192.08, 161.66) * mm, "end": v(192.43, 161.12) * mm});
            skLineSegment(sketch, "E1326", {"start": v(192.43, 161.12) * mm, "end": v(192.78, 160.44) * mm});
            skLineSegment(sketch, "E1327", {"start": v(192.78, 160.44) * mm, "end": v(193.91, 159.5) * mm});
            skLineSegment(sketch, "E1328", {"start": v(193.91, 159.5) * mm, "end": v(194.17, 158.84) * mm});
            skLineSegment(sketch, "E1329", {"start": v(194.17, 158.84) * mm, "end": v(194.52, 158.14) * mm});
            skLineSegment(sketch, "E1330", {"start": v(194.52, 158.14) * mm, "end": v(194.88, 158.75) * mm});
            skLineSegment(sketch, "E1331", {"start": v(194.88, 158.75) * mm, "end": v(195.22, 158.84) * mm});
            skLineSegment(sketch, "E1332", {"start": v(195.22, 158.84) * mm, "end": v(195.57, 158.75) * mm});
            skLineSegment(sketch, "E1333", {"start": v(195.57, 158.75) * mm, "end": v(196.08, 159.2) * mm});
            skLineSegment(sketch, "E1334", {"start": v(196.08, 159.2) * mm, "end": v(196.8, 159.9) * mm});
            skLineSegment(sketch, "E1335", {"start": v(196.8, 159.9) * mm, "end": v(198.14, 160.15) * mm});
            skLineSegment(sketch, "E1336", {"start": v(198.14, 160.15) * mm, "end": v(198.35, 160.15) * mm});
            skLineSegment(sketch, "E1337", {"start": v(198.35, 160.15) * mm, "end": v(199.07, 160.06) * mm});
            skLineSegment(sketch, "E1338", {"start": v(199.07, 160.06) * mm, "end": v(199.69, 159.3) * mm});
            skLineSegment(sketch, "E1339", {"start": v(199.69, 159.3) * mm, "end": v(200.47, 158.83) * mm});
            skLineSegment(sketch, "E1340", {"start": v(200.47, 158.83) * mm, "end": v(201.78, 158.38) * mm});
            skLineSegment(sketch, "E1341", {"start": v(201.78, 158.38) * mm, "end": v(202.93, 158.76) * mm});
            skLineSegment(sketch, "E1342", {"start": v(202.93, 158.76) * mm, "end": v(203.31, 158.73) * mm});
            skLineSegment(sketch, "E1343", {"start": v(203.31, 158.73) * mm, "end": v(204.97, 158.15) * mm});
            skLineSegment(sketch, "E1344", {"start": v(204.97, 158.15) * mm, "end": v(209.92, 157.8) * mm});
            skLineSegment(sketch, "E1345", {"start": v(209.92, 157.8) * mm, "end": v(205.55, 157.44) * mm});
            skLineSegment(sketch, "E1346", {"start": v(205.55, 157.44) * mm, "end": v(201.17, 157.02) * mm});
            skLineSegment(sketch, "E1347", {"start": v(201.17, 157.02) * mm, "end": v(200.75, 157.02) * mm});
            skLineSegment(sketch, "E1348", {"start": v(200.75, 157.02) * mm, "end": v(199.77, 156.74) * mm});
            skLineSegment(sketch, "E1349", {"start": v(199.77, 156.74) * mm, "end": v(198.9, 156.04) * mm});
            skLineSegment(sketch, "E1350", {"start": v(198.9, 156.04) * mm, "end": v(198.02, 155.7) * mm});
            skLineSegment(sketch, "E1351", {"start": v(198.02, 155.7) * mm, "end": v(196.87, 156.42) * mm});
            skLineSegment(sketch, "E1352", {"start": v(196.87, 156.42) * mm, "end": v(196.04, 157.12) * mm});
            skLineSegment(sketch, "E1353", {"start": v(196.04, 157.12) * mm, "end": v(194.62, 157.24) * mm});
            skLineSegment(sketch, "E1354", {"start": v(194.62, 157.24) * mm, "end": v(192.27, 154.8) * mm});
            skLineSegment(sketch, "E1355", {"start": v(192.27, 154.8) * mm, "end": v(191.03, 152.86) * mm});
            skLineSegment(sketch, "E1356", {"start": v(191.03, 152.86) * mm, "end": v(189.86, 152.25) * mm});
            skLineSegment(sketch, "E1357", {"start": v(189.86, 152.25) * mm, "end": v(189.67, 152.44) * mm});
            skLineSegment(sketch, "E1358", {"start": v(189.67, 152.44) * mm, "end": v(188.58, 152.18) * mm});
            skLineSegment(sketch, "E1359", {"start": v(188.58, 152.18) * mm, "end": v(188.23, 151.32) * mm});
            skLineSegment(sketch, "E1360", {"start": v(188.23, 151.32) * mm, "end": v(187.88, 150.07) * mm});
            skLineSegment(sketch, "E1361", {"start": v(187.88, 150.07) * mm, "end": v(187.12, 150.18) * mm});
            skLineSegment(sketch, "E1362", {"start": v(187.12, 150.18) * mm, "end": v(186.83, 149.22) * mm});
            skLineSegment(sketch, "E1363", {"start": v(186.83, 149.22) * mm, "end": v(186.54, 148.43) * mm});
            skLineSegment(sketch, "E1364", {"start": v(186.54, 148.43) * mm, "end": v(186.32, 149.74) * mm});
            skLineSegment(sketch, "E1365", {"start": v(186.32, 149.74) * mm, "end": v(184.28, 147.04) * mm});
            skLineSegment(sketch, "E1366", {"start": v(184.28, 147.04) * mm, "end": v(184.08, 148.26) * mm});
            skLineSegment(sketch, "E1367", {"start": v(184.08, 148.26) * mm, "end": v(183.68, 150.44) * mm});
            skLineSegment(sketch, "E1368", {"start": v(183.68, 150.44) * mm, "end": v(183.32, 150.36) * mm});
            skLineSegment(sketch, "E1369", {"start": v(183.32, 150.36) * mm, "end": v(183, 147) * mm});
            skLineSegment(sketch, "E1370", {"start": v(183, 147) * mm, "end": v(182.48, 143.53) * mm});
            skLineSegment(sketch, "E1371", {"start": v(182.48, 143.53) * mm, "end": v(181.55, 145.65) * mm});
            skLineSegment(sketch, "E1372", {"start": v(181.55, 145.65) * mm, "end": v(181.33, 147.47) * mm});
            skLineSegment(sketch, "E1373", {"start": v(181.33, 147.47) * mm, "end": v(181.28, 145.95) * mm});
            skLineSegment(sketch, "E1374", {"start": v(181.28, 145.95) * mm, "end": v(180.14, 145.57) * mm});
            skLineSegment(sketch, "E1375", {"start": v(180.14, 145.57) * mm, "end": v(179.86, 145.46) * mm});
            skLineSegment(sketch, "E1376", {"start": v(179.86, 145.46) * mm, "end": v(179.5, 144.5) * mm});
            skLineSegment(sketch, "E1377", {"start": v(179.5, 144.5) * mm, "end": v(179.03, 145.46) * mm});
            skLineSegment(sketch, "E1378", {"start": v(179.03, 145.46) * mm, "end": v(178.77, 143.62) * mm});
            skLineSegment(sketch, "E1379", {"start": v(178.77, 143.62) * mm, "end": v(178.52, 142.66) * mm});
            skLineSegment(sketch, "E1380", {"start": v(178.52, 142.66) * mm, "end": v(178.06, 144.5) * mm});
            skLineSegment(sketch, "E1381", {"start": v(178.06, 144.5) * mm, "end": v(177.67, 147.38) * mm});
            skLineSegment(sketch, "E1382", {"start": v(177.67, 147.38) * mm, "end": v(177.62, 150.27) * mm});
            skLineSegment(sketch, "E1383", {"start": v(177.62, 150.27) * mm, "end": v(177.27, 146.25) * mm});
            skLineSegment(sketch, "E1384", {"start": v(177.27, 146.25) * mm, "end": v(176.67, 142.05) * mm});
            skLineSegment(sketch, "E1385", {"start": v(176.67, 142.05) * mm, "end": v(176.24, 141) * mm});
            skLineSegment(sketch, "E1386", {"start": v(176.24, 141) * mm, "end": v(176, 142.92) * mm});
            skLineSegment(sketch, "E1387", {"start": v(176, 142.92) * mm, "end": v(175.75, 145.28) * mm});
            skLineSegment(sketch, "E1388", {"start": v(175.75, 145.28) * mm, "end": v(174.9, 147.38) * mm});
            skLineSegment(sketch, "E1389", {"start": v(174.9, 147.38) * mm, "end": v(174.58, 149.04) * mm});
            skLineSegment(sketch, "E1390", {"start": v(174.58, 149.04) * mm, "end": v(174.27, 149.3) * mm});
            skLineSegment(sketch, "E1391", {"start": v(174.27, 149.3) * mm, "end": v(173.25, 148.6) * mm});
            skLineSegment(sketch, "E1392", {"start": v(173.25, 148.6) * mm, "end": v(172.91, 146.77) * mm});
            skLineSegment(sketch, "E1393", {"start": v(172.91, 146.77) * mm, "end": v(172.87, 148.6) * mm});
            skLineSegment(sketch, "E1394", {"start": v(172.87, 148.6) * mm, "end": v(172.07, 147.9) * mm});
            skLineSegment(sketch, "E1395", {"start": v(172.07, 147.9) * mm, "end": v(171.9, 147.12) * mm});
            skLineSegment(sketch, "E1396", {"start": v(171.9, 147.12) * mm, "end": v(171.07, 151.14) * mm});
            skLineSegment(sketch, "E1397", {"start": v(171.07, 151.14) * mm, "end": v(170.7, 141.6) * mm});
            skLineSegment(sketch, "E1398", {"start": v(170.7, 141.6) * mm, "end": v(170.38, 132.95) * mm});
            skLineSegment(sketch, "E1399", {"start": v(170.38, 132.95) * mm, "end": v(170.07, 135.31) * mm});
            skLineSegment(sketch, "E1400", {"start": v(170.07, 135.31) * mm, "end": v(169.73, 136.8) * mm});
            skLineSegment(sketch, "E1401", {"start": v(169.73, 136.8) * mm, "end": v(169.15, 135.31) * mm});
            skLineSegment(sketch, "E1402", {"start": v(169.15, 135.31) * mm, "end": v(168.73, 134.44) * mm});
            skLineSegment(sketch, "E1403", {"start": v(168.73, 134.44) * mm, "end": v(167.9, 133.21) * mm});
            skLineSegment(sketch, "E1404", {"start": v(167.9, 133.21) * mm, "end": v(167.58, 130.5) * mm});
            skLineSegment(sketch, "E1405", {"start": v(167.58, 130.5) * mm, "end": v(167.27, 139.16) * mm});
            skLineSegment(sketch, "E1406", {"start": v(167.27, 139.16) * mm, "end": v(166.88, 148.7) * mm});
            skLineSegment(sketch, "E1407", {"start": v(166.88, 148.7) * mm, "end": v(166.53, 147.3) * mm});
            skLineSegment(sketch, "E1408", {"start": v(166.53, 147.3) * mm, "end": v(166, 146.12) * mm});
            skLineSegment(sketch, "E1409", {"start": v(166, 146.12) * mm, "end": v(165.43, 145.5) * mm});
            skLineSegment(sketch, "E1410", {"start": v(165.43, 145.5) * mm, "end": v(165.13, 146.07) * mm});
            skLineSegment(sketch, "E1411", {"start": v(165.13, 146.07) * mm, "end": v(164.88, 147.47) * mm});
            skLineSegment(sketch, "E1412", {"start": v(164.88, 147.47) * mm, "end": v(164.83, 145.78) * mm});
            skLineSegment(sketch, "E1413", {"start": v(164.83, 145.78) * mm, "end": v(163.7, 146.45) * mm});
            skLineSegment(sketch, "E1414", {"start": v(163.7, 146.45) * mm, "end": v(163.44, 145.28) * mm});
            skLineSegment(sketch, "E1415", {"start": v(163.44, 145.28) * mm, "end": v(163.03, 142.05) * mm});
            skLineSegment(sketch, "E1416", {"start": v(163.03, 142.05) * mm, "end": v(162.62, 131.46) * mm});
            skLineSegment(sketch, "E1417", {"start": v(162.62, 131.46) * mm, "end": v(162.32, 127.18) * mm});
            skLineSegment(sketch, "E1418", {"start": v(162.32, 127.18) * mm, "end": v(162.03, 134.79) * mm});
            skLineSegment(sketch, "E1419", {"start": v(162.03, 134.79) * mm, "end": v(161.63, 136.1) * mm});
            skLineSegment(sketch, "E1420", {"start": v(161.63, 136.1) * mm, "end": v(161.23, 130.59) * mm});
            skLineSegment(sketch, "E1421", {"start": v(161.23, 130.59) * mm, "end": v(161.17, 125.08) * mm});
            skLineSegment(sketch, "E1422", {"start": v(161.17, 125.08) * mm, "end": v(160.83, 129.36) * mm});
            skLineSegment(sketch, "E1423", {"start": v(160.83, 129.36) * mm, "end": v(160.19, 133.65) * mm});
            skLineSegment(sketch, "E1424", {"start": v(160.19, 133.65) * mm, "end": v(159.84, 140.73) * mm});
            skLineSegment(sketch, "E1425", {"start": v(159.84, 140.73) * mm, "end": v(159.55, 150.27) * mm});
            skLineSegment(sketch, "E1426", {"start": v(159.55, 150.27) * mm, "end": v(159.3, 152.72) * mm});
            skLineSegment(sketch, "E1427", {"start": v(159.3, 152.72) * mm, "end": v(159.24, 149.51) * mm});
            skLineSegment(sketch, "E1428", {"start": v(159.24, 149.51) * mm, "end": v(158.77, 146.16) * mm});
            skLineSegment(sketch, "E1429", {"start": v(158.77, 146.16) * mm, "end": v(158, 137.21) * mm});
            skLineSegment(sketch, "E1430", {"start": v(158, 137.21) * mm, "end": v(157.38, 128.4) * mm});
            skLineSegment(sketch, "E1431", {"start": v(157.38, 128.4) * mm, "end": v(157.01, 129.01) * mm});
            skLineSegment(sketch, "E1432", {"start": v(157.01, 129.01) * mm, "end": v(156.74, 125.25) * mm});
            skLineSegment(sketch, "E1433", {"start": v(156.74, 125.25) * mm, "end": v(156.53, 120.88) * mm});
            skLineSegment(sketch, "E1434", {"start": v(156.53, 120.88) * mm, "end": v(156.46, 126.56) * mm});
            skLineSegment(sketch, "E1435", {"start": v(156.46, 126.56) * mm, "end": v(155.64, 126.74) * mm});
            skLineSegment(sketch, "E1436", {"start": v(155.64, 126.74) * mm, "end": v(155.34, 122.28) * mm});
            skLineSegment(sketch, "E1437", {"start": v(155.34, 122.28) * mm, "end": v(155.03, 131.99) * mm});
            skLineSegment(sketch, "E1438", {"start": v(155.03, 131.99) * mm, "end": v(154.64, 140.65) * mm});
            skLineSegment(sketch, "E1439", {"start": v(154.64, 140.65) * mm, "end": v(154.26, 143.18) * mm});
            skLineSegment(sketch, "E1440", {"start": v(154.26, 143.18) * mm, "end": v(153.95, 147.3) * mm});
            skLineSegment(sketch, "E1441", {"start": v(153.95, 147.3) * mm, "end": v(153.67, 148.87) * mm});
            skLineSegment(sketch, "E1442", {"start": v(153.67, 148.87) * mm, "end": v(153.63, 146.89) * mm});
            skLineSegment(sketch, "E1443", {"start": v(153.63, 146.89) * mm, "end": v(153.27, 144.79) * mm});
            skLineSegment(sketch, "E1444", {"start": v(153.27, 144.79) * mm, "end": v(152.5, 137.94) * mm});
            skLineSegment(sketch, "E1445", {"start": v(152.5, 137.94) * mm, "end": v(151.77, 131.2) * mm});
            skLineSegment(sketch, "E1446", {"start": v(151.77, 131.2) * mm, "end": v(151.46, 128.49) * mm});
            skLineSegment(sketch, "E1447", {"start": v(151.46, 128.49) * mm, "end": v(150.81, 125.51) * mm});
            skLineSegment(sketch, "E1448", {"start": v(150.81, 125.51) * mm, "end": v(150.05, 124.29) * mm});
            skLineSegment(sketch, "E1449", {"start": v(150.05, 124.29) * mm, "end": v(149.74, 120.88) * mm});
            skLineSegment(sketch, "E1450", {"start": v(149.74, 120.88) * mm, "end": v(149.43, 126.04) * mm});
            skLineSegment(sketch, "E1451", {"start": v(149.43, 126.04) * mm, "end": v(148.63, 128.34) * mm});
            skLineSegment(sketch, "E1452", {"start": v(148.63, 128.34) * mm, "end": v(148.08, 124.29) * mm});
            skLineSegment(sketch, "E1453", {"start": v(148.08, 124.29) * mm, "end": v(147.57, 123.56) * mm});
            skLineSegment(sketch, "E1454", {"start": v(147.57, 123.56) * mm, "end": v(147.29, 126.13) * mm});
            skLineSegment(sketch, "E1455", {"start": v(147.29, 126.13) * mm, "end": v(147, 123.41) * mm});
            skLineSegment(sketch, "E1456", {"start": v(147, 123.41) * mm, "end": v(146.59, 117.55) * mm});
            skLineSegment(sketch, "E1457", {"start": v(146.59, 117.55) * mm, "end": v(146.2, 116.42) * mm});
            skLineSegment(sketch, "E1458", {"start": v(146.2, 116.42) * mm, "end": v(146.16, 115.28) * mm});
            skLineSegment(sketch, "E1459", {"start": v(146.16, 115.28) * mm, "end": v(145.89, 116.33) * mm});
            skLineSegment(sketch, "E1460", {"start": v(145.89, 116.33) * mm, "end": v(145.58, 121.64) * mm});
            skLineSegment(sketch, "E1461", {"start": v(145.58, 121.64) * mm, "end": v(145.2, 126) * mm});
            skLineSegment(sketch, "E1462", {"start": v(145.2, 126) * mm, "end": v(144.62, 138.84) * mm});
            skLineSegment(sketch, "E1463", {"start": v(144.62, 138.84) * mm, "end": v(143.82, 151.76) * mm});
            skLineSegment(sketch, "E1464", {"start": v(143.82, 151.76) * mm, "end": v(143, 152.34) * mm});
            skLineSegment(sketch, "E1465", {"start": v(143, 152.34) * mm, "end": v(142.75, 151.93) * mm});
            skLineSegment(sketch, "E1466", {"start": v(142.75, 151.93) * mm, "end": v(142.4, 151.14) * mm});
            skLineSegment(sketch, "E1467", {"start": v(142.4, 151.14) * mm, "end": v(142.02, 150.53) * mm});
            skLineSegment(sketch, "E1468", {"start": v(142.02, 150.53) * mm, "end": v(141.7, 150.62) * mm});
            skLineSegment(sketch, "E1469", {"start": v(141.7, 150.62) * mm, "end": v(141.37, 150.7) * mm});
            skLineSegment(sketch, "E1470", {"start": v(141.37, 150.7) * mm, "end": v(141, 150.1) * mm});
            skLineSegment(sketch, "E1471", {"start": v(141, 150.1) * mm, "end": v(140.64, 149.48) * mm});
            skLineSegment(sketch, "E1472", {"start": v(140.64, 149.48) * mm, "end": v(140.33, 149.35) * mm});
            skLineSegment(sketch, "E1473", {"start": v(140.33, 149.35) * mm, "end": v(139.83, 149.35) * mm});
            skLineSegment(sketch, "E1474", {"start": v(139.83, 149.35) * mm, "end": v(139.3, 149.37) * mm});
            skLineSegment(sketch, "E1475", {"start": v(139.3, 149.37) * mm, "end": v(138.83, 148.52) * mm});
            skLineSegment(sketch, "E1476", {"start": v(138.83, 148.52) * mm, "end": v(138.1, 147.78) * mm});
            skLineSegment(sketch, "E1477", {"start": v(138.1, 147.78) * mm, "end": v(137.49, 152.48) * mm});
            skLineSegment(sketch, "E1478", {"start": v(137.49, 152.48) * mm, "end": v(136.71, 157.43) * mm});
            skLineSegment(sketch, "E1479", {"start": v(136.71, 157.43) * mm, "end": v(135.74, 153.66) * mm});
            skLineSegment(sketch, "E1480", {"start": v(135.74, 153.66) * mm, "end": v(135.02, 152.98) * mm});
            skLineSegment(sketch, "E1481", {"start": v(135.02, 152.98) * mm, "end": v(134.62, 152.63) * mm});
            skLineSegment(sketch, "E1482", {"start": v(134.62, 152.63) * mm, "end": v(133.56, 153.16) * mm});
            skLineSegment(sketch, "E1483", {"start": v(133.56, 153.16) * mm, "end": v(133.43, 154.47) * mm});
            skLineSegment(sketch, "E1484", {"start": v(133.43, 154.47) * mm, "end": v(133.14, 152.98) * mm});
            skLineSegment(sketch, "E1485", {"start": v(133.14, 152.98) * mm, "end": v(132.55, 151.5) * mm});
            skLineSegment(sketch, "E1486", {"start": v(132.55, 151.5) * mm, "end": v(132.24, 150.1) * mm});
            skLineSegment(sketch, "E1487", {"start": v(132.24, 150.1) * mm, "end": v(131.08, 149.3) * mm});
            skLineSegment(sketch, "E1488", {"start": v(131.08, 149.3) * mm, "end": v(130.86, 148.34) * mm});
            skLineSegment(sketch, "E1489", {"start": v(130.86, 148.34) * mm, "end": v(130.61, 147.2) * mm});
            skLineSegment(sketch, "E1490", {"start": v(130.61, 147.2) * mm, "end": v(129.98, 147.64) * mm});
            skLineSegment(sketch, "E1491", {"start": v(129.98, 147.64) * mm, "end": v(129.3, 148.87) * mm});
            skLineSegment(sketch, "E1492", {"start": v(129.3, 148.87) * mm, "end": v(128.73, 150.1) * mm});
            skLineSegment(sketch, "E1493", {"start": v(128.73, 150.1) * mm, "end": v(128.37, 152.8) * mm});
            skLineSegment(sketch, "E1494", {"start": v(128.37, 152.8) * mm, "end": v(127.72, 155.6) * mm});
            skLineSegment(sketch, "E1495", {"start": v(127.72, 155.6) * mm, "end": v(126.95, 155.25) * mm});
            skLineSegment(sketch, "E1496", {"start": v(126.95, 155.25) * mm, "end": v(126.65, 154.83) * mm});
            skLineSegment(sketch, "E1497", {"start": v(126.65, 154.83) * mm, "end": v(125.99, 153.32) * mm});
            skLineSegment(sketch, "E1498", {"start": v(125.99, 153.32) * mm, "end": v(125.6, 152.28) * mm});
            skLineSegment(sketch, "E1499", {"start": v(125.6, 152.28) * mm, "end": v(125.38, 151.6) * mm});
            skLineSegment(sketch, "E1500", {"start": v(125.38, 151.6) * mm, "end": v(124.2, 148.93) * mm});
            skLineSegment(sketch, "E1501", {"start": v(124.2, 148.93) * mm, "end": v(123.5, 147.2) * mm});
            skLineSegment(sketch, "E1502", {"start": v(123.5, 147.2) * mm, "end": v(122.73, 143.4) * mm});
            skLineSegment(sketch, "E1503", {"start": v(122.73, 143.4) * mm, "end": v(122.45, 141.87) * mm});
            skLineSegment(sketch, "E1504", {"start": v(122.45, 141.87) * mm, "end": v(122.22, 144.32) * mm});
            skLineSegment(sketch, "E1505", {"start": v(122.22, 144.32) * mm, "end": v(122.16, 142.34) * mm});
            skLineSegment(sketch, "E1506", {"start": v(122.16, 142.34) * mm, "end": v(121.66, 140.21) * mm});
            skLineSegment(sketch, "E1507", {"start": v(121.66, 140.21) * mm, "end": v(121.02, 136.77) * mm});
            skLineSegment(sketch, "E1508", {"start": v(121.02, 136.77) * mm, "end": v(120.76, 139.86) * mm});
            skLineSegment(sketch, "E1509", {"start": v(120.76, 139.86) * mm, "end": v(120.43, 146.25) * mm});
            skLineSegment(sketch, "E1510", {"start": v(120.43, 146.25) * mm, "end": v(119.3, 141.53) * mm});
            skLineSegment(sketch, "E1511", {"start": v(119.3, 141.53) * mm, "end": v(118.95, 139.6) * mm});
            skLineSegment(sketch, "E1512", {"start": v(118.95, 139.6) * mm, "end": v(118.55, 136.54) * mm});
            skLineSegment(sketch, "E1513", {"start": v(118.55, 136.54) * mm, "end": v(118.5, 133.47) * mm});
            skLineSegment(sketch, "E1514", {"start": v(118.5, 133.47) * mm, "end": v(118.2, 136.97) * mm});
            skLineSegment(sketch, "E1515", {"start": v(118.2, 136.97) * mm, "end": v(117.54, 140.59) * mm});
            skLineSegment(sketch, "E1516", {"start": v(117.54, 140.59) * mm, "end": v(117.2, 141.99) * mm});
            skLineSegment(sketch, "E1517", {"start": v(117.2, 141.99) * mm, "end": v(116.85, 143.8) * mm});
            skLineSegment(sketch, "E1518", {"start": v(116.85, 143.8) * mm, "end": v(116.5, 141.78) * mm});
            skLineSegment(sketch, "E1519", {"start": v(116.5, 141.78) * mm, "end": v(116.2, 139.25) * mm});
            skLineSegment(sketch, "E1520", {"start": v(116.2, 139.25) * mm, "end": v(115.67, 133.21) * mm});
            skLineSegment(sketch, "E1521", {"start": v(115.67, 133.21) * mm, "end": v(114.76, 120.35) * mm});
            skLineSegment(sketch, "E1522", {"start": v(114.76, 120.35) * mm, "end": v(114.27, 123.59) * mm});
            skLineSegment(sketch, "E1523", {"start": v(114.27, 123.59) * mm, "end": v(113.7, 126.94) * mm});
            skLineSegment(sketch, "E1524", {"start": v(113.7, 126.94) * mm, "end": v(113.31, 136.39) * mm});
            skLineSegment(sketch, "E1525", {"start": v(113.31, 136.39) * mm, "end": v(113, 144.85) * mm});
            skLineSegment(sketch, "E1526", {"start": v(113, 144.85) * mm, "end": v(112.68, 142.83) * mm});
            skLineSegment(sketch, "E1527", {"start": v(112.68, 142.83) * mm, "end": v(112.13, 141.7) * mm});
            skLineSegment(sketch, "E1528", {"start": v(112.13, 141.7) * mm, "end": v(111.51, 137.06) * mm});
            skLineSegment(sketch, "E1529", {"start": v(111.51, 137.06) * mm, "end": v(111.4, 132.42) * mm});
            skLineSegment(sketch, "E1530", {"start": v(111.4, 132.42) * mm, "end": v(111.33, 137.24) * mm});
            skLineSegment(sketch, "E1531", {"start": v(111.33, 137.24) * mm, "end": v(110.92, 142.05) * mm});
            skLineSegment(sketch, "E1532", {"start": v(110.92, 142.05) * mm, "end": v(110.45, 141.26) * mm});
            skLineSegment(sketch, "E1533", {"start": v(110.45, 141.26) * mm, "end": v(110.2, 142.4) * mm});
            skLineSegment(sketch, "E1534", {"start": v(110.2, 142.4) * mm, "end": v(109.96, 143.7) * mm});
            skLineSegment(sketch, "E1535", {"start": v(109.96, 143.7) * mm, "end": v(109.13, 143.88) * mm});
            skLineSegment(sketch, "E1536", {"start": v(109.13, 143.88) * mm, "end": v(108.8, 143.97) * mm});
            skLineSegment(sketch, "E1537", {"start": v(108.8, 143.97) * mm, "end": v(108.47, 144.09) * mm});
            skLineSegment(sketch, "E1538", {"start": v(108.47, 144.09) * mm, "end": v(108.01, 144.76) * mm});
            skLineSegment(sketch, "E1539", {"start": v(108.01, 144.76) * mm, "end": v(107.38, 141.32) * mm});
            skLineSegment(sketch, "E1540", {"start": v(107.38, 141.32) * mm, "end": v(107.12, 140.2) * mm});
            skLineSegment(sketch, "E1541", {"start": v(107.12, 140.2) * mm, "end": v(106.26, 140.73) * mm});
            skLineSegment(sketch, "E1542", {"start": v(106.26, 140.73) * mm, "end": v(106.06, 141.6) * mm});
            skLineSegment(sketch, "E1543", {"start": v(106.06, 141.6) * mm, "end": v(105.48, 144.15) * mm});
            skLineSegment(sketch, "E1544", {"start": v(105.48, 144.15) * mm, "end": v(104.92, 143.53) * mm});
            skLineSegment(sketch, "E1545", {"start": v(104.92, 143.53) * mm, "end": v(104.6, 143.8) * mm});
            skLineSegment(sketch, "E1546", {"start": v(104.6, 143.8) * mm, "end": v(104.29, 143.53) * mm});
            skLineSegment(sketch, "E1547", {"start": v(104.29, 143.53) * mm, "end": v(103.95, 142.4) * mm});
            skLineSegment(sketch, "E1548", {"start": v(103.95, 142.4) * mm, "end": v(103.42, 133.39) * mm});
            skLineSegment(sketch, "E1549", {"start": v(103.42, 133.39) * mm, "end": v(103, 122.89) * mm});
            skLineSegment(sketch, "E1550", {"start": v(103, 122.89) * mm, "end": v(102.1, 122.36) * mm});
            skLineSegment(sketch, "E1551", {"start": v(102.1, 122.36) * mm, "end": v(101.8, 121.58) * mm});
            skLineSegment(sketch, "E1552", {"start": v(101.8, 121.58) * mm, "end": v(101.56, 119.83) * mm});
            skLineSegment(sketch, "E1553", {"start": v(101.56, 119.83) * mm, "end": v(101.5, 122.19) * mm});
            skLineSegment(sketch, "E1554", {"start": v(101.5, 122.19) * mm, "end": v(101.1, 124.55) * mm});
            skLineSegment(sketch, "E1555", {"start": v(101.1, 124.55) * mm, "end": v(100.7, 130.59) * mm});
            skLineSegment(sketch, "E1556", {"start": v(100.7, 130.59) * mm, "end": v(100.63, 136.62) * mm});
            skLineSegment(sketch, "E1557", {"start": v(100.63, 136.62) * mm, "end": v(100.38, 130.32) * mm});
            skLineSegment(sketch, "E1558", {"start": v(100.38, 130.32) * mm, "end": v(100.1, 117.5) * mm});
            skLineSegment(sketch, "E1559", {"start": v(100.1, 117.5) * mm, "end": v(99.53, 110.78) * mm});
            skLineSegment(sketch, "E1560", {"start": v(99.53, 110.78) * mm, "end": v(99, 124.2) * mm});
            skLineSegment(sketch, "E1561", {"start": v(99, 124.2) * mm, "end": v(98.4, 138.15) * mm});
            skLineSegment(sketch, "E1562", {"start": v(98.4, 138.15) * mm, "end": v(97.57, 140.53) * mm});
            skLineSegment(sketch, "E1563", {"start": v(97.57, 140.53) * mm, "end": v(97.36, 142.57) * mm});
            skLineSegment(sketch, "E1564", {"start": v(97.36, 142.57) * mm, "end": v(97.3, 140.24) * mm});
            skLineSegment(sketch, "E1565", {"start": v(97.3, 140.24) * mm, "end": v(96.87, 137.78) * mm});
            skLineSegment(sketch, "E1566", {"start": v(96.87, 137.78) * mm, "end": v(96.3, 127.43) * mm});
            skLineSegment(sketch, "E1567", {"start": v(96.3, 127.43) * mm, "end": v(95.86, 117.2) * mm});
            skLineSegment(sketch, "E1568", {"start": v(95.86, 117.2) * mm, "end": v(95.16, 130.02) * mm});
            skLineSegment(sketch, "E1569", {"start": v(95.16, 130.02) * mm, "end": v(94.43, 136.1) * mm});
            skLineSegment(sketch, "E1570", {"start": v(94.43, 136.1) * mm, "end": v(94.01, 134.26) * mm});
            skLineSegment(sketch, "E1571", {"start": v(94.01, 134.26) * mm, "end": v(93.82, 135.08) * mm});
            skLineSegment(sketch, "E1572", {"start": v(93.82, 135.08) * mm, "end": v(93, 142.05) * mm});
            skLineSegment(sketch, "E1573", {"start": v(93, 142.05) * mm, "end": v(92.66, 137.24) * mm});
            skLineSegment(sketch, "E1574", {"start": v(92.66, 137.24) * mm, "end": v(92.06, 129.36) * mm});
            skLineSegment(sketch, "E1575", {"start": v(92.06, 129.36) * mm, "end": v(91.53, 130.85) * mm});
            skLineSegment(sketch, "E1576", {"start": v(91.53, 130.85) * mm, "end": v(90.6, 121.17) * mm});
            skLineSegment(sketch, "E1577", {"start": v(90.6, 121.17) * mm, "end": v(90.26, 116.85) * mm});
            skLineSegment(sketch, "E1578", {"start": v(90.26, 116.85) * mm, "end": v(89.82, 109.94) * mm});
            skLineSegment(sketch, "E1579", {"start": v(89.82, 109.94) * mm, "end": v(89.57, 107.58) * mm});
            skSolve(sketch);
        }
        {
            var Q0;
            Q0=makeQuery(id+"F0.imprint","IMPRINT",FACE,{"disambiguationData":[TD([[makeQuery(id+"F0.imprint","IMPRINT",EDGE,{"derivedFrom":sQuery(id+"F0.wireOp",EDGE,"E790")}),-1.0]])]});
            extrude(context, id + "F1", {"entities" : qUnion([Q0]), "depth" : 25 * mm});
        }
    });
